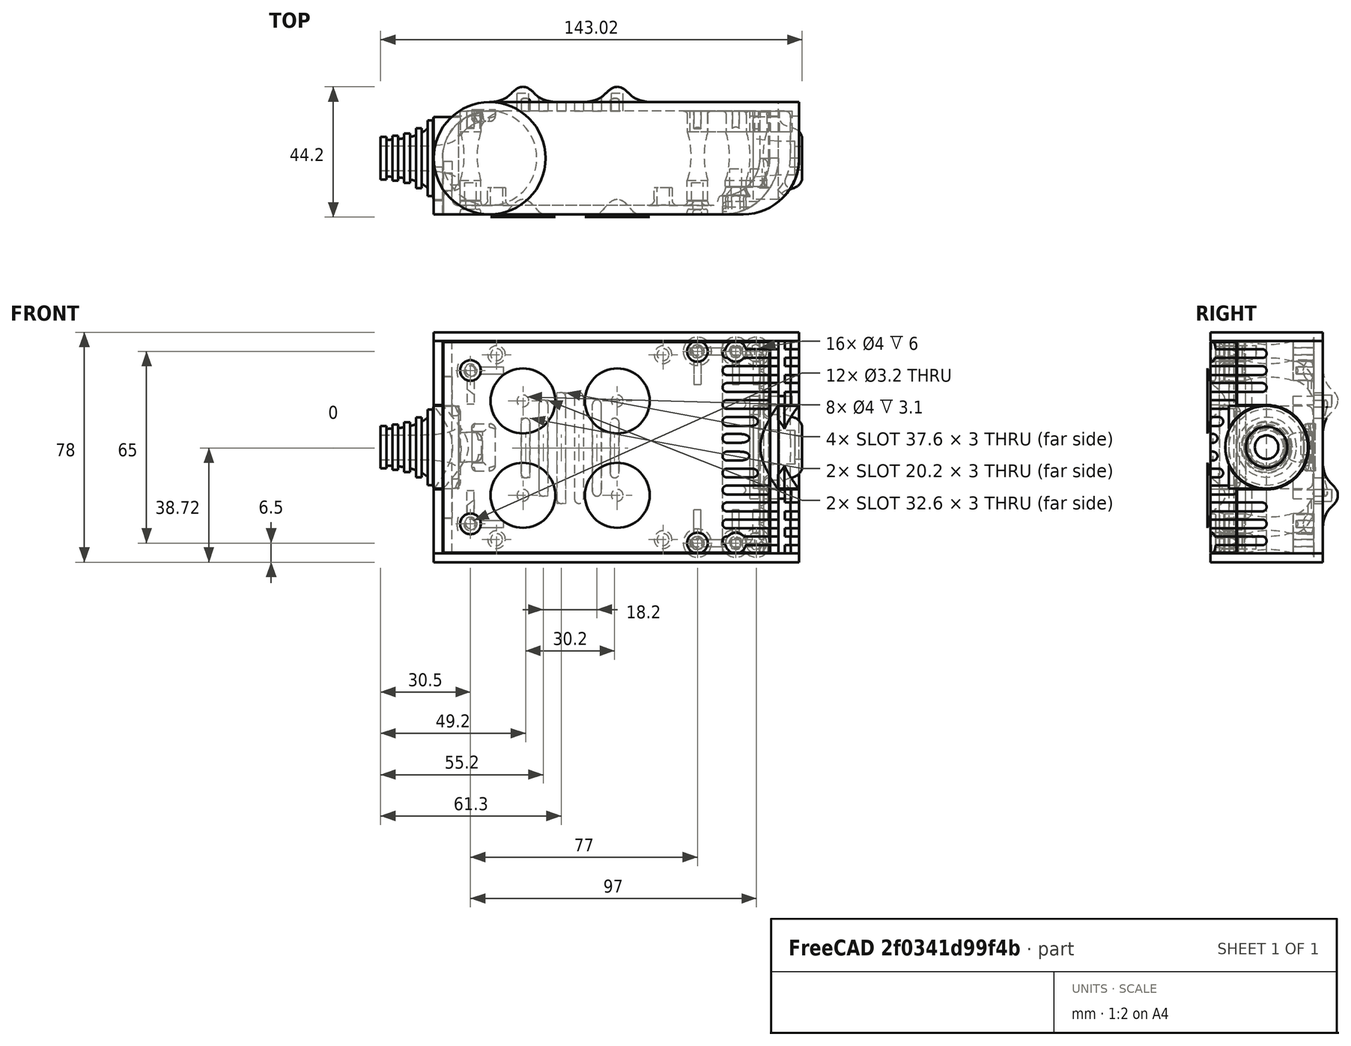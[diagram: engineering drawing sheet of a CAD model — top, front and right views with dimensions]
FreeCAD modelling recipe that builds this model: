
FCSTD DOCUMENT  (FreeCAD 0.19R0.19.2)
Label: enclosure_146
License: All rights reserved
LicenseURL: http://en.wikipedia.org/wiki/All_rights_reserved
objects: Part::Feature×96, Part::Revolution×96, Part::MultiFuse×79, Sketcher::SketchObject×52, Part::Extrusion×40, Part::Cut×39, Part::Fillet×36, Part::Cylinder×36, Part::Box×23, App::MeasureDistance×4
note: 497 computed .brp shape members not serialized (recipe doc carries the construction recipe); baked Part::Feature solids carry a one-line shape summary decoded from their .brp

FEATURE [Sketcher::SketchObject] Sketch  label="topSketch"
  FullyConstrained = true
  sketch-geometry (20):
    g0: LineSegment StartX=5.21097e-06 StartY=3 StartZ=0 EndX=5.21097e-06 EndY=19 EndZ=0
    g1: ArcOfCircle CenterX=19 CenterY=19 CenterZ=0 NormalX=0 NormalY=0 NormalZ=1 AngleXU=0 Radius=19 StartAngle=1.5708 EndAngle=3.14159
    g2: ArcOfCircle CenterX=19 CenterY=19 CenterZ=0 NormalX=0 NormalY=0 NormalZ=1 AngleXU=0 Radius=16 StartAngle=1.5708 EndAngle=3.14159
    g3: LineSegment StartX=114 StartY=35 StartZ=0 EndX=19 EndY=35 EndZ=0
    g4: LineSegment StartX=5.21097e-06 StartY=3 StartZ=0 EndX=5.21097e-06 EndY=0 EndZ=0
    g5: LineSegment StartX=3 StartY=0 StartZ=0 EndX=5.21097e-06 EndY=0 EndZ=0
    g6: LineSegment StartX=3 StartY=19 StartZ=0 EndX=3 EndY=0 EndZ=0
    g7: LineSegment StartX=19 StartY=38 StartZ=0 EndX=124 EndY=38 EndZ=0
    g8: Circle CenterX=119 CenterY=35 CenterZ=0 NormalX=0 NormalY=0 NormalZ=1 AngleXU=0 Radius=1
    g9: Circle CenterX=121 CenterY=35 CenterZ=0 NormalX=0 NormalY=0 NormalZ=1 AngleXU=0 Radius=1
    g10: Circle CenterX=121 CenterY=33 CenterZ=0 NormalX=0 NormalY=0 NormalZ=1 AngleXU=0 Radius=1
    g11: BSplineCurve PolesCount=3 KnotsCount=2 Degree=2 IsPeriodic=0
    g12: GeomPoint X=119 Y=35 Z=0
    g13: GeomPoint X=121 Y=33 Z=0
    g14: LineSegment StartX=119 StartY=35 StartZ=0 EndX=114 EndY=35 EndZ=0
    g15: ArcOfCircle CenterX=105 CenterY=19 CenterZ=0 NormalX=0 NormalY=0 NormalZ=1 AngleXU=0 Radius=19 StartAngle=5.7297 EndAngle=6.28319
    g16: ArcOfCircle CenterX=105 CenterY=19 CenterZ=0 NormalX=0 NormalY=0 NormalZ=1 AngleXU=0 Radius=16 StartAngle=5.60905 EndAngle=6.28319
    g17: LineSegment StartX=121 StartY=33 StartZ=0 EndX=121 EndY=19 EndZ=0
    g18: LineSegment StartX=124 StartY=38 StartZ=0 EndX=124 EndY=19 EndZ=0
    g19: LineSegment StartX=117.5 StartY=9.01251 StartZ=0 EndX=121.163 EndY=9.0125 EndZ=0
  constraints (46):
    c: Vertical(g0)
    c: Block(g0)
    c: Coincident(g1,g0)
    c: Block(g1)
    c: Coincident(g2,g1)
    c: Block(g2)
    c: Coincident(g3,g2)
    c: Horizontal(g3)
    c: Tangent(g3,g2)
    c: Coincident(g4,g0)
    c: Distance(g4) = 3
    c: Vertical(g4)
    c: Coincident(g5,g4)
    c: Horizontal(g5)
    c: Coincident(g6,g2)
    c: Coincident(g6,g5)
    c: Vertical(g6)
    c: Horizontal(g7)
    c: Distance(g7) = 105
    c: Coincident(g7,g1)
    c: Block(g3)
    c: Weight(g8) = 1
    c: Equal(g8,g9)
    c: Equal(g8,g10)
    c: InternalAlignment(g8,g11)
    c: InternalAlignment(g9,g11)
    c: InternalAlignment(g10,g11)
    c: InternalAlignment(g12,g11)
    c: InternalAlignment(g13,g11)
    c: Block(g11)
    c: Coincident(g14,g11)
    c: Coincident(g14,g3)
    c: Horizontal(g14)
    c: Block(g15)
    c: Coincident(g16,g15)
    c: Block(g16)
    c: Coincident(g17,g11)
    c: Coincident(g17,g16)
    c: Vertical(g17)
    c: Distance(g17) = 14
    c: Coincident(g18,g7)
    c: Coincident(g18,g15)
    c: Vertical(g18)
    c: Distance(g18) = 19
    c: Coincident(g19,g16)
    c: Coincident(g19,g15)
FEATURE [Sketcher::SketchObject] Sketch001  label="bottomSketch"
  FullyConstrained = true
  sketch-geometry (32):
    g0: LineSegment StartX=3.3 StartY=-6.03275e-07 StartZ=0 EndX=98 EndY=-6.03275e-07 EndZ=0
    g1: ArcOfCircle CenterX=98 CenterY=19 CenterZ=0 NormalX=0 NormalY=0 NormalZ=1 AngleXU=0 Radius=19 StartAngle=4.71239 EndAngle=5.71103
    g2: LineSegment StartX=6.3 StartY=8 StartZ=0 EndX=3.3 EndY=8 EndZ=0
    g3: LineSegment StartX=3.3 StartY=8 StartZ=0 EndX=3.3 EndY=-6.03275e-07 EndZ=0
    g4: ArcOfCircle CenterX=8.3 CenterY=5 CenterZ=0 NormalX=0 NormalY=0 NormalZ=1 AngleXU=0 Radius=2 StartAngle=3.14159 EndAngle=4.71239
    g5: LineSegment StartX=6.3 StartY=8 StartZ=0 EndX=6.3 EndY=5 EndZ=0
    g6: ArcOfCircle CenterX=98 CenterY=19 CenterZ=0 NormalX=0 NormalY=0 NormalZ=1 AngleXU=0 Radius=12.7 StartAngle=4.71239 EndAngle=6.28319
    g7: LineSegment StartX=94.7 StartY=3 StartZ=0 EndX=8.3 EndY=3 EndZ=0
    g8-g12: Circle x5 (B-spline internal-alignment scaffolding for g13; pole/knot coordinates omitted)
    g13: BSplineCurve PolesCount=5 KnotsCount=3 Degree=3 IsPeriodic=0
    g14: GeomPoint X=98 Y=6.3 Z=0
    g15: GeomPoint X=96.3938 Y=4.71946 Z=0
    g16: GeomPoint X=94.7 Y=3 Z=0
    g17-g23: Circle x7 (B-spline internal-alignment scaffolding for g24; pole/knot coordinates omitted)
    g24: BSplineCurve PolesCount=7 KnotsCount=5 Degree=3 IsPeriodic=0
    g25-g29: GeomPoint x5 (B-spline internal-alignment scaffolding for g24; pole/knot coordinates omitted)
    g30: ArcOfCircle CenterX=98 CenterY=19 CenterZ=0 NormalX=0 NormalY=0 NormalZ=1 AngleXU=0 Radius=15.7 StartAngle=5.81226 EndAngle=6.28319
    g31: LineSegment StartX=110.7 StartY=19 StartZ=0 EndX=113.7 EndY=19 EndZ=0
  constraints (41):
    c: Horizontal(g0)
    c: Coincident(g1,g0)
    c: Block(g1)
    c: Horizontal(g2)
    c: Distance(g2) = 3
    c: Coincident(g3,g2)
    c: Vertical(g3)
    c: Coincident(g3,g0)
    c: Block(g4)
    c: Block(g2)
    c: Coincident(g5,g2)
    c: Coincident(g5,g4)
    c: Vertical(g5)
    c: Coincident(g6,g1)
    c: Block(g6)
    c: Coincident(g7,g4)
    c: Horizontal(g7)
    c: Block(g0)
    c: Block(g7)
    c: Block(g3)
    c: Coincident(g13,g6)
    c: Weight(g8) = 1
    c: Equal(g8, g9-g12) x4
    c: Coincident(g13,g7)
    c: InternalAlignment(g8-g12 -> g13) x5
    c: InternalAlignment(g14,g13)
    c: InternalAlignment(g15,g13)
    c: InternalAlignment(g16,g13)
    c: Block(g13)
    c: Weight(g17) = 1
    c: Equal(g17, g18-g23) x6
    c: Coincident(g24,g1)
    c: InternalAlignment(g17-g23 -> g24) x7
    c: InternalAlignment(g25-g29 -> g24) x5
    c: Block(g24)
    c: Coincident(g30,g24)
    c: Coincident(g31,g6)
    c: Coincident(g31,g30)
    c: Horizontal(g31)
    c: Block(g31)
    c: Block(g30)
FEATURE [Part::Extrusion] Extrude  label="top"
  Base = -> Sketch
  Dir = (0,0,1)
  DirMode = 2
  FaceMakerClass = Part::FaceMakerBullseye
  LengthFwd = 72
  LengthRev = 0
  Solid = true
  Symmetric = false
FEATURE [Part::Extrusion] Extrude001  label="bottom"
  Base = -> Sketch001
  Dir = (0,0,1)
  DirMode = 2
  FaceMakerClass = Part::FaceMakerBullseye
  LengthFwd = 71.4
  LengthRev = 0
  Placement = pos=(0,0,0.3) rot=(0,0,1;0rad)
  Solid = true
  Symmetric = false
FEATURE [Sketcher::SketchObject] Sketch002  label="topSketch001"
  FullyConstrained = true
  sketch-geometry (6):
    g0: ArcOfCircle CenterX=19 CenterY=19 CenterZ=0 NormalX=0 NormalY=0 NormalZ=1 AngleXU=0 Radius=19 StartAngle=1.5708 EndAngle=3.14159
    g1: LineSegment StartX=5.22862e-06 StartY=19 StartZ=0 EndX=5.22862e-06 EndY=1.19904e-11 EndZ=0
    g2: LineSegment StartX=19 StartY=38 StartZ=0 EndX=124 EndY=38 EndZ=0
    g3: LineSegment StartX=5.22862e-06 StartY=1.19904e-11 StartZ=0 EndX=105 EndY=1.19904e-11 EndZ=0
    g4: ArcOfCircle CenterX=105 CenterY=19 CenterZ=0 NormalX=0 NormalY=0 NormalZ=1 AngleXU=0 Radius=19 StartAngle=4.71239 EndAngle=6.28319
    g5: LineSegment StartX=124 StartY=38 StartZ=0 EndX=124 EndY=19 EndZ=0
  constraints (16):
    c: Block(g0)
    c: Coincident(g1,g0)
    c: Vertical(g1)
    c: Horizontal(g2)
    c: Distance(g2) = 105
    c: Coincident(g2,g0)
    c: Distance(g1) = 19
    c: Coincident(g3,g1)
    c: Horizontal(g3)
    c: Distance(g3) = 105
    c: Block(g4)
    c: Coincident(g4,g3)
    c: Coincident(g5,g2)
    c: Coincident(g5,g4)
    c: Vertical(g5)
    c: Distance(g5) = 19
FEATURE [Part::Extrusion] Extrude002  label="sideA"
  Base = -> Sketch002
  Dir = (0,0,1)
  DirMode = 2
  FaceMakerClass = Part::FaceMakerBullseye
  LengthFwd = 3
  LengthRev = 0
  Placement = pos=(0,0,-3) rot=(0,0,1;0rad)
  Solid = true
  Symmetric = false
FEATURE [Sketcher::SketchObject] Sketch003  label="topSketch002"
  FullyConstrained = true
  sketch-geometry (6):
    g0: LineSegment StartX=19 StartY=38 StartZ=0 EndX=117 EndY=38 EndZ=0
    g1: ArcOfCircle CenterX=19 CenterY=19 CenterZ=0 NormalX=0 NormalY=0 NormalZ=1 AngleXU=0 Radius=19 StartAngle=1.5708 EndAngle=3.14159
    g2: LineSegment StartX=117 StartY=38 StartZ=0 EndX=117 EndY=19 EndZ=0
    g3: LineSegment StartX=98 StartY=1.0161e-12 StartZ=0 EndX=5.22862e-06 EndY=1.0161e-12 EndZ=0
    g4: LineSegment StartX=5.22862e-06 StartY=19 StartZ=0 EndX=5.22862e-06 EndY=1.0161e-12 EndZ=0
    g5: ArcOfCircle CenterX=98 CenterY=19 CenterZ=0 NormalX=0 NormalY=0 NormalZ=1 AngleXU=0 Radius=19 StartAngle=4.71239 EndAngle=6.28319
  constraints (16):
    c: Horizontal(g0)
    c: Distance(g0) = 98
    c: Coincident(g1,g0)
    c: Block(g1)
    c: Coincident(g2,g0)
    c: Vertical(g2)
    c: Distance(g2) = 19
    c: Horizontal(g3)
    c: Coincident(g4,g1)
    c: Vertical(g4)
    c: Coincident(g3,g4)
    c: Block(g3)
    c: Coincident(g5,g2)
    c: Coincident(g5,g3)
    c: Block(g0)
    c: Block(g5)
FEATURE [Sketcher::SketchObject] Sketch004
  FullyConstrained = true
  MapMode = 3
  Placement = pos=(0,0,0) rot=(1,0,0;1.5708rad)
  Support = -> [Extrude]
  sketch-geometry (8):
    g0: Circle CenterX=80.351 CenterY=-67.6202 CenterZ=0 NormalX=0 NormalY=0 NormalZ=1 AngleXU=0 Radius=2
    g1: Circle CenterX=80.351 CenterY=-67.6202 CenterZ=0 NormalX=0 NormalY=0 NormalZ=1 AngleXU=0 Radius=3
    g2: Circle CenterX=80.351 CenterY=-4.92017 CenterZ=0 NormalX=0 NormalY=0 NormalZ=1 AngleXU=0 Radius=2
    g3: Circle CenterX=80.351 CenterY=-4.92017 CenterZ=0 NormalX=0 NormalY=0 NormalZ=1 AngleXU=0 Radius=3
    g4: Circle CenterX=23.851 CenterY=-4.92017 CenterZ=0 NormalX=0 NormalY=0 NormalZ=1 AngleXU=0 Radius=2
    g5: Circle CenterX=23.851 CenterY=-4.92017 CenterZ=0 NormalX=0 NormalY=0 NormalZ=1 AngleXU=0 Radius=3
    g6: Circle CenterX=23.851 CenterY=-67.6202 CenterZ=0 NormalX=0 NormalY=0 NormalZ=1 AngleXU=0 Radius=2
    g7: Circle CenterX=23.851 CenterY=-67.6202 CenterZ=0 NormalX=0 NormalY=0 NormalZ=1 AngleXU=0 Radius=3
  constraints (8):
    c: Block(g3)
    c: Block(g2)
    c: Block(g1)
    c: Block(g0)
    c: Block(g6)
    c: Block(g7)
    c: Block(g4)
    c: Block(g5)
FEATURE [Part::Extrusion] Extrude004
  Base = -> Sketch004
  Dir = (0,-1,2e-16)
  DirMode = 2
  FaceMakerClass = Part::FaceMakerBullseye
  LengthFwd = 6
  LengthRev = 0
  Placement = pos=(0,9,0) rot=(0,0,1;0rad)
  Solid = true
  Symmetric = false
FEATURE [Sketcher::SketchObject] Sketch005
  FullyConstrained = true
  MapMode = 3
  Placement = pos=(0,0,0) rot=(1,0,0;1.5708rad)
  Support = -> [Extrude]
  sketch-geometry (8):
    g0: Circle CenterX=80.351 CenterY=-67.6202 CenterZ=0 NormalX=0 NormalY=0 NormalZ=1 AngleXU=0 Radius=3
    g1: Circle CenterX=80.351 CenterY=-4.92017 CenterZ=0 NormalX=0 NormalY=0 NormalZ=1 AngleXU=0 Radius=3
    g2: Circle CenterX=23.851 CenterY=-4.92017 CenterZ=0 NormalX=0 NormalY=0 NormalZ=1 AngleXU=0 Radius=3
    g3: Circle CenterX=23.851 CenterY=-67.6202 CenterZ=0 NormalX=0 NormalY=0 NormalZ=1 AngleXU=0 Radius=3
    g4: Circle CenterX=23.851 CenterY=-67.6202 CenterZ=0 NormalX=0 NormalY=0 NormalZ=1 AngleXU=0 Radius=5
    g5: Circle CenterX=80.351 CenterY=-67.6202 CenterZ=0 NormalX=0 NormalY=0 NormalZ=1 AngleXU=0 Radius=5
    g6: Circle CenterX=23.851 CenterY=-4.92017 CenterZ=0 NormalX=0 NormalY=0 NormalZ=1 AngleXU=0 Radius=5
    g7: Circle CenterX=80.351 CenterY=-4.92017 CenterZ=0 NormalX=0 NormalY=0 NormalZ=1 AngleXU=0 Radius=5
  constraints (8):
    c: Block(g1)
    c: Block(g0)
    c: Block(g3)
    c: Block(g2)
    c: Block(g5)
    c: Block(g4)
    c: Block(g6)
    c: Block(g7)
FEATURE [Part::Extrusion] Extrude005
  Base = -> Sketch005
  Dir = (0,-1,2e-16)
  DirMode = 2
  FaceMakerClass = Part::FaceMakerBullseye
  LengthFwd = 2
  LengthRev = 0
  Solid = true
  Symmetric = false
FEATURE [Sketcher::SketchObject] Sketch006
  FullyConstrained = true
  MapMode = 3
  Placement = pos=(0,0,0) rot=(1,0,0;1.5708rad)
  sketch-geometry (8):
    g0: Circle CenterX=80.351 CenterY=-67.6202 CenterZ=0 NormalX=0 NormalY=0 NormalZ=1 AngleXU=0 Radius=3
    g1: Circle CenterX=80.351 CenterY=-4.92017 CenterZ=0 NormalX=0 NormalY=0 NormalZ=1 AngleXU=0 Radius=3
    g2: Circle CenterX=23.851 CenterY=-4.92017 CenterZ=0 NormalX=0 NormalY=0 NormalZ=1 AngleXU=0 Radius=3
    g3: Circle CenterX=23.851 CenterY=-67.6202 CenterZ=0 NormalX=0 NormalY=0 NormalZ=1 AngleXU=0 Radius=3
    g4: Circle CenterX=23.851 CenterY=-67.6202 CenterZ=0 NormalX=0 NormalY=0 NormalZ=1 AngleXU=0 Radius=5
    g5: Circle CenterX=80.351 CenterY=-67.6202 CenterZ=0 NormalX=0 NormalY=0 NormalZ=1 AngleXU=0 Radius=5
    g6: Circle CenterX=23.851 CenterY=-4.92017 CenterZ=0 NormalX=0 NormalY=0 NormalZ=1 AngleXU=0 Radius=5
    g7: Circle CenterX=80.351 CenterY=-4.92017 CenterZ=0 NormalX=0 NormalY=0 NormalZ=1 AngleXU=0 Radius=5
  constraints (8):
    c: Block(g1)
    c: Block(g0)
    c: Block(g3)
    c: Block(g2)
    c: Block(g5)
    c: Block(g4)
    c: Block(g6)
    c: Block(g7)
FEATURE [Part::Extrusion] Extrude007
  Base = -> Sketch006
  Dir = (0,-1,2e-16)
  DirMode = 2
  FaceMakerClass = Part::FaceMakerBullseye
  LengthFwd = 2
  LengthRev = 0
  Solid = true
  Symmetric = false
FEATURE [Part::Fillet] Fillet
  Base = -> Extrude007
  Edges = 4 edges r=1.99: [Edge6,Edge12,Edge18,Edge24]
FEATURE [Part::Cut] Cut
  Base = -> Extrude005
  Placement = pos=(0,5,0) rot=(0,0,1;0rad)
  Tool = -> Fillet
FEATURE [Part::MultiFuse] Fusion  label="pCBScrews"
  Placement = pos=(-2.5,0,72.3) rot=(0,0,1;0rad)
  Shapes = -> [Extrude004,Cut]
FEATURE [App::MeasureDistance] Distance  label="Distance: 0.69 mm"
  Distance = 0.685967
  P1 = (24.0138,2.9647,0.3)
  P2 = (23.8901,3,-0.373787)
FEATURE [App::MeasureDistance] Distance001  label="Distance: 0.53 mm"
  Distance = 0.533607
  P1 = (80.2939,3,72.2334)
  P2 = (80.281,2.99661,71.7)
FEATURE [Part::Fillet] Fillet001
  Base = -> Extrude001
  Edges = 1 edges r=2.4: [Edge17]
FEATURE [Part::Fillet] Fillet002  label="bottom001"
  Base = -> Fillet001
  Edges = 1 edges r=2.4: [Edge36]
FEATURE [Part::Fillet] Fillet003  label="top001"
  Base = -> Extrude
  Edges = 1 edges r=2: [Edge1]
FEATURE [Sketcher::SketchObject] Sketch007
  FullyConstrained = true
  sketch-geometry (16):
    g0: LineSegment StartX=4 StartY=0 StartZ=0 EndX=4 EndY=2.4 EndZ=0
    g1: LineSegment StartX=4 StartY=2.4 StartZ=0 EndX=7 EndY=2.4 EndZ=0
    g2: LineSegment StartX=4 StartY=0 StartZ=0 EndX=5.7 EndY=0 EndZ=0
    g3: LineSegment StartX=5.7 StartY=0 StartZ=0 EndX=5.7 EndY=-5.6 EndZ=0
    g4-g8: Circle x5 (B-spline internal-alignment scaffolding for g9; pole/knot coordinates omitted)
    g9: BSplineCurve PolesCount=5 KnotsCount=3 Degree=3 IsPeriodic=0
    g10: GeomPoint X=7 Y=2.4 Z=0
    g11: GeomPoint X=10.4582 Y=-1.55472 Z=0
    g12: GeomPoint X=14 Y=-5.6 Z=0
    g13: LineSegment StartX=14 StartY=-5.6 StartZ=0 EndX=14 EndY=-14.1 EndZ=0
    g14: LineSegment StartX=14 StartY=-14.1 StartZ=0 EndX=6.5 EndY=-14.1 EndZ=0
    g15: LineSegment StartX=5.7 StartY=-5.6 StartZ=0 EndX=6.5 EndY=-14.1 EndZ=0
  constraints (28):
    c: Distance(g0) = 2.4
    c: Vertical(g0)
    c: Block(g0)
    c: Coincident(g1,g0)
    c: Horizontal(g1)
    c: Distance(g1) = 3
    c: Coincident(g2,g0)
    c: Horizontal(g2)
    c: Distance(g2) = 1.7
    c: Coincident(g3,g2)
    c: Vertical(g3)
    c: Distance(g3) = 5.6
    c: Coincident(g9,g1)
    c: Weight(g4) = 1
    c: Equal(g4, g5-g8) x4
    c: InternalAlignment(g4-g8 -> g9) x5
    c: InternalAlignment(g10,g9)
    c: InternalAlignment(g11,g9)
    c: InternalAlignment(g12,g9)
    c: Block(g9)
    c: Coincident(g13,g9)
    c: Vertical(g13)
    c: Distance(g13) = 8.5
    c: Coincident(g14,g13)
    c: Horizontal(g14)
    c: Distance(g14) = 7.5
    c: Coincident(g15,g3)
    c: Coincident(g15,g14)
FEATURE [Part::Feature] Face
  shape: bbox 10 x 16.5 x 2e-07 mm, 1 faces, 0 solids (baked)
FEATURE [Part::Revolution] Revolve  label="plugHousing"
  Angle = 360
  Axis = (0,1,0)
  Base = (0,0,0)
  FaceMakerClass = Part::FaceMakerBullseye
  Placement = pos=(0,0,36.15) rot=(0,0,1;0rad)
  Solid = false
  Source = -> Face
  Symmetric = false
FEATURE [Part::Feature] Face001
  shape: bbox 10 x 16.5 x 2e-07 mm, 1 faces, 0 solids (baked)
FEATURE [Part::Revolution] Revolve001  label="plugHousing001"
  Angle = 360
  Axis = (0,1,0)
  Base = (0,0,0)
  FaceMakerClass = Part::FaceMakerBullseye
  Placement = pos=(0,0,36.15) rot=(0,0,1;0rad)
  Solid = false
  Source = -> Face001
  Symmetric = false
FEATURE [Part::MultiFuse] Fusion001  label="plugHousing002"
  Placement = pos=(0,0,0) rot=(0,0,1;1.5708rad)
  Shapes = -> [Revolve001,Revolve]
FEATURE [Part::Feature] Face002
  shape: bbox 10 x 16.5 x 2e-07 mm, 1 faces, 0 solids (baked)
FEATURE [Part::Revolution] Revolve003  label="plugHousing005"
  Angle = 360
  Axis = (0,1,0)
  Base = (0,0,0)
  FaceMakerClass = Part::FaceMakerBullseye
  Placement = pos=(0,0,36.15) rot=(0,0,1;0rad)
  Solid = false
  Source = -> Face002
  Symmetric = false
FEATURE [Part::Feature] Face003
  shape: bbox 10 x 16.5 x 2e-07 mm, 1 faces, 0 solids (baked)
FEATURE [Part::Revolution] Revolve002  label="plugHousing003"
  Angle = 360
  Axis = (0,1,0)
  Base = (0,0,0)
  FaceMakerClass = Part::FaceMakerBullseye
  Placement = pos=(0,0,36.15) rot=(0,0,1;0rad)
  Solid = false
  Source = -> Face003
  Symmetric = false
FEATURE [Part::MultiFuse] Fusion002  label="plugHousing004"
  Placement = pos=(0,0,0) rot=(0,0,1;1.5708rad)
  Shapes = -> [Revolve002,Revolve003]
FEATURE [Part::MultiFuse] Fusion003  label="plugHousing006"
  Placement = pos=(0,19,0) rot=(0,0,1;3.14159rad)
  Shapes = -> [Fusion002,Fusion001]
FEATURE [Part::Feature] Face004
  shape: bbox 10 x 16.5 x 2e-07 mm, 1 faces, 0 solids (baked)
FEATURE [Part::Revolution] Revolve006  label="plugHousing010"
  Angle = 360
  Axis = (0,1,0)
  Base = (0,0,0)
  FaceMakerClass = Part::FaceMakerBullseye
  Placement = pos=(0,0,36.15) rot=(0,0,1;0rad)
  Solid = false
  Source = -> Face004
  Symmetric = false
FEATURE [Part::Feature] Face005
  shape: bbox 10 x 16.5 x 2e-07 mm, 1 faces, 0 solids (baked)
FEATURE [Part::Revolution] Revolve007  label="plugHousing011"
  Angle = 360
  Axis = (0,1,0)
  Base = (0,0,0)
  FaceMakerClass = Part::FaceMakerBullseye
  Placement = pos=(0,0,36.15) rot=(0,0,1;0rad)
  Solid = false
  Source = -> Face005
  Symmetric = false
FEATURE [Part::Feature] Face006
  shape: bbox 10 x 16.5 x 2e-07 mm, 1 faces, 0 solids (baked)
FEATURE [Part::Revolution] Revolve004  label="plugHousing007"
  Angle = 360
  Axis = (0,1,0)
  Base = (0,0,0)
  FaceMakerClass = Part::FaceMakerBullseye
  Placement = pos=(0,0,36.15) rot=(0,0,1;0rad)
  Solid = false
  Source = -> Face006
  Symmetric = false
FEATURE [Part::MultiFuse] Fusion004  label="plugHousing009"
  Placement = pos=(0,0,0) rot=(0,0,1;1.5708rad)
  Shapes = -> [Revolve004,Revolve007]
FEATURE [Part::Feature] Face007
  shape: bbox 10 x 16.5 x 2e-07 mm, 1 faces, 0 solids (baked)
FEATURE [Part::Revolution] Revolve005  label="plugHousing008"
  Angle = 360
  Axis = (0,1,0)
  Base = (0,0,0)
  FaceMakerClass = Part::FaceMakerBullseye
  Placement = pos=(0,0,36.15) rot=(0,0,1;0rad)
  Solid = false
  Source = -> Face007
  Symmetric = false
FEATURE [Part::MultiFuse] Fusion005  label="plugHousing012"
  Placement = pos=(0,0,0) rot=(0,0,1;1.5708rad)
  Shapes = -> [Revolve006,Revolve005]
FEATURE [Part::MultiFuse] Fusion006  label="plugHousing013"
  Placement = pos=(0,19,0) rot=(0,0,1;3.14159rad)
  Shapes = -> [Fusion005,Fusion004]
FEATURE [Part::MultiFuse] Fusion007  label="plugHousing014"
  Placement = pos=(122.621,0,-0.15) rot=(0,0,1;0rad)
  Shapes = -> [Fusion003,Fusion006]
FEATURE [Part::Cylinder] Cylinder002
  Angle = 360
  AttacherType = Attacher::AttachEngine3D
  Height = 20
  Placement = pos=(0,0,36.15) rot=(0,0,1;0rad)
  Radius = 4
FEATURE [Part::Cylinder] Cylinder003
  Angle = 360
  AttacherType = Attacher::AttachEngine3D
  Height = 10
  Placement = pos=(0,0,36.15) rot=(0,0,1;0rad)
  Radius = 4
FEATURE [Part::MultiFuse] Fusion009  label="removeToCreateHoleForPlugHousing"
  Placement = pos=(70,19,36.15) rot=(0,1,0;1.5708rad)
  Shapes = -> [Cylinder002,Cylinder003]
FEATURE [Part::Cylinder] Cylinder004
  Angle = 360
  AttacherType = Attacher::AttachEngine3D
  Height = 20
  Placement = pos=(0,0,36.15) rot=(0,0,1;0rad)
  Radius = 4
FEATURE [Part::Cylinder] Cylinder005
  Angle = 360
  AttacherType = Attacher::AttachEngine3D
  Height = 10
  Placement = pos=(0,0,36.15) rot=(0,0,1;0rad)
  Radius = 4
FEATURE [Part::MultiFuse] Fusion010  label="removeToCreateHoleForPlugHousing001"
  Placement = pos=(70,19,36.15) rot=(0,1,0;1.5708rad)
  Shapes = -> [Cylinder004,Cylinder005]
FEATURE [Part::Cut] Cut001
  Base = -> Fillet003
  Tool = -> Fusion010
FEATURE [Part::Cut] Cut002  label="Bottom"
  Base = -> Fillet002
  Tool = -> Fusion009
FEATURE [Part::Feature] Face008
  shape: bbox 10 x 16.5 x 2e-07 mm, 1 faces, 0 solids (baked)
FEATURE [Part::Revolution] Revolve011  label="plugHousing021"
  Angle = 360
  Axis = (0,1,0)
  Base = (0,0,0)
  FaceMakerClass = Part::FaceMakerBullseye
  Placement = pos=(0,0,36.15) rot=(0,0,1;0rad)
  Solid = false
  Source = -> Face008
  Symmetric = false
FEATURE [Part::Feature] Face009
  shape: bbox 10 x 16.5 x 2e-07 mm, 1 faces, 0 solids (baked)
FEATURE [Part::Revolution] Revolve012  label="plugHousing022"
  Angle = 360
  Axis = (0,1,0)
  Base = (0,0,0)
  FaceMakerClass = Part::FaceMakerBullseye
  Placement = pos=(0,0,36.15) rot=(0,0,1;0rad)
  Solid = false
  Source = -> Face009
  Symmetric = false
FEATURE [Part::Feature] Face010 .. Face013  x4 (patterned run collapsed; names and placements below)
  shape: bbox 10 x 16.5 x 2e-07 mm, 1 faces, 0 solids (baked)
FEATURE [Part::Revolution] Revolve015  label="plugHousing027"
  Angle = 360
  Axis = (0,1,0)
  Base = (0,0,0)
  FaceMakerClass = Part::FaceMakerBullseye
  Placement = pos=(0,0,36.15) rot=(0,0,1;0rad)
  Solid = false
  Source = -> Face013
  Symmetric = false
FEATURE [Part::Feature] Face014
  shape: bbox 10 x 16.5 x 2e-07 mm, 1 faces, 0 solids (baked)
FEATURE [Part::Feature] Face015
  shape: bbox 10 x 16.5 x 2e-07 mm, 1 faces, 0 solids (baked)
FEATURE [Part::Feature] Face016
  shape: bbox 10 x 16.5 x 2e-07 mm, 1 faces, 0 solids (baked)
FEATURE [Part::Revolution] Revolve019  label="plugHousing033"
  Angle = 360
  Axis = (0,1,0)
  Base = (0,0,0)
  FaceMakerClass = Part::FaceMakerBullseye
  Placement = pos=(0,0,36.15) rot=(0,0,1;0rad)
  Solid = false
  Source = -> Face016
  Symmetric = false
FEATURE [Part::Feature] Face017
  shape: bbox 10 x 16.5 x 2e-07 mm, 1 faces, 0 solids (baked)
FEATURE [Part::Revolution] Revolve020  label="plugHousing034"
  Angle = 360
  Axis = (0,1,0)
  Base = (0,0,0)
  FaceMakerClass = Part::FaceMakerBullseye
  Placement = pos=(0,0,36.15) rot=(0,0,1;0rad)
  Solid = false
  Source = -> Face017
  Symmetric = false
FEATURE [Part::Feature] Face018
  shape: bbox 10 x 16.5 x 2e-07 mm, 1 faces, 0 solids (baked)
FEATURE [Part::Revolution] Revolve016  label="plugHousing030"
  Angle = 360
  Axis = (0,1,0)
  Base = (0,0,0)
  FaceMakerClass = Part::FaceMakerBullseye
  Placement = pos=(0,0,36.15) rot=(0,0,1;0rad)
  Solid = false
  Source = -> Face018
  Symmetric = false
FEATURE [Part::MultiFuse] Fusion020  label="plugHousing038"
  Placement = pos=(0,0,0) rot=(0,0,1;1.5708rad)
  Shapes = -> [Revolve016,Revolve020]
FEATURE [Part::Feature] Face019
  shape: bbox 10 x 16.5 x 2e-07 mm, 1 faces, 0 solids (baked)
FEATURE [Part::Feature] Face020
  shape: bbox 10 x 16.5 x 2e-07 mm, 1 faces, 0 solids (baked)
FEATURE [Part::Revolution] Revolve017  label="plugHousing031"
  Angle = 360
  Axis = (0,1,0)
  Base = (0,0,0)
  FaceMakerClass = Part::FaceMakerBullseye
  Placement = pos=(0,0,36.15) rot=(0,0,1;0rad)
  Solid = false
  Source = -> Face020
  Symmetric = false
FEATURE [Part::MultiFuse] Fusion021  label="plugHousing039"
  Placement = pos=(0,0,0) rot=(0,0,1;1.5708rad)
  Shapes = -> [Revolve019,Revolve017]
FEATURE [Part::MultiFuse] Fusion023  label="plugHousing041"
  Placement = pos=(0,19,0) rot=(0,0,1;3.14159rad)
  Shapes = -> [Fusion021,Fusion020]
FEATURE [Part::Revolution] Revolve022  label="plugHousing043"
  Angle = 360
  Axis = (0,1,0)
  Base = (0,0,0)
  FaceMakerClass = Part::FaceMakerBullseye
  Placement = pos=(0,0,36.15) rot=(0,0,1;0rad)
  Solid = false
  Source = -> Face019
  Symmetric = false
FEATURE [Part::Feature] Face021
  shape: bbox 10 x 16.5 x 2e-07 mm, 1 faces, 0 solids (baked)
FEATURE [Part::Revolution] Revolve023  label="plugHousing044"
  Angle = 360
  Axis = (0,1,0)
  Base = (0,0,0)
  FaceMakerClass = Part::FaceMakerBullseye
  Placement = pos=(0,0,36.15) rot=(0,0,1;0rad)
  Solid = false
  Source = -> Face021
  Symmetric = false
FEATURE [Part::Feature] Face022
  shape: bbox 10 x 16.5 x 2e-07 mm, 1 faces, 0 solids (baked)
FEATURE [Part::Revolution] Revolve018  label="plugHousing032"
  Angle = 360
  Axis = (0,1,0)
  Base = (0,0,0)
  FaceMakerClass = Part::FaceMakerBullseye
  Placement = pos=(0,0,36.15) rot=(0,0,1;0rad)
  Solid = false
  Source = -> Face022
  Symmetric = false
FEATURE [Part::MultiFuse] Fusion022  label="plugHousing040"
  Placement = pos=(0,0,0) rot=(0,0,1;1.5708rad)
  Shapes = -> [Revolve018,Revolve023]
FEATURE [Part::Feature] Face023
  shape: bbox 10 x 16.5 x 2e-07 mm, 1 faces, 0 solids (baked)
FEATURE [Part::Revolution] Revolve021  label="plugHousing035"
  Angle = 360
  Axis = (0,1,0)
  Base = (0,0,0)
  FaceMakerClass = Part::FaceMakerBullseye
  Placement = pos=(0,0,36.15) rot=(0,0,1;0rad)
  Solid = false
  Source = -> Face023
  Symmetric = false
FEATURE [Part::MultiFuse] Fusion018  label="plugHousing036"
  Placement = pos=(0,0,0) rot=(0,0,1;1.5708rad)
  Shapes = -> [Revolve022,Revolve021]
FEATURE [Part::MultiFuse] Fusion019  label="plugHousing037"
  Placement = pos=(0,19,0) rot=(0,0,1;3.14159rad)
  Shapes = -> [Fusion018,Fusion022]
FEATURE [Part::MultiFuse] Fusion024  label="plugHousing042"
  Placement = pos=(122.621,0,-0.15) rot=(0,0,1;0rad)
  Shapes = -> [Fusion023,Fusion019]
FEATURE [Part::Cylinder] Cylinder006
  Angle = 360
  AttacherType = Attacher::AttachEngine3D
  Height = 20
  Placement = pos=(0,0,36.15) rot=(0,0,1;0rad)
  Radius = 14.3
FEATURE [Part::Cylinder] Cylinder007
  Angle = 360
  AttacherType = Attacher::AttachEngine3D
  Height = 10
  Placement = pos=(0,0,36.15) rot=(0,0,1;0rad)
  Radius = 4
FEATURE [Part::MultiFuse] Fusion026  label="removeToCreteHoleForPlugHousing"
  Placement = pos=(70,19,36) rot=(0,1,0;1.5708rad)
  Shapes = -> [Cylinder006,Cylinder007]
FEATURE [Part::Box] Box001  label="Cube001"
  AttacherType = Attacher::AttachEngine3D
  Height = 28
  Length = 3
  Placement = pos=(110.7,19,22) rot=(0,0,1;0rad)
  Width = 15.7
FEATURE [Part::Cut] Cut003  label="top002"
  Base = -> Cut001
  Tool = -> Fusion007
FEATURE [Part::Revolution] Revolve008  label="plugHousing015"
  Angle = 360
  Axis = (0,1,0)
  Base = (0,0,0)
  FaceMakerClass = Part::FaceMakerBullseye
  Placement = pos=(0,0,36.15) rot=(0,0,1;0rad)
  Solid = false
  Source = -> Face010
  Symmetric = false
FEATURE [Part::MultiFuse] Fusion013  label="plugHousing020"
  Placement = pos=(0,0,0) rot=(0,0,1;1.5708rad)
  Shapes = -> [Revolve008,Revolve012]
FEATURE [Part::Cut] Cut004  label="top003"
  Base = -> Cut003
  Placement = pos=(1,0,0) rot=(0,0,1;0rad)
  Tool = -> Fusion026
FEATURE [Part::Cylinder] Cylinder008
  Angle = 360
  AttacherType = Attacher::AttachEngine3D
  Height = 20
  Placement = pos=(0,0,36.15) rot=(0,0,1;0rad)
  Radius = 10.3
FEATURE [Part::Cylinder] Cylinder009
  Angle = 360
  AttacherType = Attacher::AttachEngine3D
  Height = 10
  Placement = pos=(0,0,36.15) rot=(0,0,1;0rad)
  Radius = 4
FEATURE [Part::MultiFuse] Fusion027  label="removeToCreteHoleForPlugHousing001"
  Placement = pos=(70,19,36) rot=(0,1,0;1.5708rad)
  Shapes = -> [Cylinder008,Cylinder009]
FEATURE [Part::Cut] Cut005  label="plugHousingTab"
  Base = -> Box001
  Tool = -> Fusion027
FEATURE [Part::MultiFuse] Fusion028  label="plugHousing045"
  Shapes = -> [Fusion024,Cut005]
FEATURE [Part::Box] Box002  label="Cube002"
  AttacherType = Attacher::AttachEngine3D
  Height = 28.8
  Length = 3
  Placement = pos=(107.3,28,21.6) rot=(0,0,1;0rad)
  Width = 7
FEATURE [Part::Box] Box003  label="Cube003"
  AttacherType = Attacher::AttachEngine3D
  Height = 3
  Length = 6.4
  Placement = pos=(107.3,28,18.6) rot=(0,0,1;0rad)
  Width = 7
FEATURE [Part::Box] Box004  label="Cube004"
  AttacherType = Attacher::AttachEngine3D
  Height = 3
  Length = 6.4
  Placement = pos=(107.3,28,50.4) rot=(0,0,1;0rad)
  Width = 7
FEATURE [Part::MultiFuse] Fusion029  label="plugHousingBracketHolder"
  Shapes = -> [Box004,Box002,Box003]
FEATURE [Part::Cylinder] Cylinder010
  Angle = 360
  AttacherType = Attacher::AttachEngine3D
  Height = 20
  Placement = pos=(0,0,36.15) rot=(0,0,1;0rad)
  Radius = 14.3
FEATURE [Part::Cylinder] Cylinder011
  Angle = 360
  AttacherType = Attacher::AttachEngine3D
  Height = 10
  Placement = pos=(0,0,36.15) rot=(0,0,1;0rad)
  Radius = 4
FEATURE [Part::MultiFuse] Fusion030  label="removeToCreteHoleForPlugHousing002"
  Placement = pos=(70,19,36) rot=(0,1,0;1.5708rad)
  Shapes = -> [Cylinder010,Cylinder011]
FEATURE [Part::Cut] Cut006  label="plugHousingBracketHolder001"
  Base = -> Fusion029
  Tool = -> Fusion030
FEATURE [Part::Cylinder] Cylinder012
  Angle = 360
  AttacherType = Attacher::AttachEngine3D
  Height = 20
  Placement = pos=(0,0,36.15) rot=(0,0,1;0rad)
  Radius = 7
FEATURE [Part::Cylinder] Cylinder013
  Angle = 360
  AttacherType = Attacher::AttachEngine3D
  Height = 10
  Placement = pos=(0,0,36.15) rot=(0,0,1;0rad)
  Radius = 4
FEATURE [Part::MultiFuse] Fusion032  label="removeToCreteHoleForPlugHousing003"
  Placement = pos=(70,19,36) rot=(0,1,0;1.5708rad)
  Shapes = -> [Cylinder012,Cylinder013]
FEATURE [Part::Cut] Cut007  label="bottom002"
  Base = -> Cut002
  Tool = -> Fusion032
FEATURE [Sketcher::SketchObject] Sketch008
  FullyConstrained = true
  sketch-geometry (54):
    g0: LineSegment StartX=-4.2 StartY=0 StartZ=0 EndX=-6.2 EndY=0 EndZ=0
    g1: LineSegment StartX=-14 StartY=-18 StartZ=0 EndX=-14 EndY=-26.5 EndZ=0
    g2: LineSegment StartX=-4.2 StartY=0 StartZ=0 EndX=-4.2 EndY=-13.4877 EndZ=0
    g3: Circle CenterX=-4.2 CenterY=-13.4877 CenterZ=0 NormalX=0 NormalY=0 NormalZ=1 AngleXU=0 Radius=1
    g4: Circle CenterX=-4.2 CenterY=-26.5 CenterZ=0 NormalX=0 NormalY=0 NormalZ=1 AngleXU=0 Radius=1
    g5: Circle CenterX=-8.2 CenterY=-26.5 CenterZ=0 NormalX=0 NormalY=0 NormalZ=1 AngleXU=0 Radius=1
    g6: BSplineCurve PolesCount=3 KnotsCount=2 Degree=2 IsPeriodic=0
    g7: GeomPoint X=-4.2 Y=-13.4877 Z=0
    g8: GeomPoint X=-8.2 Y=-26.5 Z=0
    g9: LineSegment StartX=-14 StartY=-26.5 StartZ=0 EndX=-8.2 EndY=-26.5 EndZ=0
    g10: LineSegment StartX=-10.15 StartY=-12 StartZ=0 EndX=-10.15 EndY=-14 EndZ=0
    g11: LineSegment StartX=-12.8401 StartY=-16 StartZ=0 EndX=-10.1571 EndY=-16 EndZ=0
    g12: LineSegment StartX=-10.15 StartY=-14 StartZ=0 EndX=-8.70761 EndY=-14 EndZ=0
    g13: LineSegment StartX=-12.8401 StartY=-16 StartZ=0 EndX=-12.8401 EndY=-17.6958 EndZ=0
    g14: LineSegment StartX=-10.15 StartY=-12 StartZ=0 EndX=-7.79258 EndY=-12 EndZ=0
    g15: Circle CenterX=-6.2215 CenterY=-2 CenterZ=0 NormalX=0 NormalY=0 NormalZ=1 AngleXU=0 Radius=1
    g16: Circle CenterX=-6.22762 CenterY=-2.58724 CenterZ=0 NormalX=0 NormalY=0 NormalZ=1 AngleXU=0 Radius=1
    g17: Circle CenterX=-6.32538 CenterY=-4 CenterZ=0 NormalX=0 NormalY=0 NormalZ=1 AngleXU=0 Radius=1
    g18: BSplineCurve PolesCount=3 KnotsCount=2 Degree=2 IsPeriodic=0
    g19: GeomPoint X=-6.2215 Y=-2 Z=0
    g20: GeomPoint X=-6.32538 Y=-4 Z=0
    g21: Circle CenterX=-6.48644 CenterY=-5.99526 CenterZ=0 NormalX=0 NormalY=0 NormalZ=1 AngleXU=0 Radius=1
    g22: Circle CenterX=-6.58486 CenterY=-6.99526 CenterZ=0 NormalX=0 NormalY=0 NormalZ=1 AngleXU=0 Radius=1
    g23: Circle CenterX=-6.77343 CenterY=-8 CenterZ=0 NormalX=0 NormalY=0 NormalZ=1 AngleXU=0 Radius=1
    g24: BSplineCurve PolesCount=3 KnotsCount=2 Degree=2 IsPeriodic=0
    g25: GeomPoint X=-6.48644 Y=-5.99526 Z=0
    g26: GeomPoint X=-6.77343 Y=-8 Z=0
    g27: Circle CenterX=-7.19003 CenterY=-10 CenterZ=0 NormalX=0 NormalY=0 NormalZ=1 AngleXU=0 Radius=1
    g28: Circle CenterX=-7.44407 CenterY=-11.0915 CenterZ=0 NormalX=0 NormalY=0 NormalZ=1 AngleXU=0 Radius=1
    g29: Circle CenterX=-7.79258 CenterY=-12 CenterZ=0 NormalX=0 NormalY=0 NormalZ=1 AngleXU=0 Radius=1
    g30: BSplineCurve PolesCount=3 KnotsCount=2 Degree=2 IsPeriodic=0
    g31: GeomPoint X=-7.19003 Y=-10 Z=0
    g32: GeomPoint X=-7.79258 Y=-12 Z=0
    g33: Circle CenterX=-8.70761 CenterY=-14 CenterZ=0 NormalX=0 NormalY=0 NormalZ=1 AngleXU=0 Radius=1
    g34: Circle CenterX=-9.33087 CenterY=-15.1837 CenterZ=0 NormalX=0 NormalY=0 NormalZ=1 AngleXU=0 Radius=1
    g35: Circle CenterX=-10.1571 CenterY=-16 CenterZ=0 NormalX=0 NormalY=0 NormalZ=1 AngleXU=0 Radius=1
    g36: BSplineCurve PolesCount=3 KnotsCount=2 Degree=2 IsPeriodic=0
    g37: GeomPoint X=-8.70761 Y=-14 Z=0
    g38: GeomPoint X=-10.1571 Y=-16 Z=0
    g39: Circle CenterX=-12.8401 CenterY=-17.6958 CenterZ=0 NormalX=0 NormalY=0 NormalZ=1 AngleXU=0 Radius=1
    g40: Circle CenterX=-13.3521 CenterY=-17.9027 CenterZ=0 NormalX=0 NormalY=0 NormalZ=1 AngleXU=0 Radius=1
    g41: Circle CenterX=-14 CenterY=-18 CenterZ=0 NormalX=0 NormalY=0 NormalZ=1 AngleXU=0 Radius=1
    g42: BSplineCurve PolesCount=3 KnotsCount=2 Degree=2 IsPeriodic=0
    g43: GeomPoint X=-12.8401 Y=-17.6958 Z=0
    g44: GeomPoint X=-14 Y=-18 Z=0
    g45: LineSegment StartX=-6.2 StartY=0 StartZ=0 EndX=-7.2 EndY=0 EndZ=0
    g46: LineSegment StartX=-7.2 StartY=0 StartZ=0 EndX=-7.2 EndY=-2 EndZ=0
    g47: LineSegment StartX=-7.2 StartY=-2 StartZ=0 EndX=-6.2215 EndY=-2 EndZ=0
    g48: LineSegment StartX=-6.32538 StartY=-4 StartZ=0 EndX=-7.65538 EndY=-4 EndZ=0
    g49: LineSegment StartX=-7.65538 StartY=-4 StartZ=0 EndX=-7.65538 EndY=-5.99526 EndZ=0
    g50: LineSegment StartX=-7.65538 StartY=-5.99526 StartZ=0 EndX=-6.48644 EndY=-5.99526 EndZ=0
    g51: LineSegment StartX=-6.77343 StartY=-8 StartZ=0 EndX=-8.43343 EndY=-8 EndZ=0
    g52: LineSegment StartX=-8.43343 StartY=-8 StartZ=0 EndX=-8.43343 EndY=-10 EndZ=0
    g53: LineSegment StartX=-8.43343 StartY=-10 StartZ=0 EndX=-7.19003 EndY=-10 EndZ=0
  constraints (112):
    c: Horizontal(g0)
    c: Distance(g0) = 2
    c: Block(g0)
    c: Vertical(g1)
    c: Coincident(g2,g0)
    c: Vertical(g2)
    c: Block(g2)
    c: Coincident(g6,g2)
    c: Weight(g3) = 1
    c: Equal(g3,g4)
    c: Equal(g3,g5)
    c: InternalAlignment(g3,g6)
    c: InternalAlignment(g4,g6)
    c: InternalAlignment(g5,g6)
    c: InternalAlignment(g7,g6)
    c: InternalAlignment(g8,g6)
    c: Block(g6)
    c: Coincident(g9,g1)
    c: Coincident(g9,g6)
    c: Horizontal(g9)
    c: Vertical(g10)
    c: Block(g10)
    c: Horizontal(g11)
    c: Block(g11)
    c: Coincident(g12,g10)
    c: Horizontal(g12)
    c: Block(g12)
    c: Coincident(g13,g11)
    c: Vertical(g13)
    c: Block(g13)
    c: Coincident(g14,g10)
    c: Horizontal(g14)
    c: Block(g14)
    c: Block(g9)
    c: Block(g1)
    c: Weight(g15) = 1
    c: Equal(g15,g16)
    c: Equal(g15,g17)
    c: InternalAlignment(g15,g18)
    c: InternalAlignment(g16,g18)
    c: InternalAlignment(g17,g18)
    c: InternalAlignment(g19,g18)
    c: InternalAlignment(g20,g18)
    c: Weight(g21) = 1
    c: Equal(g21,g22)
    c: Equal(g21,g23)
    c: InternalAlignment(g21,g24)
    c: InternalAlignment(g22,g24)
    c: InternalAlignment(g23,g24)
    c: InternalAlignment(g25,g24)
    c: InternalAlignment(g26,g24)
    c: Weight(g27) = 1
    c: Equal(g27,g28)
    c: Equal(g27,g29)
    c: Coincident(g30,g14)
    c: InternalAlignment(g27,g30)
    c: InternalAlignment(g28,g30)
    c: InternalAlignment(g29,g30)
    c: InternalAlignment(g31,g30)
    c: InternalAlignment(g32,g30)
    c: Coincident(g36,g12)
    c: Weight(g33) = 1
    c: Equal(g33,g34)
    c: Equal(g33,g35)
    c: Coincident(g36,g11)
    c: InternalAlignment(g33,g36)
    c: InternalAlignment(g34,g36)
    c: InternalAlignment(g35,g36)
    c: InternalAlignment(g37,g36)
    c: InternalAlignment(g38,g36)
    c: Coincident(g42,g13)
    c: Weight(g39) = 1
    c: Equal(g39,g40)
    c: Equal(g39,g41)
    c: Coincident(g42,g1)
    c: InternalAlignment(g39,g42)
    c: InternalAlignment(g40,g42)
    c: InternalAlignment(g41,g42)
    c: InternalAlignment(g43,g42)
    c: InternalAlignment(g44,g42)
    c: Block(g18)
    c: Block(g24)
    c: Block(g30)
    c: Block(g36)
    c: Block(g42)
    c: Horizontal(g45)
    c: Coincident(g45,g0)
    c: Vertical(g46)
    c: Coincident(g46,g45)
    c: Coincident(g47,g46)
    c: Coincident(g47,g18)
    c: Horizontal(g47)
    c: Block(g46)
    c: Coincident(g48,g18)
    c: Horizontal(g48)
    c: Distance(g48) = 1.33
    c: Vertical(g49)
    c: Coincident(g49,g48)
    c: Coincident(g50,g49)
    c: Coincident(g50,g24)
    c: Horizontal(g50)
    c: Tangent(g50,g22)
    c: Horizontal(g51)
    c: Coincident(g51,g24)
    c: Block(g51)
    c: Vertical(g52)
    c: Block(g52)
    c: Coincident(g52,g51)
    c: Coincident(g53,g52)
    c: Coincident(g53,g30)
    c: Horizontal(g53)
    c: Distance(g1) = 8.5
FEATURE [Part::Feature] Face024
  shape: bbox 9.8 x 26.5 x 2e-07 mm, 1 faces, 0 solids (baked)
FEATURE [Part::Revolution] Revolve024
  Angle = 360
  Axis = (0,1,0)
  Base = (0,0,0)
  FaceMakerClass = Part::FaceMakerBullseye
  Placement = pos=(0,0,0) rot=(0,0,1;1.5708rad)
  Solid = false
  Source = -> Face024
  Symmetric = false
FEATURE [Part::Feature] Face025
  shape: bbox 9.8 x 26.5 x 2e-07 mm, 1 faces, 0 solids (baked)
FEATURE [Part::Revolution] Revolve025
  Angle = 360
  Axis = (0,1,0)
  Base = (0,0,0)
  FaceMakerClass = Part::FaceMakerBullseye
  Placement = pos=(0,0,0) rot=(0,0,1;1.5708rad)
  Solid = false
  Source = -> Face025
  Symmetric = false
FEATURE [Part::MultiFuse] Fusion033
  Placement = pos=(-18,19,36) rot=(0,0,1;0rad)
  Shapes = -> [Revolve025,Revolve024]
FEATURE [Part::Cylinder] Cylinder014
  Angle = 360
  AttacherType = Attacher::AttachEngine3D
  Height = 20
  Placement = pos=(0,0,36.15) rot=(0,0,1;0rad)
  Radius = 14.3
FEATURE [Part::Cylinder] Cylinder015
  Angle = 360
  AttacherType = Attacher::AttachEngine3D
  Height = 10
  Placement = pos=(0,0,36.15) rot=(0,0,1;0rad)
  Radius = 4
FEATURE [Part::MultiFuse] Fusion034  label="removeToCreteHoleForPlugHousing004"
  Placement = pos=(-42,19,36) rot=(0,1,0;1.5708rad)
  Shapes = -> [Cylinder014,Cylinder015]
FEATURE [Part::Cut] Cut008  label="top004"
  Base = -> Cut004
  Placement = pos=(-1,0,0) rot=(0,0,1;0rad)
  Tool = -> Fusion034
FEATURE [Part::Box] Box005  label="Cube005"
  AttacherType = Attacher::AttachEngine3D
  Height = 28
  Length = 3
  Placement = pos=(110.7,19,22) rot=(0,0,1;0rad)
  Width = 15.7
FEATURE [Part::Cylinder] Cylinder016
  Angle = 360
  AttacherType = Attacher::AttachEngine3D
  Height = 10
  Placement = pos=(0,0,36.15) rot=(0,0,1;0rad)
  Radius = 4
FEATURE [Part::Cylinder] Cylinder017
  Angle = 360
  AttacherType = Attacher::AttachEngine3D
  Height = 20
  Placement = pos=(0,0,36.15) rot=(0,0,1;0rad)
  Radius = 10.3
FEATURE [Part::MultiFuse] Fusion035  label="removeToCreteHoleForPlugHousing005"
  Placement = pos=(70,19,36) rot=(0,1,0;1.5708rad)
  Shapes = -> [Cylinder017,Cylinder016]
FEATURE [Part::Cut] Cut009  label="plugHousingTab001"
  Base = -> Box005
  Placement = pos=(-107.4,-14,0) rot=(0,0,1;0rad)
  Tool = -> Fusion035
FEATURE [Part::Box] Box006  label="Cube006"
  AttacherType = Attacher::AttachEngine3D
  Height = 28
  Length = 3
  Placement = pos=(110.7,19,22) rot=(0,0,1;0rad)
  Width = 15.7
FEATURE [Part::Cylinder] Cylinder018
  Angle = 360
  AttacherType = Attacher::AttachEngine3D
  Height = 10
  Placement = pos=(0,0,36.15) rot=(0,0,1;0rad)
  Radius = 4
FEATURE [Part::Cylinder] Cylinder019
  Angle = 360
  AttacherType = Attacher::AttachEngine3D
  Height = 20
  Placement = pos=(0,0,36.15) rot=(0,0,1;0rad)
  Radius = 10.3
FEATURE [Part::MultiFuse] Fusion036  label="removeToCreteHoleForPlugHousing006"
  Placement = pos=(70,19,36) rot=(0,1,0;1.5708rad)
  Shapes = -> [Cylinder019,Cylinder018]
FEATURE [Part::Cut] Cut010  label="plugHousingTab002"
  Base = -> Box006
  Placement = pos=(-107.4,-14,0) rot=(0,0,1;0rad)
  Tool = -> Fusion036
FEATURE [Part::MultiFuse] Fusion037
  Placement = pos=(9.6,23,0) rot=(0,0,1;3.14159rad)
  Shapes = -> [Cut009,Cut010]
FEATURE [Part::Box] Box  label="Cube"
  AttacherType = Attacher::AttachEngine3D
  Height = 10
  Length = 3
  Placement = pos=(3.3,4,12) rot=(0,0,1;0rad)
  Width = 10
FEATURE [Part::Fillet] Fillet004
  Base = -> Fusion028
  Edges = 1 edges r=2: [Edge25]
FEATURE [Part::Fillet] Fillet005  label="plugHousing046"
  Base = -> Fillet004
  Edges = 1 edges r=2: [Edge8]
FEATURE [Part::Fillet] Fillet006
  Base = -> Box
  Edges = 1 edges r=2: [Edge11]
FEATURE [Part::Box] Box007  label="Cube007"
  AttacherType = Attacher::AttachEngine3D
  Height = 10
  Length = 3
  Placement = pos=(3.3,4,50) rot=(0,0,1;0rad)
  Width = 10
FEATURE [Part::Fillet] Fillet007
  Base = -> Box007
  Edges = 1 edges r=2: [Edge12]
FEATURE [Part::Box] Box008  label="Cube008"
  AttacherType = Attacher::AttachEngine3D
  Height = 28
  Length = 4
  Placement = pos=(5,0,22) rot=(0,0,1;0rad)
  Width = 10
FEATURE [Part::Fillet] Fillet008
  Base = -> Box008
  Edges = 1 edges r=1: [Edge7]
FEATURE [Part::Fillet] Fillet009
  Base = -> Fillet008
  Edges = 1 edges r=2: [Edge5]
FEATURE [Part::Fillet] Fillet010
  Base = -> Fillet009
  Edges = 1 edges r=2: [Edge2]
FEATURE [Sketcher::SketchObject] Sketch009  label="topSketch003"
  FullyConstrained = true
  sketch-geometry (4):
    g0: LineSegment StartX=16.8446 StartY=31.512 StartZ=0 EndX=16.3251 EndY=34.4666 EndZ=0
    g1: ArcOfCircle CenterX=19 CenterY=19.2524 CenterZ=0 NormalX=0 NormalY=0 NormalZ=1 AngleXU=0 Radius=15.4476 StartAngle=1.74483 EndAngle=2.72717
    g2: ArcOfCircle CenterX=19 CenterY=19.2524 CenterZ=0 NormalX=0 NormalY=0 NormalZ=1 AngleXU=0 Radius=12.4476 StartAngle=1.74483 EndAngle=2.73189
    g3: LineSegment StartX=4.86004 StartY=25.4725 StartZ=0 EndX=7.58253 EndY=24.2107 EndZ=0
  constraints (7):
    c: Block(g0)
    c: Coincident(g1,g0)
    c: Coincident(g2,g0)
    c: Coincident(g3,g1)
    c: Coincident(g3,g2)
    c: Block(g1)
    c: Block(g2)
FEATURE [Part::Extrusion] Extrude008
  Base = -> Sketch009
  Dir = (0,0,1)
  DirMode = 2
  FaceMakerClass = Part::FaceMakerBullseye
  LengthFwd = 10
  LengthRev = 0
  Placement = pos=(0,0,31) rot=(0,0,1;0rad)
  Solid = true
  Symmetric = false
FEATURE [Part::Cylinder] Cylinder020
  Angle = 360
  AttacherType = Attacher::AttachEngine3D
  Height = 20
  Placement = pos=(0,0,36.15) rot=(0,0,1;0rad)
  Radius = 8.2
FEATURE [Part::Cylinder] Cylinder021
  Angle = 360
  AttacherType = Attacher::AttachEngine3D
  Height = 10
  Placement = pos=(0,0,36.15) rot=(0,0,1;0rad)
  Radius = 4
FEATURE [Part::MultiFuse] Fusion038  label="removeToCreteHoleForPlugHousing007"
  Placement = pos=(-42,19,36) rot=(0,1,0;1.5708rad)
  Shapes = -> [Cylinder020,Cylinder021]
FEATURE [Part::Cut] Cut011
  Base = -> Extrude008
  Tool = -> Fusion038
FEATURE [Part::Fillet] Fillet011
  Base = -> Cut011
  Edges = 1 edges r=2: [Edge1]
FEATURE [Part::Fillet] Fillet012
  Base = -> Fillet011
  Edges = 1 edges r=2.5: [Edge1]
FEATURE [Part::Fillet] Fillet013
  Base = -> Fillet012
  Edges = 1 edges r=2.5: [Edge2]
FEATURE [Part::Box] Box010  label="Cube010"
  AttacherType = Attacher::AttachEngine3D
  Height = 16
  Length = 8
  Placement = pos=(12.7,31.52,28) rot=(0,0,1;0rad)
  Width = 4
FEATURE [Sketcher::SketchObject] Sketch010  label="topSketch004"
  FullyConstrained = true
  sketch-geometry (4):
    g0: LineSegment StartX=16.8446 StartY=31.512 StartZ=0 EndX=16.3251 EndY=34.4666 EndZ=0
    g1: ArcOfCircle CenterX=19 CenterY=19.2524 CenterZ=0 NormalX=0 NormalY=0 NormalZ=1 AngleXU=0 Radius=15.4476 StartAngle=1.74483 EndAngle=2.72717
    g2: ArcOfCircle CenterX=19 CenterY=19.2524 CenterZ=0 NormalX=0 NormalY=0 NormalZ=1 AngleXU=0 Radius=12.4476 StartAngle=1.74483 EndAngle=2.73189
    g3: LineSegment StartX=4.86004 StartY=25.4725 StartZ=0 EndX=7.58253 EndY=24.2107 EndZ=0
  constraints (7):
    c: Block(g0)
    c: Coincident(g1,g0)
    c: Coincident(g2,g0)
    c: Coincident(g3,g1)
    c: Coincident(g3,g2)
    c: Block(g1)
    c: Block(g2)
FEATURE [Part::Cylinder] Cylinder022
  Angle = 360
  AttacherType = Attacher::AttachEngine3D
  Height = 10
  Placement = pos=(0,0,36.15) rot=(0,0,1;0rad)
  Radius = 4
FEATURE [Sketcher::SketchObject] Sketch011  label="topSketch005"
  FullyConstrained = true
  sketch-geometry (4):
    g0: LineSegment StartX=16.8446 StartY=31.512 StartZ=0 EndX=16.3251 EndY=34.4666 EndZ=0
    g1: ArcOfCircle CenterX=19 CenterY=19.2524 CenterZ=0 NormalX=0 NormalY=0 NormalZ=1 AngleXU=0 Radius=15.4476 StartAngle=1.74483 EndAngle=2.72717
    g2: ArcOfCircle CenterX=19 CenterY=19.2524 CenterZ=0 NormalX=0 NormalY=0 NormalZ=1 AngleXU=0 Radius=12.4476 StartAngle=1.74483 EndAngle=2.73189
    g3: LineSegment StartX=4.86004 StartY=25.4725 StartZ=0 EndX=7.58253 EndY=24.2107 EndZ=0
  constraints (7):
    c: Block(g0)
    c: Coincident(g1,g0)
    c: Coincident(g2,g0)
    c: Coincident(g3,g1)
    c: Coincident(g3,g2)
    c: Block(g1)
    c: Block(g2)
FEATURE [Part::Extrusion] Extrude010
  Base = -> Sketch011
  Dir = (0,0,1)
  DirMode = 2
  FaceMakerClass = Part::FaceMakerBullseye
  LengthFwd = 10.6
  LengthRev = 0
  Placement = pos=(0,0,31) rot=(0,0,1;0rad)
  Solid = true
  Symmetric = false
FEATURE [Part::Cylinder] Cylinder023
  Angle = 360
  AttacherType = Attacher::AttachEngine3D
  Height = 20
  Placement = pos=(0,0,36.15) rot=(0,0,1;0rad)
  Radius = 8.2
FEATURE [Part::MultiFuse] Fusion039  label="removeToCreteHoleForPlugHousing008"
  Placement = pos=(-42,19,36) rot=(0,1,0;1.5708rad)
  Shapes = -> [Cylinder023,Cylinder022]
FEATURE [Part::Cut] Cut012
  Base = -> Extrude010
  Placement = pos=(0,0,-0.3) rot=(0,0,1;0rad)
  Tool = -> Fusion039
FEATURE [Part::Cut] Cut013
  Base = -> Box010
  Tool = -> Cut012
FEATURE [Part::Fillet] Fillet014
  Base = -> Cut013
  Edges = 1 edges r=0.7: [Edge13]
FEATURE [Part::Fillet] Fillet015
  Base = -> Fillet014
  Edges = 1 edges r=0.7: [Edge13]
FEATURE [Part::Fillet] Fillet016
  Base = -> Fillet015
  Edges = 1 edges r=0.7: [Edge16]
FEATURE [Part::Fillet] Fillet017
  Base = -> Fillet016
  Edges = 1 edges r=0.7: [Edge11]
FEATURE [Part::Fillet] Fillet018
  Base = -> Fillet017
  Edges = 1 edges r=0.7: [Edge10]
FEATURE [Part::Fillet] Fillet019
  Base = -> Fillet018
  Edges = 1 edges r=1.2: [Edge5]
FEATURE [Part::Fillet] Fillet020
  Base = -> Fillet019
  Edges = 1 edges r=1.2: [Edge12]
FEATURE [Part::Fillet] Fillet021
  Base = -> Fillet020
  Edges = 1 edges r=2: [Edge1]
  Placement = pos=(0.3,0,0) rot=(0,0,1;0rad)
FEATURE [Part::MultiFuse] Fusion040  label="top005"
  Shapes = -> [Cut008,Fillet021]
FEATURE [Part::MultiFuse] Fusion041  label="wireHolder"
  Shapes = -> [Fusion033,Fillet013]
FEATURE [Part::MultiFuse] Fusion042
  Shapes = -> [Fillet007,Fusion041]
FEATURE [Part::MultiFuse] Fusion043  label="wireHolder001"
  Shapes = -> [Fusion042,Fillet010]
FEATURE [Part::MultiFuse] Fusion044  label="wireHolder002"
  Shapes = -> [Fillet006,Fusion037,Fusion043]
FEATURE [Part::Feature] Face026
  shape: bbox 11 x 6 x 2e-07 mm, 1 faces, 0 solids (baked)
FEATURE [Part::Revolution] Revolve026
  Angle = 360
  Axis = (0,1,0)
  Base = (0,0,0)
  FaceMakerClass = Part::FaceMakerBullseye
  Placement = pos=(30.3,-1,19.7) rot=(0,0,1;0rad)
  Solid = false
  Source = -> Face026
  Symmetric = false
FEATURE [Sketcher::SketchObject] Sketch013  label="topSketch006"
  FullyConstrained = true
  sketch-geometry (13):
    g0: LineSegment StartX=117 StartY=19 StartZ=0 EndX=117 EndY=38 EndZ=0
    g1: ArcOfCircle CenterX=98 CenterY=19 CenterZ=0 NormalX=0 NormalY=0 NormalZ=1 AngleXU=0 Radius=19 StartAngle=5.7297 EndAngle=6.28319
    g2: LineSegment StartX=0 StartY=3 StartZ=0 EndX=0 EndY=19 EndZ=0
    g3: LineSegment StartX=19 StartY=38 StartZ=0 EndX=117 EndY=38 EndZ=0
    g4: ArcOfCircle CenterX=19 CenterY=19 CenterZ=0 NormalX=0 NormalY=0 NormalZ=1 AngleXU=0 Radius=19 StartAngle=1.5708 EndAngle=3.14159
    g5: ArcOfCircle CenterX=19 CenterY=19 CenterZ=0 NormalX=0 NormalY=0 NormalZ=1 AngleXU=0 Radius=16 StartAngle=1.5708 EndAngle=3.14159
    g6: ArcOfCircle CenterX=98 CenterY=19 CenterZ=0 NormalX=0 NormalY=0 NormalZ=1 AngleXU=0 Radius=16 StartAngle=5.60905 EndAngle=6.28319
    g7: LineSegment StartX=114 StartY=19 StartZ=0 EndX=114 EndY=35 EndZ=0
    g8: LineSegment StartX=110.5 StartY=9.01251 StartZ=0 EndX=114.163 EndY=9.01251 EndZ=0
    g9: LineSegment StartX=114 StartY=35 StartZ=0 EndX=19 EndY=35 EndZ=0
    g10: LineSegment StartX=0 StartY=3 StartZ=0 EndX=0 EndY=0 EndZ=0
    g11: LineSegment StartX=3 StartY=0 StartZ=0 EndX=0 EndY=0 EndZ=0
    g12: LineSegment StartX=3 StartY=19 StartZ=0 EndX=3 EndY=0 EndZ=0
  constraints (33):
    c: Vertical(g0)
    c: Distance(g0) = 19
    c: Block(g0)
    c: Coincident(g1,g0)
    c: Block(g1)
    c: Vertical(g2)
    c: Block(g2)
    c: Coincident(g3,g0)
    c: Horizontal(g3)
    c: Distance(g3) = 98
    c: Coincident(g4,g3)
    c: Coincident(g4,g2)
    c: Block(g4)
    c: Coincident(g5,g4)
    c: Coincident(g6,g1)
    c: Block(g6)
    c: Block(g5)
    c: Coincident(g7,g6)
    c: Vertical(g7)
    c: Coincident(g8,g6)
    c: Coincident(g8,g1)
    c: Coincident(g9,g7)
    c: Coincident(g9,g5)
    c: Horizontal(g9)
    c: Tangent(g9,g5)
    c: Coincident(g10,g2)
    c: Distance(g10) = 3
    c: Vertical(g10)
    c: Coincident(g11,g10)
    c: Horizontal(g11)
    c: Coincident(g12,g5)
    c: Coincident(g12,g11)
    c: Vertical(g12)
FEATURE [Part::Extrusion] Extrude011  label="top006"
  Base = -> Sketch013
  Dir = (0,0,1)
  DirMode = 2
  FaceMakerClass = Part::FaceMakerBullseye
  LengthFwd = 72
  LengthRev = 0
  Solid = true
  Symmetric = false
FEATURE [Sketcher::SketchObject] Sketch014
  FullyConstrained = true
  MapMode = 3
  Placement = pos=(0,0,0) rot=(1,0,0;1.5708rad)
  Support = -> [Extrude011]
  sketch-geometry (8):
    g0: Circle CenterX=80.351 CenterY=-67.6202 CenterZ=0 NormalX=0 NormalY=0 NormalZ=1 AngleXU=0 Radius=2
    g1: Circle CenterX=80.351 CenterY=-67.6202 CenterZ=0 NormalX=0 NormalY=0 NormalZ=1 AngleXU=0 Radius=3
    g2: Circle CenterX=80.351 CenterY=-4.92017 CenterZ=0 NormalX=0 NormalY=0 NormalZ=1 AngleXU=0 Radius=2
    g3: Circle CenterX=80.351 CenterY=-4.92017 CenterZ=0 NormalX=0 NormalY=0 NormalZ=1 AngleXU=0 Radius=3
    g4: Circle CenterX=23.851 CenterY=-4.92017 CenterZ=0 NormalX=0 NormalY=0 NormalZ=1 AngleXU=0 Radius=2
    g5: Circle CenterX=23.851 CenterY=-4.92017 CenterZ=0 NormalX=0 NormalY=0 NormalZ=1 AngleXU=0 Radius=3
    g6: Circle CenterX=23.851 CenterY=-67.6202 CenterZ=0 NormalX=0 NormalY=0 NormalZ=1 AngleXU=0 Radius=2
    g7: Circle CenterX=23.851 CenterY=-67.6202 CenterZ=0 NormalX=0 NormalY=0 NormalZ=1 AngleXU=0 Radius=3
  constraints (8):
    c: Block(g3)
    c: Block(g2)
    c: Block(g1)
    c: Block(g0)
    c: Block(g6)
    c: Block(g7)
    c: Block(g4)
    c: Block(g5)
FEATURE [Part::Feature] Face027
  shape: bbox 11 x 6 x 2e-07 mm, 1 faces, 0 solids (baked)
FEATURE [Part::Revolution] Revolve027
  Angle = 360
  Axis = (0,1,0)
  Base = (0,0,0)
  FaceMakerClass = Part::FaceMakerBullseye
  Placement = pos=(30.3,-1,51.7) rot=(0,0,1;0rad)
  Solid = false
  Source = -> Face027
  Symmetric = false
FEATURE [Part::Feature] Face028
  shape: bbox 11 x 6 x 2e-07 mm, 1 faces, 0 solids (baked)
FEATURE [Part::Revolution] Revolve028
  Angle = 360
  Axis = (0,1,0)
  Base = (0,0,0)
  FaceMakerClass = Part::FaceMakerBullseye
  Placement = pos=(62.3,-1,19.7) rot=(0,0,1;0rad)
  Solid = false
  Source = -> Face028
  Symmetric = false
FEATURE [Part::Feature] Face029
  shape: bbox 11 x 6 x 2e-07 mm, 1 faces, 0 solids (baked)
FEATURE [Part::Revolution] Revolve029
  Angle = 360
  Axis = (0,1,0)
  Base = (0,0,0)
  FaceMakerClass = Part::FaceMakerBullseye
  Placement = pos=(62.3,-1,51.7) rot=(0,0,1;0rad)
  Solid = false
  Source = -> Face029
  Symmetric = false
FEATURE [Part::Feature] Wire
  shape: bbox 11 x 5.2 x 2e-07 mm, 0 faces, 0 solids (baked)
FEATURE [Part::Revolution] Revolve030
  Angle = 360
  Axis = (0,1,0)
  Base = (0,0,0)
  FaceMakerClass = Part::FaceMakerBullseye
  Placement = pos=(30.3,38,19.7) rot=(0,0,1;0rad)
  Solid = true
  Source = -> Wire
  Symmetric = false
FEATURE [Part::Feature] Wire001
  shape: bbox 11 x 5.2 x 2e-07 mm, 0 faces, 0 solids (baked)
FEATURE [Part::Revolution] Revolve031
  Angle = 360
  Axis = (0,1,0)
  Base = (0,0,0)
  FaceMakerClass = Part::FaceMakerBullseye
  Placement = pos=(30.3,38,51.7) rot=(0,0,1;0rad)
  Solid = true
  Source = -> Wire001
  Symmetric = false
FEATURE [Part::Feature] Wire002
  shape: bbox 11 x 5.2 x 2e-07 mm, 0 faces, 0 solids (baked)
FEATURE [Part::Revolution] Revolve032
  Angle = 360
  Axis = (0,1,0)
  Base = (0,0,0)
  FaceMakerClass = Part::FaceMakerBullseye
  Placement = pos=(62.3,38,51.7) rot=(0,0,1;0rad)
  Solid = true
  Source = -> Wire002
  Symmetric = false
FEATURE [Part::Feature] Wire003
  shape: bbox 11 x 5.2 x 2e-07 mm, 0 faces, 0 solids (baked)
FEATURE [Part::Revolution] Revolve033
  Angle = 360
  Axis = (0,1,0)
  Base = (0,0,0)
  FaceMakerClass = Part::FaceMakerBullseye
  Placement = pos=(62.3,38,19.7) rot=(0,0,1;0rad)
  Solid = true
  Source = -> Wire003
  Symmetric = false
FEATURE [Part::MultiFuse] Fusion045  label="altRandScrewHousing"
  Shapes = -> [Revolve029,Revolve027,Revolve028,Revolve026]
FEATURE [Part::MultiFuse] Fusion046  label="fanScrewHousing"
  Shapes = -> [Revolve033,Revolve032,Revolve031,Revolve030]
FEATURE [Sketcher::SketchObject] Sketch015
  FullyConstrained = true
  sketch-geometry (17):
    g0: Circle CenterX=-3.5 CenterY=23.5 CenterZ=0 NormalX=0 NormalY=0 NormalZ=1 AngleXU=0 Radius=1
    g1: Circle CenterX=-1 CenterY=15.25 CenterZ=0 NormalX=0 NormalY=0 NormalZ=1 AngleXU=0 Radius=1
    g2: Circle CenterX=-3.5 CenterY=7 CenterZ=0 NormalX=0 NormalY=0 NormalZ=1 AngleXU=0 Radius=1
    g3: BSplineCurve PolesCount=3 KnotsCount=2 Degree=2 IsPeriodic=0
    g4: GeomPoint X=-3.5 Y=23.5 Z=0
    g5: GeomPoint X=-3.5 Y=7 Z=0
    g6: Circle CenterX=-4.8 CenterY=30.5 CenterZ=0 NormalX=0 NormalY=0 NormalZ=1 AngleXU=0 Radius=1
    g7: Circle CenterX=-3.5 CenterY=30.5 CenterZ=0 NormalX=0 NormalY=0 NormalZ=1 AngleXU=0 Radius=1
    g8: Circle CenterX=-3.5 CenterY=29.2 CenterZ=0 NormalX=0 NormalY=0 NormalZ=1 AngleXU=0 Radius=1
    g9: BSplineCurve PolesCount=3 KnotsCount=2 Degree=2 IsPeriodic=0
    g10: GeomPoint X=-4.8 Y=30.5 Z=0
    g11: GeomPoint X=-3.5 Y=29.2 Z=0
    g12: LineSegment StartX=-3.5 StartY=29.2 StartZ=0 EndX=-3.5 EndY=23.5 EndZ=0
    g13: LineSegment StartX=-4.8 StartY=30.5 StartZ=0 EndX=0 EndY=30.5 EndZ=0
    g14: LineSegment StartX=-3.5 StartY=0.3 StartZ=0 EndX=0 EndY=0.3 EndZ=0
    g15: LineSegment StartX=-3.5 StartY=0.3 StartZ=0 EndX=-3.5 EndY=7 EndZ=0
    g16: LineSegment StartX=0 StartY=0.3 StartZ=0 EndX=0 EndY=30.5 EndZ=0
  constraints (33):
    c: Weight(g0) = 1
    c: Equal(g0,g1)
    c: Equal(g0,g2)
    c: InternalAlignment(g0,g3)
    c: InternalAlignment(g1,g3)
    c: InternalAlignment(g2,g3)
    c: InternalAlignment(g4,g3)
    c: InternalAlignment(g5,g3)
    c: Block(g3)
    c: Weight(g6) = 1
    c: Equal(g6,g7)
    c: Equal(g6,g8)
    c: InternalAlignment(g6,g9)
    c: InternalAlignment(g7,g9)
    c: InternalAlignment(g8,g9)
    c: InternalAlignment(g10,g9)
    c: InternalAlignment(g11,g9)
    c: Block(g9)
    c: Coincident(g12,g9)
    c: Coincident(g12,g3)
    c: Vertical(g12)
    c: Coincident(g13,g9)
    c: Horizontal(g13)
    c: Distance(g13) = 4.8
    c: Horizontal(g14)
    c: Block(g14)
    c: Coincident(g15,g14)
    c: Coincident(g15,g3)
    c: Vertical(g15)
    c: Coincident(g16,g14)
    c: Coincident(g16,g13)
    c: Vertical(g16)
    c: Tangent(g16,g1)
FEATURE [Sketcher::SketchObject] Sketch016
  FullyConstrained = true
  sketch-geometry (16):
    g0: Circle CenterX=-3.5 CenterY=23.5 CenterZ=0 NormalX=0 NormalY=0 NormalZ=1 AngleXU=0 Radius=1
    g1: Circle CenterX=-1 CenterY=15.25 CenterZ=0 NormalX=0 NormalY=0 NormalZ=1 AngleXU=0 Radius=1
    g2: Circle CenterX=-3.5 CenterY=7 CenterZ=0 NormalX=0 NormalY=0 NormalZ=1 AngleXU=0 Radius=1
    g3: BSplineCurve PolesCount=3 KnotsCount=2 Degree=2 IsPeriodic=0
    g4: GeomPoint X=-3.5 Y=23.5 Z=0
    g5: GeomPoint X=-3.5 Y=7 Z=0
    g6: LineSegment StartX=-3.5 StartY=28.2 StartZ=0 EndX=-3.5 EndY=23.5 EndZ=0
    g7: LineSegment StartX=0 StartY=29.5 StartZ=0 EndX=0 EndY=30 EndZ=0
    g8: LineSegment StartX=-3.5 StartY=28.2 StartZ=0 EndX=-3.5 EndY=30 EndZ=0
    g9: LineSegment StartX=0 StartY=30 StartZ=0 EndX=0 EndY=30.5 EndZ=0
    g10: LineSegment StartX=0 StartY=30.5 StartZ=0 EndX=-3.5 EndY=30.5 EndZ=0
    g11: LineSegment StartX=-3.5 StartY=30.5 StartZ=0 EndX=-3.5 EndY=30 EndZ=0
    g12: LineSegment StartX=0 StartY=29.5 StartZ=0 EndX=0 EndY=5 EndZ=0
    g13: LineSegment StartX=-3.5 StartY=0.3 StartZ=0 EndX=-3.5 EndY=7 EndZ=0
    g14: LineSegment StartX=-3.5 StartY=0.3 StartZ=0 EndX=0 EndY=0.3 EndZ=0
    g15: LineSegment StartX=0 StartY=5 StartZ=0 EndX=0 EndY=0.3 EndZ=0
  constraints (39):
    c: Weight(g0) = 1
    c: Equal(g0,g1)
    c: Equal(g0,g2)
    c: InternalAlignment(g0,g3)
    c: InternalAlignment(g1,g3)
    c: InternalAlignment(g2,g3)
    c: InternalAlignment(g4,g3)
    c: InternalAlignment(g5,g3)
    c: Block(g3)
    c: Coincident(g6,g3)
    c: Vertical(g6)
    c: Vertical(g7)
    c: Distance(g7) = 0.5
    c: Coincident(g8,g6)
    c: Vertical(g8)
    c: Block(g6)
    c: Block(g7)
    c: Vertical(g9)
    c: Equal(g7,g9) = 0.5
    c: Block(g9)
    c: Coincident(g9,g7)
    c: Horizontal(g10)
    c: Coincident(g10,g9)
    c: Coincident(g11,g10)
    c: Coincident(g11,g8)
    c: Vertical(g11)
    c: Block(g11)
    c: Coincident(g12,g7)
    c: Vertical(g12)
    c: Coincident(g13,g3)
    c: Vertical(g13)
    c: Distance(g13) = 6.7
    c: Coincident(g14,g13)
    c: Horizontal(g14)
    c: Block(g14)
    c: Coincident(g15,g12)
    c: Coincident(g15,g14)
    c: Vertical(g15)
    c: Block(g15)
FEATURE [Sketcher::SketchObject] Sketch017
  FullyConstrained = true
  sketch-geometry (11):
    g0: LineSegment StartX=-3.5 StartY=1e-16 StartZ=0 EndX=-1.6 EndY=1e-16 EndZ=0
    g1: LineSegment StartX=-1.6 StartY=1e-16 StartZ=0 EndX=-1.6 EndY=1.5 EndZ=0
    g2: LineSegment StartX=-3.5 StartY=1.5 StartZ=0 EndX=-1.6 EndY=1.5 EndZ=0
    g3: LineSegment StartX=-3.5 StartY=1e-16 StartZ=0 EndX=-4.8 EndY=1e-16 EndZ=0
    g4: Circle CenterX=-3.5 CenterY=1.3 CenterZ=0 NormalX=0 NormalY=0 NormalZ=1 AngleXU=0 Radius=1
    g5: Circle CenterX=-3.5 CenterY=1e-16 CenterZ=0 NormalX=0 NormalY=0 NormalZ=1 AngleXU=0 Radius=1
    g6: Circle CenterX=-4.8 CenterY=1e-16 CenterZ=0 NormalX=0 NormalY=0 NormalZ=1 AngleXU=0 Radius=1
    g7: BSplineCurve PolesCount=3 KnotsCount=2 Degree=2 IsPeriodic=0
    g8: GeomPoint X=-3.5 Y=1.3 Z=0
    g9: GeomPoint X=-4.8 Y=1e-16 Z=0
    g10: LineSegment StartX=-3.5 StartY=1.3 StartZ=0 EndX=-3.5 EndY=1.5 EndZ=0
  constraints (24):
    c: Horizontal(g0)
    c: Distance(g0) = 1.9
    c: Block(g0)
    c: Coincident(g1,g0)
    c: Vertical(g1)
    c: Coincident(g2,g1)
    c: Horizontal(g2)
    c: Coincident(g3,g0)
    c: Horizontal(g3)
    c: Distance(g3) = 1.3
    c: Weight(g4) = 1
    c: Equal(g4,g5)
    c: Coincident(g5,g0)
    c: Equal(g4,g6)
    c: Coincident(g7,g3)
    c: InternalAlignment(g4,g7)
    c: InternalAlignment(g5,g7)
    c: InternalAlignment(g6,g7)
    c: InternalAlignment(g8,g7)
    c: InternalAlignment(g9,g7)
    c: Coincident(g10,g7)
    c: Coincident(g10,g2)
    c: Vertical(g10)
    c: Block(g10)
FEATURE [Part::Feature] Face035
  shape: bbox 3.2 x 1.5 x 2e-07 mm, 1 faces, 0 solids (baked)
FEATURE [Part::Revolution] Revolve039  label="backCaseScrewRetainer"
  Angle = 360
  Axis = (0,1,0)
  Base = (0,0,0)
  FaceMakerClass = Part::FaceMakerBullseye
  Placement = pos=(12.5,3,62) rot=(0,0,1;0rad)
  Solid = false
  Source = -> Face035
  Symmetric = false
FEATURE [Part::Feature] Face036
  shape: bbox 3.2 x 1.5 x 2e-07 mm, 1 faces, 0 solids (baked)
FEATURE [Part::Feature] Face039
  shape: bbox 4.8 x 30.2 x 2e-07 mm, 1 faces, 0 solids (baked)
FEATURE [Part::Revolution] Revolve043  label="frontCaseScrewPost002"
  Angle = 360
  Axis = (0,1,0)
  Base = (0,0,0)
  FaceMakerClass = Part::FaceMakerBullseye
  Placement = pos=(89.5,4.5,3.5) rot=(0,0,1;0rad)
  Solid = false
  Source = -> Face039
  Symmetric = false
FEATURE [Part::Feature] Face042
  shape: bbox 4.8 x 30.2 x 2e-07 mm, 1 faces, 0 solids (baked)
FEATURE [Part::Revolution] Revolve046  label="frontCaseScrewPost003"
  Angle = 360
  Axis = (0,1,0)
  Base = (0,0,0)
  FaceMakerClass = Part::FaceMakerBullseye
  Placement = pos=(89.5,4.5,68.5) rot=(0,0,1;0rad)
  Solid = false
  Source = -> Face042
  Symmetric = false
FEATURE [Part::Feature] Face043
  shape: bbox 3.2 x 1.5 x 2e-07 mm, 1 faces, 0 solids (baked)
FEATURE [Part::Revolution] Revolve047  label="frontCaseScrewRetainer002"
  Angle = 360
  Axis = (0,1,0)
  Base = (0,0,0)
  FaceMakerClass = Part::FaceMakerBullseye
  Placement = pos=(89.5,3,68.5) rot=(0,0,1;0rad)
  Solid = false
  Source = -> Face043
  Symmetric = false
FEATURE [Part::Feature] Face044
  shape: bbox 3.2 x 1.5 x 2e-07 mm, 1 faces, 0 solids (baked)
FEATURE [Part::Revolution] Revolve048  label="frontCaseScrewRetainer003"
  Angle = 360
  Axis = (0,1,0)
  Base = (0,0,0)
  FaceMakerClass = Part::FaceMakerBullseye
  Placement = pos=(89.5,3,3.5) rot=(0,0,1;0rad)
  Solid = false
  Source = -> Face044
  Symmetric = false
FEATURE [App::MeasureDistance] Distance002  label="Distance: 1.67 mm"
  Distance = 1.66921
  P1 = (99.2361,4.7524,71.7)
  P2 = (99.2347,6.42161,71.7)
FEATURE [Sketcher::SketchObject] Sketch018
  FullyConstrained = true
  sketch-geometry (7):
    g0: LineSegment StartX=0 StartY=0 StartZ=0 EndX=0 EndY=6 EndZ=0
    g1: Circle CenterX=0 CenterY=0 CenterZ=0 NormalX=0 NormalY=0 NormalZ=1 AngleXU=0 Radius=1
    g2: Circle CenterX=8 CenterY=6 CenterZ=0 NormalX=0 NormalY=0 NormalZ=1 AngleXU=0 Radius=1
    g3: BSplineCurve PolesCount=3 KnotsCount=2 Degree=2 IsPeriodic=0
    g4: GeomPoint X=0 Y=0 Z=0
    g5: GeomPoint X=8 Y=6 Z=0
    g6: LineSegment StartX=0 StartY=6 StartZ=0 EndX=8 EndY=6 EndZ=0
  constraints (14):
    c: Coincident(g0,g-1)
    c: Distance(g0) = 6
    c: Vertical(g0)
    c: Coincident(g3,g0)
    c: Weight(g1) = 1
    c: Equal(g1,g2)
    c: InternalAlignment(g1,g3)
    c: InternalAlignment(g2,g3)
    c: InternalAlignment(g4,g3)
    c: InternalAlignment(g5,g3)
    c: Block(g3)
    c: Coincident(g6,g0)
    c: Coincident(g6,g3)
    c: Horizontal(g6)
FEATURE [Part::Extrusion] Extrude012  label="caseScrewPillarBracket"
  Base = -> Sketch018
  Dir = (0,0,1)
  DirMode = 2
  FaceMakerClass = Part::FaceMakerBullseye
  LengthFwd = 2.4
  LengthRev = 0
  Placement = pos=(15.76,29,8.8) rot=(0,1,0;0rad)
  Solid = true
  Symmetric = false
FEATURE [Sketcher::SketchObject] Sketch019
  FullyConstrained = true
  sketch-geometry (7):
    g0: LineSegment StartX=0 StartY=0 StartZ=0 EndX=0 EndY=6 EndZ=0
    g1: Circle CenterX=0 CenterY=0 CenterZ=0 NormalX=0 NormalY=0 NormalZ=1 AngleXU=0 Radius=1
    g2: Circle CenterX=8 CenterY=6 CenterZ=0 NormalX=0 NormalY=0 NormalZ=1 AngleXU=0 Radius=1
    g3: BSplineCurve PolesCount=3 KnotsCount=2 Degree=2 IsPeriodic=0
    g4: GeomPoint X=0 Y=0 Z=0
    g5: GeomPoint X=8 Y=6 Z=0
    g6: LineSegment StartX=0 StartY=6 StartZ=0 EndX=8 EndY=6 EndZ=0
  constraints (14):
    c: Coincident(g0,g-1)
    c: Distance(g0) = 6
    c: Vertical(g0)
    c: Coincident(g3,g0)
    c: Weight(g1) = 1
    c: Equal(g1,g2)
    c: InternalAlignment(g1,g3)
    c: InternalAlignment(g2,g3)
    c: InternalAlignment(g4,g3)
    c: InternalAlignment(g5,g3)
    c: Block(g3)
    c: Coincident(g6,g0)
    c: Coincident(g6,g3)
    c: Horizontal(g6)
FEATURE [Part::Extrusion] Extrude013  label="caseScrewPillarBracket001"
  Base = -> Sketch019
  Dir = (0,0,1)
  DirMode = 2
  FaceMakerClass = Part::FaceMakerBullseye
  LengthFwd = 2.4
  LengthRev = 0
  Placement = pos=(15.76,29,60.8) rot=(0,0,1;0rad)
  Solid = true
  Symmetric = false
FEATURE [Sketcher::SketchObject] Sketch020
  FullyConstrained = true
  sketch-geometry (7):
    g0: LineSegment StartX=0 StartY=0 StartZ=0 EndX=0 EndY=6 EndZ=0
    g1: Circle CenterX=0 CenterY=0 CenterZ=0 NormalX=0 NormalY=0 NormalZ=1 AngleXU=0 Radius=1
    g2: Circle CenterX=8 CenterY=6 CenterZ=0 NormalX=0 NormalY=0 NormalZ=1 AngleXU=0 Radius=1
    g3: BSplineCurve PolesCount=3 KnotsCount=2 Degree=2 IsPeriodic=0
    g4: GeomPoint X=0 Y=0 Z=0
    g5: GeomPoint X=8 Y=6 Z=0
    g6: LineSegment StartX=0 StartY=6 StartZ=0 EndX=8 EndY=6 EndZ=0
  constraints (14):
    c: Coincident(g0,g-1)
    c: Distance(g0) = 6
    c: Vertical(g0)
    c: Coincident(g3,g0)
    c: Weight(g1) = 1
    c: Equal(g1,g2)
    c: InternalAlignment(g1,g3)
    c: InternalAlignment(g2,g3)
    c: InternalAlignment(g4,g3)
    c: InternalAlignment(g5,g3)
    c: Block(g3)
    c: Coincident(g6,g0)
    c: Coincident(g6,g3)
    c: Horizontal(g6)
FEATURE [Part::Extrusion] Extrude014  label="caseScrewPillarBracket002"
  Base = -> Sketch020
  Dir = (0,0,1)
  DirMode = 2
  FaceMakerClass = Part::FaceMakerBullseye
  LengthFwd = 2.4
  LengthRev = 0
  Placement = pos=(13.7,29,13.26) rot=(0,-1,0;1.5708rad)
  Solid = true
  Symmetric = false
FEATURE [Sketcher::SketchObject] Sketch021
  FullyConstrained = true
  sketch-geometry (7):
    g0: LineSegment StartX=0 StartY=0 StartZ=0 EndX=0 EndY=6 EndZ=0
    g1: Circle CenterX=0 CenterY=0 CenterZ=0 NormalX=0 NormalY=0 NormalZ=1 AngleXU=0 Radius=1
    g2: Circle CenterX=8 CenterY=6 CenterZ=0 NormalX=0 NormalY=0 NormalZ=1 AngleXU=0 Radius=1
    g3: BSplineCurve PolesCount=3 KnotsCount=2 Degree=2 IsPeriodic=0
    g4: GeomPoint X=0 Y=0 Z=0
    g5: GeomPoint X=8 Y=6 Z=0
    g6: LineSegment StartX=0 StartY=6 StartZ=0 EndX=8 EndY=6 EndZ=0
  constraints (14):
    c: Coincident(g0,g-1)
    c: Distance(g0) = 6
    c: Vertical(g0)
    c: Coincident(g3,g0)
    c: Weight(g1) = 1
    c: Equal(g1,g2)
    c: InternalAlignment(g1,g3)
    c: InternalAlignment(g2,g3)
    c: InternalAlignment(g4,g3)
    c: InternalAlignment(g5,g3)
    c: Block(g3)
    c: Coincident(g6,g0)
    c: Coincident(g6,g3)
    c: Horizontal(g6)
FEATURE [Part::Extrusion] Extrude015  label="caseScrewPillarBracket003"
  Base = -> Sketch021
  Dir = (0,0,1)
  DirMode = 2
  FaceMakerClass = Part::FaceMakerBullseye
  LengthFwd = 2.4
  LengthRev = 0
  Placement = pos=(11.3,29,58.74) rot=(0,1,0;1.5708rad)
  Solid = true
  Symmetric = false
FEATURE [Sketcher::SketchObject] Sketch022
  FullyConstrained = true
  sketch-geometry (7):
    g0: LineSegment StartX=0 StartY=0 StartZ=0 EndX=0 EndY=6 EndZ=0
    g1: Circle CenterX=0 CenterY=0 CenterZ=0 NormalX=0 NormalY=0 NormalZ=1 AngleXU=0 Radius=1
    g2: Circle CenterX=8 CenterY=6 CenterZ=0 NormalX=0 NormalY=0 NormalZ=1 AngleXU=0 Radius=1
    g3: BSplineCurve PolesCount=3 KnotsCount=2 Degree=2 IsPeriodic=0
    g4: GeomPoint X=0 Y=0 Z=0
    g5: GeomPoint X=8 Y=6 Z=0
    g6: LineSegment StartX=0 StartY=6 StartZ=0 EndX=8 EndY=6 EndZ=0
  constraints (14):
    c: Coincident(g0,g-1)
    c: Distance(g0) = 6
    c: Vertical(g0)
    c: Coincident(g3,g0)
    c: Weight(g1) = 1
    c: Equal(g1,g2)
    c: InternalAlignment(g1,g3)
    c: InternalAlignment(g2,g3)
    c: InternalAlignment(g4,g3)
    c: InternalAlignment(g5,g3)
    c: Block(g3)
    c: Coincident(g6,g0)
    c: Coincident(g6,g3)
    c: Horizontal(g6)
FEATURE [Part::Extrusion] Extrude016  label="caseScrewPillarBracket004"
  Base = -> Sketch022
  Dir = (0,0,1)
  DirMode = 2
  FaceMakerClass = Part::FaceMakerBullseye
  LengthFwd = 2.4
  LengthRev = 0
  Placement = pos=(88.3,29,65.23) rot=(0,1,0;1.5708rad)
  Solid = true
  Symmetric = false
FEATURE [Sketcher::SketchObject] Sketch023
  FullyConstrained = true
  sketch-geometry (7):
    g0: LineSegment StartX=0 StartY=0 StartZ=0 EndX=0 EndY=6 EndZ=0
    g1: Circle CenterX=0 CenterY=0 CenterZ=0 NormalX=0 NormalY=0 NormalZ=1 AngleXU=0 Radius=1
    g2: Circle CenterX=8 CenterY=6 CenterZ=0 NormalX=0 NormalY=0 NormalZ=1 AngleXU=0 Radius=1
    g3: BSplineCurve PolesCount=3 KnotsCount=2 Degree=2 IsPeriodic=0
    g4: GeomPoint X=0 Y=0 Z=0
    g5: GeomPoint X=8 Y=6 Z=0
    g6: LineSegment StartX=0 StartY=6 StartZ=0 EndX=8 EndY=6 EndZ=0
  constraints (14):
    c: Coincident(g0,g-1)
    c: Distance(g0) = 6
    c: Vertical(g0)
    c: Coincident(g3,g0)
    c: Weight(g1) = 1
    c: Equal(g1,g2)
    c: InternalAlignment(g1,g3)
    c: InternalAlignment(g2,g3)
    c: InternalAlignment(g4,g3)
    c: InternalAlignment(g5,g3)
    c: Block(g3)
    c: Coincident(g6,g0)
    c: Coincident(g6,g3)
    c: Horizontal(g6)
FEATURE [Part::Extrusion] Extrude017  label="caseScrewPillarBracket005"
  Base = -> Sketch023
  Dir = (0,0,1)
  DirMode = 2
  FaceMakerClass = Part::FaceMakerBullseye
  LengthFwd = 2.4
  LengthRev = 0
  Placement = pos=(90.7,29,6.77) rot=(0,-1,0;1.5708rad)
  Solid = true
  Symmetric = false
FEATURE [Sketcher::SketchObject] Sketch024
  FullyConstrained = true
  sketch-geometry (7):
    g0: LineSegment StartX=0 StartY=0 StartZ=0 EndX=0 EndY=6 EndZ=0
    g1: Circle CenterX=0 CenterY=0 CenterZ=0 NormalX=0 NormalY=0 NormalZ=1 AngleXU=0 Radius=1
    g2: Circle CenterX=8 CenterY=6 CenterZ=0 NormalX=0 NormalY=0 NormalZ=1 AngleXU=0 Radius=1
    g3: BSplineCurve PolesCount=3 KnotsCount=2 Degree=2 IsPeriodic=0
    g4: GeomPoint X=0 Y=0 Z=0
    g5: GeomPoint X=8 Y=6 Z=0
    g6: LineSegment StartX=0 StartY=6 StartZ=0 EndX=8 EndY=6 EndZ=0
  constraints (14):
    c: Coincident(g0,g-1)
    c: Distance(g0) = 6
    c: Vertical(g0)
    c: Coincident(g3,g0)
    c: Weight(g1) = 1
    c: Equal(g1,g2)
    c: InternalAlignment(g1,g3)
    c: InternalAlignment(g2,g3)
    c: InternalAlignment(g4,g3)
    c: InternalAlignment(g5,g3)
    c: Block(g3)
    c: Coincident(g6,g0)
    c: Coincident(g6,g3)
    c: Horizontal(g6)
FEATURE [Part::Extrusion] Extrude018  label="caseScrewPillarBracket006"
  Base = -> Sketch024
  Dir = (0,0,1)
  DirMode = 2
  FaceMakerClass = Part::FaceMakerBullseye
  LengthFwd = 2.4
  LengthRev = 0
  Placement = pos=(103.7,29,6.77) rot=(0,-1,0;1.5708rad)
  Solid = true
  Symmetric = false
FEATURE [Sketcher::SketchObject] Sketch025
  FullyConstrained = true
  sketch-geometry (7):
    g0: LineSegment StartX=0 StartY=0 StartZ=0 EndX=0 EndY=6 EndZ=0
    g1: Circle CenterX=0 CenterY=0 CenterZ=0 NormalX=0 NormalY=0 NormalZ=1 AngleXU=0 Radius=1
    g2: Circle CenterX=8 CenterY=6 CenterZ=0 NormalX=0 NormalY=0 NormalZ=1 AngleXU=0 Radius=1
    g3: BSplineCurve PolesCount=3 KnotsCount=2 Degree=2 IsPeriodic=0
    g4: GeomPoint X=0 Y=0 Z=0
    g5: GeomPoint X=8 Y=6 Z=0
    g6: LineSegment StartX=0 StartY=6 StartZ=0 EndX=8 EndY=6 EndZ=0
  constraints (14):
    c: Coincident(g0,g-1)
    c: Distance(g0) = 6
    c: Vertical(g0)
    c: Coincident(g3,g0)
    c: Weight(g1) = 1
    c: Equal(g1,g2)
    c: InternalAlignment(g1,g3)
    c: InternalAlignment(g2,g3)
    c: InternalAlignment(g4,g3)
    c: InternalAlignment(g5,g3)
    c: Block(g3)
    c: Coincident(g6,g0)
    c: Coincident(g6,g3)
    c: Horizontal(g6)
FEATURE [Part::Extrusion] Extrude019  label="caseScrewPillarBracket007"
  Base = -> Sketch025
  Dir = (0,0,1)
  DirMode = 2
  FaceMakerClass = Part::FaceMakerBullseye
  LengthFwd = 2.4
  LengthRev = 0
  Placement = pos=(101.3,29,65.23) rot=(0,1,0;1.5708rad)
  Solid = true
  Symmetric = false
FEATURE [Part::Box] Box011  label="frontCaseScrewPillarBracket"
  AttacherType = Attacher::AttachEngine3D
  Height = 2.4
  Length = 16
  Placement = pos=(87,28,2.3) rot=(0,0,1;0rad)
  Width = 7
FEATURE [Part::Box] Box012  label="frontCaseScrewPillarBracket001"
  AttacherType = Attacher::AttachEngine3D
  Height = 2.4
  Length = 16
  Placement = pos=(87,28,67.3) rot=(0,0,1;0rad)
  Width = 7
FEATURE [Sketcher::SketchObject] Sketch026
  FullyConstrained = true
  sketch-geometry (17):
    g0: Circle CenterX=-3.5 CenterY=23.5 CenterZ=0 NormalX=0 NormalY=0 NormalZ=1 AngleXU=0 Radius=1
    g1: Circle CenterX=-1 CenterY=15.25 CenterZ=0 NormalX=0 NormalY=0 NormalZ=1 AngleXU=0 Radius=1
    g2: Circle CenterX=-3.5 CenterY=7 CenterZ=0 NormalX=0 NormalY=0 NormalZ=1 AngleXU=0 Radius=1
    g3: BSplineCurve PolesCount=3 KnotsCount=2 Degree=2 IsPeriodic=0
    g4: GeomPoint X=-3.5 Y=23.5 Z=0
    g5: GeomPoint X=-3.5 Y=7 Z=0
    g6: Circle CenterX=-4.8 CenterY=30.5 CenterZ=0 NormalX=0 NormalY=0 NormalZ=1 AngleXU=0 Radius=1
    g7: Circle CenterX=-3.5 CenterY=30.5 CenterZ=0 NormalX=0 NormalY=0 NormalZ=1 AngleXU=0 Radius=1
    g8: Circle CenterX=-3.5 CenterY=29.2 CenterZ=0 NormalX=0 NormalY=0 NormalZ=1 AngleXU=0 Radius=1
    g9: BSplineCurve PolesCount=3 KnotsCount=2 Degree=2 IsPeriodic=0
    g10: GeomPoint X=-4.8 Y=30.5 Z=0
    g11: GeomPoint X=-3.5 Y=29.2 Z=0
    g12: LineSegment StartX=-3.5 StartY=29.2 StartZ=0 EndX=-3.5 EndY=23.5 EndZ=0
    g13: LineSegment StartX=-4.8 StartY=30.5 StartZ=0 EndX=0 EndY=30.5 EndZ=0
    g14: LineSegment StartX=-3.5 StartY=5 StartZ=0 EndX=-3.5 EndY=7 EndZ=0
    g15: LineSegment StartX=0 StartY=5 StartZ=0 EndX=0 EndY=30.5 EndZ=0
    g16: LineSegment StartX=-3.5 StartY=5 StartZ=0 EndX=0 EndY=5 EndZ=0
  constraints (33):
    c: Weight(g0) = 1
    c: Equal(g0,g1)
    c: Equal(g0,g2)
    c: InternalAlignment(g0,g3)
    c: InternalAlignment(g1,g3)
    c: InternalAlignment(g2,g3)
    c: InternalAlignment(g4,g3)
    c: InternalAlignment(g5,g3)
    c: Block(g3)
    c: Weight(g6) = 1
    c: Equal(g6,g7)
    c: Equal(g6,g8)
    c: InternalAlignment(g6,g9)
    c: InternalAlignment(g7,g9)
    c: InternalAlignment(g8,g9)
    c: InternalAlignment(g10,g9)
    c: InternalAlignment(g11,g9)
    c: Block(g9)
    c: Coincident(g12,g9)
    c: Coincident(g12,g3)
    c: Vertical(g12)
    c: Coincident(g13,g9)
    c: Horizontal(g13)
    c: Distance(g13) = 4.8
    c: Coincident(g14,g3)
    c: Vertical(g14)
    c: Coincident(g15,g13)
    c: Vertical(g15)
    c: Tangent(g15,g1)
    c: Distance(g14) = 2
    c: Coincident(g16,g14)
    c: Horizontal(g16)
    c: Coincident(g15,g16)
FEATURE [Part::Feature] Face050
  shape: bbox 4.8 x 25.5 x 2e-07 mm, 1 faces, 0 solids (baked)
FEATURE [Part::Revolution] Revolve054  label="moreFrontCaseScrewPost001"
  Angle = 360
  Axis = (0,1,0)
  Base = (0,0,0)
  FaceMakerClass = Part::FaceMakerBullseye
  Placement = pos=(102.5,4.5,3.5) rot=(0,0,1;0rad)
  Solid = false
  Source = -> Face050
  Symmetric = false
FEATURE [Part::Feature] Face051
  shape: bbox 4.8 x 25.5 x 2e-07 mm, 1 faces, 0 solids (baked)
FEATURE [Part::Revolution] Revolve055  label="moreFrontCaseScrewPost002"
  Angle = 360
  Axis = (0,1,0)
  Base = (0,0,0)
  FaceMakerClass = Part::FaceMakerBullseye
  Placement = pos=(102.5,4.5,68.5) rot=(0,0,1;0rad)
  Solid = false
  Source = -> Face051
  Symmetric = false
FEATURE [Sketcher::SketchObject] Sketch027
  FullyConstrained = true
  sketch-geometry (10):
    g0: LineSegment StartX=-1.6 StartY=4.7 StartZ=0 EndX=-1.6 EndY=1.7 EndZ=0
    g1: LineSegment StartX=-3.5 StartY=4.7 StartZ=0 EndX=-1.6 EndY=4.7 EndZ=0
    g2: LineSegment StartX=-1.6 StartY=1.7 StartZ=0 EndX=-1.6 EndY=1.5 EndZ=0
    g3: LineSegment StartX=-1.6 StartY=1.5 StartZ=0 EndX=-5.2 EndY=1.5 EndZ=0
    g4: Circle CenterX=-3.5 CenterY=4.7 CenterZ=0 NormalX=0 NormalY=0 NormalZ=1 AngleXU=0 Radius=1
    g5: Circle CenterX=-3.59627 CenterY=2.99743 CenterZ=0 NormalX=0 NormalY=0 NormalZ=1 AngleXU=0 Radius=1
    g6: Circle CenterX=-5.2 CenterY=1.5 CenterZ=0 NormalX=0 NormalY=0 NormalZ=1 AngleXU=0 Radius=1
    g7: BSplineCurve PolesCount=3 KnotsCount=2 Degree=2 IsPeriodic=0
    g8: GeomPoint X=-3.5 Y=4.7 Z=0
    g9: GeomPoint X=-5.2 Y=1.5 Z=0
  constraints (23):
    c: Vertical(g0)
    c: Distance(g0) = 3
    c: Coincident(g1,g0)
    c: Horizontal(g1)
    c: Block(g0)
    c: Block(g1)
    c: Coincident(g2,g0)
    c: Vertical(g2)
    c: Distance(g2) = 0.2
    c: Coincident(g3,g2)
    c: Horizontal(g3)
    c: Block(g3)
    c: Coincident(g7,g1)
    c: Weight(g4) = 1
    c: Equal(g4,g5)
    c: Equal(g4,g6)
    c: Coincident(g7,g3)
    c: InternalAlignment(g4,g7)
    c: InternalAlignment(g5,g7)
    c: InternalAlignment(g6,g7)
    c: InternalAlignment(g8,g7)
    c: InternalAlignment(g9,g7)
    c: Block(g7)
FEATURE [Sketcher::SketchObject] Sketch028
  FullyConstrained = true
  sketch-geometry (18):
    g0: LineSegment StartX=0 StartY=3e-16 StartZ=0 EndX=0 EndY=1.7 EndZ=0
    g1: LineSegment StartX=-3.5 StartY=0 StartZ=0 EndX=-3.5 EndY=0.9 EndZ=0
    g2: Circle CenterX=-2.7 CenterY=1.7 CenterZ=0 NormalX=0 NormalY=0 NormalZ=1 AngleXU=0 Radius=1
    g3: Circle CenterX=-3.5 CenterY=1.7 CenterZ=0 NormalX=0 NormalY=0 NormalZ=1 AngleXU=0 Radius=1
    g4: Circle CenterX=-3.5 CenterY=0.9 CenterZ=0 NormalX=0 NormalY=0 NormalZ=1 AngleXU=0 Radius=1
    g5: BSplineCurve PolesCount=3 KnotsCount=2 Degree=2 IsPeriodic=0
    g6: GeomPoint X=-2.7 Y=1.7 Z=0
    g7: GeomPoint X=-3.5 Y=0.9 Z=0
    g8: LineSegment StartX=-3.5 StartY=0 StartZ=0 EndX=-3.5 EndY=-7 EndZ=0
    g9: LineSegment StartX=0 StartY=3e-16 StartZ=0 EndX=0 EndY=-7 EndZ=0
    g10: LineSegment StartX=-3.5 StartY=-7 StartZ=0 EndX=0 EndY=-7 EndZ=0
    g11: LineSegment StartX=-2.7 StartY=1.7 StartZ=0 EndX=-1.6 EndY=1.7 EndZ=0
    g12: LineSegment StartX=0 StartY=1.7 StartZ=0 EndX=0 EndY=4.5 EndZ=0
    g13: LineSegment StartX=0 StartY=4.5 StartZ=0 EndX=0 EndY=10.8 EndZ=0
    g14: LineSegment StartX=0 StartY=10.8 StartZ=0 EndX=-2 EndY=10.8 EndZ=0
    g15: LineSegment StartX=-1.6 StartY=4.7 StartZ=0 EndX=-1.6 EndY=1.7 EndZ=0
    g16: LineSegment StartX=-1.6 StartY=4.7 StartZ=0 EndX=-2 EndY=4.7 EndZ=0
    g17: LineSegment StartX=-2 StartY=4.7 StartZ=0 EndX=-2 EndY=10.8 EndZ=0
  constraints (44):
    c: Vertical(g0)
    c: Vertical(g1)
    c: Distance(g1) = 0.9
    c: Block(g0)
    c: Distance(g0) = 1.7
    c: Weight(g2) = 1
    c: Equal(g2,g3)
    c: Equal(g2,g4)
    c: Coincident(g5,g1)
    c: InternalAlignment(g2,g5)
    c: InternalAlignment(g3,g5)
    c: InternalAlignment(g4,g5)
    c: InternalAlignment(g6,g5)
    c: InternalAlignment(g7,g5)
    c: Block(g5)
    c: Coincident(g8,g1)
    c: Vertical(g8)
    c: Distance(g8) = 7
    c: Vertical(g9)
    c: Equal(g8,g9) = 7
    c: Coincident(g9,g0)
    c: Coincident(g10,g8)
    c: Coincident(g10,g9)
    c: Horizontal(g10)
    c: Coincident(g11,g5)
    c: Horizontal(g11)
    c: Coincident(g12,g0)
    c: Vertical(g12)
    c: Distance(g12) = 2.8
    c: Coincident(g13,g12)
    c: Vertical(g13)
    c: Distance(g13) = 6.3
    c: Coincident(g14,g13)
    c: Horizontal(g14)
    c: Distance(g14) = 2
    c: Vertical(g15)
    c: Distance(g15) = 3
    c: Block(g11)
    c: Coincident(g15,g11)
    c: Coincident(g16,g15)
    c: Horizontal(g16)
    c: Coincident(g17,g16)
    c: Coincident(g17,g14)
    c: Vertical(g17)
FEATURE [Part::Revolution] Revolve040  label="backCaseScrewRetainer001"
  Angle = 360
  Axis = (0,1,0)
  Base = (0,0,0)
  FaceMakerClass = Part::FaceMakerBullseye
  Placement = pos=(12.5,3,10) rot=(0,0,1;0rad)
  Solid = false
  Source = -> Face036
  Symmetric = false
FEATURE [Part::Feature] Face055
  shape: bbox 3.5 x 30.2 x 2e-07 mm, 1 faces, 0 solids (baked)
FEATURE [Part::Revolution] Revolve059  label="backCaseScrewPost"
  Angle = 360
  Axis = (0,1,0)
  Base = (0,0,0)
  FaceMakerClass = Part::FaceMakerBullseye
  Placement = pos=(12.5,4.5,10) rot=(0,0,1;0rad)
  Solid = false
  Source = -> Face055
  Symmetric = false
FEATURE [Part::Feature] Face056
  shape: bbox 3.5 x 30.2 x 2e-07 mm, 1 faces, 0 solids (baked)
FEATURE [Part::Revolution] Revolve060  label="backCaseScrewPost001"
  Angle = 360
  Axis = (0,1,0)
  Base = (0,0,0)
  FaceMakerClass = Part::FaceMakerBullseye
  Placement = pos=(12.5,4.5,62) rot=(0,0,1;0rad)
  Solid = false
  Source = -> Face056
  Symmetric = false
FEATURE [Part::Feature] Face057
  shape: bbox 3.5 x 17.8 x 2e-07 mm, 1 faces, 0 solids (baked)
FEATURE [Part::Revolution] Revolve061  label="removeToCreateScrewAndThreadedInsertHole"
  Angle = 360
  Axis = (0,1,0)
  Base = (0,0,0)
  FaceMakerClass = Part::FaceMakerBullseye
  Placement = pos=(12.5,0,10) rot=(0,0,1;0rad)
  Solid = false
  Source = -> Face057
  Symmetric = false
FEATURE [Part::Feature] Face058
  shape: bbox 3.5 x 17.8 x 2e-07 mm, 1 faces, 0 solids (baked)
FEATURE [Part::Revolution] Revolve062  label="removeToCreateScrewAndThreadedInsertHole001"
  Angle = 360
  Axis = (0,1,0)
  Base = (0,0,0)
  FaceMakerClass = Part::FaceMakerBullseye
  Placement = pos=(12.5,0,62) rot=(0,0,1;0rad)
  Solid = false
  Source = -> Face058
  Symmetric = false
FEATURE [Part::Feature] Face059
  shape: bbox 3.5 x 17.8 x 2e-07 mm, 1 faces, 0 solids (baked)
FEATURE [Part::Revolution] Revolve063  label="removeToCreateScrewAndThreadedInsertHole002"
  Angle = 360
  Axis = (0,1,0)
  Base = (0,0,0)
  FaceMakerClass = Part::FaceMakerBullseye
  Placement = pos=(89.5,0,68.5) rot=(0,0,1;0rad)
  Solid = false
  Source = -> Face059
  Symmetric = false
FEATURE [Part::Feature] Face060
  shape: bbox 3.5 x 17.8 x 2e-07 mm, 1 faces, 0 solids (baked)
FEATURE [Part::Revolution] Revolve064  label="removeToCreateScrewAndThreadedInsertHole003"
  Angle = 360
  Axis = (0,1,0)
  Base = (0,0,0)
  FaceMakerClass = Part::FaceMakerBullseye
  Placement = pos=(89.5,0,3.5) rot=(0,0,1;0rad)
  Solid = false
  Source = -> Face060
  Symmetric = false
FEATURE [Part::Feature] Face061
  shape: bbox 3.5 x 17.8 x 2e-07 mm, 1 faces, 0 solids (baked)
FEATURE [Part::Revolution] Revolve065  label="removeToCreateScrewAndThreadedInsertHole004"
  Angle = 360
  Axis = (0,1,0)
  Base = (0,0,0)
  FaceMakerClass = Part::FaceMakerBullseye
  Placement = pos=(102.5,4.7,3.5) rot=(0,0,1;0rad)
  Solid = false
  Source = -> Face061
  Symmetric = false
FEATURE [Part::Feature] Face062
  shape: bbox 3.5 x 17.8 x 2e-07 mm, 1 faces, 0 solids (baked)
FEATURE [Part::Revolution] Revolve066  label="removeToCreateScrewAndThreadedInsertHole005"
  Angle = 360
  Axis = (0,1,0)
  Base = (0,0,0)
  FaceMakerClass = Part::FaceMakerBullseye
  Placement = pos=(102.5,4.7,68.5) rot=(0,0,1;0rad)
  Solid = false
  Source = -> Face062
  Symmetric = false
FEATURE [Part::MultiFuse] Fusion047  label="makeHoles"
  Shapes = -> [Revolve066,Revolve065,Revolve064,Revolve063,Revolve062,Revolve061]
FEATURE [Part::Feature] Face063
  shape: bbox 3.6 x 3.2 x 2e-07 mm, 1 faces, 0 solids (baked)
FEATURE [Part::Revolution] Revolve067  label="moreFrontCaseScrewRetainer002"
  Angle = 360
  Axis = (0,1,0)
  Base = (0,0,0)
  FaceMakerClass = Part::FaceMakerBullseye
  Placement = pos=(102.5,4.5,68.5) rot=(0,0,1;0rad)
  Solid = false
  Source = -> Face063
  Symmetric = false
FEATURE [Part::Feature] Face064
  shape: bbox 3.6 x 3.2 x 2e-07 mm, 1 faces, 0 solids (baked)
FEATURE [Part::Revolution] Revolve068  label="moreFrontCaseScrewRetainer003"
  Angle = 360
  Axis = (0,1,0)
  Base = (0,0,0)
  FaceMakerClass = Part::FaceMakerBullseye
  Placement = pos=(102.5,4.5,3.5) rot=(0,0,1;0rad)
  Solid = false
  Source = -> Face064
  Symmetric = false
FEATURE [Part::Feature] Face065
  shape: bbox 3.5 x 17.8 x 2e-07 mm, 1 faces, 0 solids (baked)
FEATURE [Part::Revolution] Revolve069  label="removeToCreateScrewAndThreadedInsertHole006"
  Angle = 360
  Axis = (0,1,0)
  Base = (0,0,0)
  FaceMakerClass = Part::FaceMakerBullseye
  Placement = pos=(12.5,0,10) rot=(0,0,1;0rad)
  Solid = false
  Source = -> Face065
  Symmetric = false
FEATURE [Part::Feature] Face066
  shape: bbox 3.5 x 17.8 x 2e-07 mm, 1 faces, 0 solids (baked)
FEATURE [Part::Revolution] Revolve070  label="removeToCreateScrewAndThreadedInsertHole007"
  Angle = 360
  Axis = (0,1,0)
  Base = (0,0,0)
  FaceMakerClass = Part::FaceMakerBullseye
  Placement = pos=(12.5,0,62) rot=(0,0,1;0rad)
  Solid = false
  Source = -> Face066
  Symmetric = false
FEATURE [Part::Feature] Face067
  shape: bbox 3.5 x 17.8 x 2e-07 mm, 1 faces, 0 solids (baked)
FEATURE [Part::Revolution] Revolve071  label="removeToCreateScrewAndThreadedInsertHole008"
  Angle = 360
  Axis = (0,1,0)
  Base = (0,0,0)
  FaceMakerClass = Part::FaceMakerBullseye
  Placement = pos=(89.5,0,68.5) rot=(0,0,1;0rad)
  Solid = false
  Source = -> Face067
  Symmetric = false
FEATURE [Part::Feature] Face068
  shape: bbox 3.5 x 17.8 x 2e-07 mm, 1 faces, 0 solids (baked)
FEATURE [Part::Revolution] Revolve072  label="removeToCreateScrewAndThreadedInsertHole009"
  Angle = 360
  Axis = (0,1,0)
  Base = (0,0,0)
  FaceMakerClass = Part::FaceMakerBullseye
  Placement = pos=(89.5,0,3.5) rot=(0,0,1;0rad)
  Solid = false
  Source = -> Face068
  Symmetric = false
FEATURE [Part::Feature] Face069
  shape: bbox 3.5 x 17.8 x 2e-07 mm, 1 faces, 0 solids (baked)
FEATURE [Part::Feature] Face070
  shape: bbox 3.5 x 17.8 x 2e-07 mm, 1 faces, 0 solids (baked)
FEATURE [Part::Revolution] Revolve073  label="removeToCreateScrewAndThreadedInsertHole010"
  Angle = 360
  Axis = (0,1,0)
  Base = (0,0,0)
  FaceMakerClass = Part::FaceMakerBullseye
  Placement = pos=(102.5,4.7,3.5) rot=(0,0,1;0rad)
  Solid = false
  Source = -> Face069
  Symmetric = false
FEATURE [Part::Revolution] Revolve074  label="removeToCreateScrewAndThreadedInsertHole011"
  Angle = 360
  Axis = (0,1,0)
  Base = (0,0,0)
  FaceMakerClass = Part::FaceMakerBullseye
  Placement = pos=(102.5,4.7,68.5) rot=(0,0,1;0rad)
  Solid = false
  Source = -> Face070
  Symmetric = false
FEATURE [Part::MultiFuse] Fusion048  label="makeHoles001"
  Shapes = -> [Revolve074,Revolve073,Revolve072,Revolve071,Revolve070,Revolve069]
FEATURE [Part::MultiFuse] Fusion049  label="caseScrewRetainers"
  Shapes = -> [Revolve067,Revolve068,Revolve048,Revolve047,Revolve039,Revolve040]
FEATURE [Part::Cut] Cut015  label="caseScrewRetainers001"
  Base = -> Fusion049
  Tool = -> Fusion048
FEATURE [Part::MultiFuse] Fusion050  label="casePillars"
  Shapes = -> [Revolve055,Revolve054,Revolve043,Revolve046,Revolve059,Revolve060]
FEATURE [Part::Feature] Face071 .. Face076  x6 (patterned run collapsed; names and placements below)
  shape: bbox 3.5 x 17.8 x 2e-07 mm, 1 faces, 0 solids (baked)
FEATURE [Part::Revolution] Revolve075  label="removeToCreateScrewAndThreadedInsertHole012"
  Angle = 360
  Axis = (0,1,0)
  Base = (0,0,0)
  FaceMakerClass = Part::FaceMakerBullseye
  Placement = pos=(12.5,0,10) rot=(0,0,1;0rad)
  Solid = false
  Source = -> Face071
  Symmetric = false
FEATURE [Part::Revolution] Revolve076  label="removeToCreateScrewAndThreadedInsertHole013"
  Angle = 360
  Axis = (0,1,0)
  Base = (0,0,0)
  FaceMakerClass = Part::FaceMakerBullseye
  Placement = pos=(12.5,0,62) rot=(0,0,1;0rad)
  Solid = false
  Source = -> Face072
  Symmetric = false
FEATURE [Part::Revolution] Revolve077  label="removeToCreateScrewAndThreadedInsertHole014"
  Angle = 360
  Axis = (0,1,0)
  Base = (0,0,0)
  FaceMakerClass = Part::FaceMakerBullseye
  Placement = pos=(89.5,0,68.5) rot=(0,0,1;0rad)
  Solid = false
  Source = -> Face073
  Symmetric = false
FEATURE [Part::Revolution] Revolve078  label="removeToCreateScrewAndThreadedInsertHole015"
  Angle = 360
  Axis = (0,1,0)
  Base = (0,0,0)
  FaceMakerClass = Part::FaceMakerBullseye
  Placement = pos=(89.5,0,3.5) rot=(0,0,1;0rad)
  Solid = false
  Source = -> Face074
  Symmetric = false
FEATURE [Part::Revolution] Revolve079  label="removeToCreateScrewAndThreadedInsertHole016"
  Angle = 360
  Axis = (0,1,0)
  Base = (0,0,0)
  FaceMakerClass = Part::FaceMakerBullseye
  Placement = pos=(102.5,4.7,3.5) rot=(0,0,1;0rad)
  Solid = false
  Source = -> Face075
  Symmetric = false
FEATURE [Part::Revolution] Revolve080  label="removeToCreateScrewAndThreadedInsertHole017"
  Angle = 360
  Axis = (0,1,0)
  Base = (0,0,0)
  FaceMakerClass = Part::FaceMakerBullseye
  Placement = pos=(102.5,4.7,68.5) rot=(0,0,1;0rad)
  Solid = false
  Source = -> Face076
  Symmetric = false
FEATURE [Part::MultiFuse] Fusion051  label="makeHoles002"
  Shapes = -> [Revolve080,Revolve079,Revolve078,Revolve077,Revolve076,Revolve075]
FEATURE [Part::Cut] Cut016  label="caesPillars"
  Base = -> Fusion050
  Tool = -> Fusion051
FEATURE [Part::Revolution] Revolve009  label="plugHousing016"
  Angle = 360
  Axis = (0,1,0)
  Base = (0,0,0)
  FaceMakerClass = Part::FaceMakerBullseye
  Placement = pos=(0,0,36.15) rot=(0,0,1;0rad)
  Solid = false
  Source = -> Face012
  Symmetric = false
FEATURE [Part::MultiFuse] Fusion014  label="plugHousing023"
  Placement = pos=(0,0,0) rot=(0,0,1;1.5708rad)
  Shapes = -> [Revolve011,Revolve009]
FEATURE [Part::Revolution] Revolve010  label="plugHousing017"
  Angle = 360
  Axis = (0,1,0)
  Base = (0,0,0)
  FaceMakerClass = Part::FaceMakerBullseye
  Placement = pos=(0,0,36.15) rot=(0,0,1;0rad)
  Solid = false
  Source = -> Face014
  Symmetric = false
FEATURE [Part::MultiFuse] Fusion015  label="plugHousing024"
  Placement = pos=(0,0,0) rot=(0,0,1;1.5708rad)
  Shapes = -> [Revolve010,Revolve015]
FEATURE [Part::Revolution] Revolve014  label="plugHousing026"
  Angle = 360
  Axis = (0,1,0)
  Base = (0,0,0)
  FaceMakerClass = Part::FaceMakerBullseye
  Placement = pos=(0,0,36.15) rot=(0,0,1;0rad)
  Solid = false
  Source = -> Face011
  Symmetric = false
FEATURE [Part::Revolution] Revolve013  label="plugHousing025"
  Angle = 360
  Axis = (0,1,0)
  Base = (0,0,0)
  FaceMakerClass = Part::FaceMakerBullseye
  Placement = pos=(0,0,36.15) rot=(0,0,1;0rad)
  Solid = false
  Source = -> Face015
  Symmetric = false
FEATURE [Part::MultiFuse] Fusion016  label="plugHousing028"
  Placement = pos=(0,19,0) rot=(0,0,1;3.14159rad)
  Shapes = -> [Fusion014,Fusion013]
FEATURE [Part::MultiFuse] Fusion011  label="plugHousing018"
  Placement = pos=(0,0,0) rot=(0,0,1;1.5708rad)
  Shapes = -> [Revolve014,Revolve013]
FEATURE [Part::MultiFuse] Fusion012  label="plugHousing019"
  Placement = pos=(0,19,0) rot=(0,0,1;3.14159rad)
  Shapes = -> [Fusion011,Fusion015]
FEATURE [Part::MultiFuse] Fusion017  label="plugHousing029"
  Placement = pos=(122.621,0,-0.15) rot=(0,0,1;0rad)
  Shapes = -> [Fusion016,Fusion012]
FEATURE [Part::MultiFuse] Fusion052  label="casePillarRetainers"
  Shapes = -> [Extrude012,Extrude013,Extrude014,Extrude015,Extrude016,Extrude017,Extrude018,Extrude019,Box011,Box012]
FEATURE [Part::Feature] Face077
  shape: bbox 3.5 x 17.8 x 2e-07 mm, 1 faces, 0 solids (baked)
FEATURE [Part::Revolution] Revolve081  label="removeToCreateScrewAndThreadedInsertHole018"
  Angle = 360
  Axis = (0,1,0)
  Base = (0,0,0)
  FaceMakerClass = Part::FaceMakerBullseye
  Placement = pos=(62.3,30.3,19.7) rot=(0,0,1;0rad)
  Solid = false
  Source = -> Face077
  Symmetric = false
FEATURE [Part::Feature] Face078
  shape: bbox 3.5 x 17.8 x 2e-07 mm, 1 faces, 0 solids (baked)
FEATURE [Part::Revolution] Revolve082  label="removeToCreateScrewAndThreadedInsertHole019"
  Angle = 360
  Axis = (0,1,0)
  Base = (0,0,0)
  FaceMakerClass = Part::FaceMakerBullseye
  Placement = pos=(62.3,30.3,51.7) rot=(0,0,1;0rad)
  Solid = false
  Source = -> Face078
  Symmetric = false
FEATURE [Part::Feature] Face079
  shape: bbox 3.5 x 17.8 x 2e-07 mm, 1 faces, 0 solids (baked)
FEATURE [Part::Revolution] Revolve083  label="removeToCreateScrewAndThreadedInsertHole020"
  Angle = 360
  Axis = (0,1,0)
  Base = (0,0,0)
  FaceMakerClass = Part::FaceMakerBullseye
  Placement = pos=(30.3,30.3,19.7) rot=(0,0,1;0rad)
  Solid = false
  Source = -> Face079
  Symmetric = false
FEATURE [Part::Feature] Face080
  shape: bbox 3.5 x 17.8 x 2e-07 mm, 1 faces, 0 solids (baked)
FEATURE [Part::Revolution] Revolve084  label="removeToCreateScrewAndThreadedInsertHole021"
  Angle = 360
  Axis = (0,1,0)
  Base = (0,0,0)
  FaceMakerClass = Part::FaceMakerBullseye
  Placement = pos=(30.3,30.3,51.7) rot=(0,0,1;0rad)
  Solid = false
  Source = -> Face080
  Symmetric = false
FEATURE [Part::MultiFuse] Fusion053  label="createThreadedInsertHolesForFan"
  Shapes = -> [Revolve081,Revolve082,Revolve083,Revolve084]
FEATURE [Part::Cut] Cut017  label="fanScrewHousing001"
  Base = -> Fusion046
  Tool = -> Fusion053
FEATURE [Part::Feature] Face081
  shape: bbox 3.5 x 17.8 x 2e-07 mm, 1 faces, 0 solids (baked)
FEATURE [Part::Revolution] Revolve085  label="removeToCreateScrewAndThreadedInsertHole022"
  Angle = 360
  Axis = (0,1,0)
  Base = (0,0,0)
  FaceMakerClass = Part::FaceMakerBullseye
  Placement = pos=(62.3,30.3,19.7) rot=(0,0,1;0rad)
  Solid = false
  Source = -> Face081
  Symmetric = false
FEATURE [Part::Feature] Face082
  shape: bbox 3.5 x 17.8 x 2e-07 mm, 1 faces, 0 solids (baked)
FEATURE [Part::Revolution] Revolve086  label="removeToCreateScrewAndThreadedInsertHole023"
  Angle = 360
  Axis = (0,1,0)
  Base = (0,0,0)
  FaceMakerClass = Part::FaceMakerBullseye
  Placement = pos=(62.3,30.3,51.7) rot=(0,0,1;0rad)
  Solid = false
  Source = -> Face082
  Symmetric = false
FEATURE [Part::Feature] Face083
  shape: bbox 3.5 x 17.8 x 2e-07 mm, 1 faces, 0 solids (baked)
FEATURE [Part::Revolution] Revolve087  label="removeToCreateScrewAndThreadedInsertHole024"
  Angle = 360
  Axis = (0,1,0)
  Base = (0,0,0)
  FaceMakerClass = Part::FaceMakerBullseye
  Placement = pos=(30.3,30.3,19.7) rot=(0,0,1;0rad)
  Solid = false
  Source = -> Face083
  Symmetric = false
FEATURE [Part::Feature] Face084
  shape: bbox 3.5 x 17.8 x 2e-07 mm, 1 faces, 0 solids (baked)
FEATURE [Part::Revolution] Revolve088  label="removeToCreateScrewAndThreadedInsertHole025"
  Angle = 360
  Axis = (0,1,0)
  Base = (0,0,0)
  FaceMakerClass = Part::FaceMakerBullseye
  Placement = pos=(30.3,30.3,51.7) rot=(0,0,1;0rad)
  Solid = false
  Source = -> Face084
  Symmetric = false
FEATURE [Part::MultiFuse] Fusion054  label="createThreadedInsertHolesForFan001"
  Shapes = -> [Revolve085,Revolve086,Revolve087,Revolve088]
FEATURE [Part::Cut] Cut018  label="top007"
  Base = -> Fusion040
  Tool = -> Fusion054
FEATURE [Sketcher::SketchObject] Sketch029
  FullyConstrained = false
  Placement = pos=(0,0,0) rot=(1,0,0;1.5708rad)
  sketch-geometry (24):
    g0: ArcOfCircle CenterX=-4 CenterY=-10.5 CenterZ=0 NormalX=0 NormalY=0 NormalZ=1 AngleXU=0 Radius=1.5 StartAngle=6e-16 EndAngle=3.14159
    g1: ArcOfCircle CenterX=-34.2 CenterY=-10.5 CenterZ=0 NormalX=0 NormalY=0 NormalZ=1 AngleXU=0 Radius=1.5 StartAngle=0 EndAngle=3.14159
    g2: ArcOfCircle CenterX=-34.2 CenterY=-27.7 CenterZ=0 NormalX=0 NormalY=0 NormalZ=1 AngleXU=0 Radius=1.5 StartAngle=3.14159 EndAngle=6.28319
    g3: ArcOfCircle CenterX=-4 CenterY=-27.7 CenterZ=0 NormalX=0 NormalY=0 NormalZ=1 AngleXU=0 Radius=1.5 StartAngle=3.1416 EndAngle=6.28319
    g4: ArcOfCircle CenterX=-10 CenterY=-4.3 CenterZ=0 NormalX=0 NormalY=0 NormalZ=1 AngleXU=0 Radius=1.5 StartAngle=2e-16 EndAngle=3.14159
    g5: ArcOfCircle CenterX=-16.1 CenterY=-1.8 CenterZ=0 NormalX=0 NormalY=0 NormalZ=1 AngleXU=0 Radius=1.5 StartAngle=5e-16 EndAngle=3.14159
    g6: ArcOfCircle CenterX=-22.1 CenterY=-1.8 CenterZ=0 NormalX=0 NormalY=0 NormalZ=1 AngleXU=0 Radius=1.5 StartAngle=5e-16 EndAngle=3.14159
    g7: ArcOfCircle CenterX=-28.2 CenterY=-4.3 CenterZ=0 NormalX=0 NormalY=0 NormalZ=1 AngleXU=0 Radius=1.5 StartAngle=2e-16 EndAngle=3.14159
    g8: ArcOfCircle CenterX=-10 CenterY=-33.9 CenterZ=0 NormalX=0 NormalY=0 NormalZ=1 AngleXU=0 Radius=1.5 StartAngle=3.14159 EndAngle=6.28319
    g9: ArcOfCircle CenterX=-16.1 CenterY=-36.4 CenterZ=0 NormalX=0 NormalY=0 NormalZ=1 AngleXU=0 Radius=1.5 StartAngle=3.14159 EndAngle=6.28319
    g10: ArcOfCircle CenterX=-22.1 CenterY=-36.4 CenterZ=0 NormalX=0 NormalY=0 NormalZ=1 AngleXU=0 Radius=1.5 StartAngle=3.14159 EndAngle=6.28319
    g11: ArcOfCircle CenterX=-28.2 CenterY=-33.9 CenterZ=0 NormalX=0 NormalY=0 NormalZ=1 AngleXU=0 Radius=1.5 StartAngle=3.14159 EndAngle=6.28319
    g12: LineSegment StartX=-35.7 StartY=-10.5 StartZ=0 EndX=-35.7 EndY=-27.7 EndZ=0
    g13: LineSegment StartX=-32.7 StartY=-10.5 StartZ=0 EndX=-32.7 EndY=-27.7 EndZ=0
    g14: LineSegment StartX=-29.7 StartY=-33.9 StartZ=0 EndX=-29.7 EndY=-4.3 EndZ=0
    g15: LineSegment StartX=-26.7 StartY=-33.9 StartZ=0 EndX=-26.7 EndY=-4.3 EndZ=0
    g16: LineSegment StartX=-2.5 StartY=-10.5 StartZ=0 EndX=-2.5 EndY=-27.7 EndZ=0
    g17: LineSegment StartX=-8.5 StartY=-4.3 StartZ=0 EndX=-8.5 EndY=-33.9 EndZ=0
    g18: LineSegment StartX=-5.5 StartY=-10.5 StartZ=0 EndX=-5.5 EndY=-27.7 EndZ=0
    g19: LineSegment StartX=-11.5 StartY=-4.3 StartZ=0 EndX=-11.5 EndY=-33.9 EndZ=0
    g20: LineSegment StartX=-14.6 StartY=-1.8 StartZ=0 EndX=-14.6 EndY=-36.4 EndZ=0
    g21: LineSegment StartX=-17.6 StartY=-1.8 StartZ=0 EndX=-17.6 EndY=-36.4 EndZ=0
    g22: LineSegment StartX=-20.6 StartY=-36.4 StartZ=0 EndX=-20.6 EndY=-1.8 EndZ=0
    g23: LineSegment StartX=-23.6 StartY=-1.8 StartZ=0 EndX=-23.6 EndY=-36.4 EndZ=0
  constraints (48):
    c: Block(g0)
    c: Block(g1)
    c: Block(g2)
    c: Block(g3)
    c: Block(g4)
    c: Block(g5)
    c: Block(g6)
    c: Block(g7)
    c: Block(g8)
    c: Block(g9)
    c: Block(g10)
    c: Block(g11)
    c: Coincident(g12,g1)
    c: Coincident(g12,g2)
    c: Vertical(g12)
    c: Coincident(g13,g1)
    c: Coincident(g13,g2)
    c: Vertical(g13)
    c: Coincident(g14,g11)
    c: Coincident(g14,g7)
    c: Vertical(g14)
    c: Coincident(g15,g11)
    c: Coincident(g15,g7)
    c: Vertical(g15)
    c: Coincident(g16,g0)
    c: Coincident(g16,g3)
    c: Vertical(g16)
    c: Coincident(g17,g4)
    c: Coincident(g17,g8)
    c: Vertical(g17)
    c: Coincident(g18,g0)
    c: Coincident(g18,g3)
    c: Vertical(g18)
    c: Coincident(g19,g4)
    c: Coincident(g19,g8)
    c: Vertical(g19)
    c: Coincident(g20,g5)
    c: Coincident(g20,g9)
    c: Vertical(g20)
    c: Coincident(g21,g5)
    c: Coincident(g21,g9)
    c: Vertical(g21)
    c: Coincident(g22,g10)
    c: Coincident(g22,g6)
    c: Vertical(g22)
    c: Coincident(g23,g6)
    c: Coincident(g23,g10)
    c: Vertical(g23)
FEATURE [Part::Extrusion] Extrude020  label="removeToCreateFanGrillHoles"
  Base = -> Sketch029
  Dir = (0,-1,6e-16)
  DirMode = 2
  FaceMakerClass = Part::FaceMakerBullseye
  LengthFwd = 10
  LengthRev = 0
  Placement = pos=(65.4,44,54.82) rot=(0,0,1;0rad)
  Solid = true
  Symmetric = false
FEATURE [Part::MultiFuse] Fusion055  label="top008"
  Shapes = -> [Cut017,Cut018]
FEATURE [Part::Cut] Cut019  label="top009"
  Base = -> Fusion055
  Tool = -> Extrude020
FEATURE [App::MeasureDistance] Distance003  label="Distance: 71.95 mm"
  Distance = 71.9513
  P1 = (117,38,72)
  P2 = (117,38,0.0487319)
FEATURE [Sketcher::SketchObject] Sketch030
  FullyConstrained = true
  Placement = pos=(117,19,0) rot=(0.57735,0.57735,0.57735;2.0944rad)
  sketch-geometry (48):
    g0: LineSegment StartX=-49.19 StartY=69.25 StartZ=0 EndX=-49.19 EndY=66.25 EndZ=0
    g1: LineSegment StartX=-49.19 StartY=63.5 StartZ=0 EndX=-49.19 EndY=60.5 EndZ=0
    g2: LineSegment StartX=-49.19 StartY=57.75 StartZ=0 EndX=-49.19 EndY=54.75 EndZ=0
    g3: LineSegment StartX=-49.19 StartY=52 StartZ=0 EndX=-49.19 EndY=49 EndZ=0
    g4: LineSegment StartX=-49.19 StartY=46.25 StartZ=0 EndX=-49.19 EndY=43.25 EndZ=0
    g5: LineSegment StartX=-49.19 StartY=40.5 StartZ=0 EndX=-49.19 EndY=37.5 EndZ=0
    g6: LineSegment StartX=-49.19 StartY=34.5 StartZ=0 EndX=-49.19 EndY=31.5 EndZ=0
    g7: LineSegment StartX=-49.19 StartY=28.75 StartZ=0 EndX=-49.19 EndY=25.75 EndZ=0
    g8: LineSegment StartX=-49.19 StartY=23 StartZ=0 EndX=-49.19 EndY=20 EndZ=0
    g9: LineSegment StartX=-49.19 StartY=17.25 StartZ=0 EndX=-49.19 EndY=14.25 EndZ=0
    g10: LineSegment StartX=-49.19 StartY=11.5 StartZ=0 EndX=-49.19 EndY=8.5 EndZ=0
    g11: LineSegment StartX=-49.19 StartY=5.75 StartZ=0 EndX=-49.19 EndY=2.75 EndZ=0
    g12: ArcOfCircle CenterX=-1.5 CenterY=67.75 CenterZ=0 NormalX=0 NormalY=0 NormalZ=1 AngleXU=0 Radius=1.5 StartAngle=4.71239 EndAngle=7.85398
    g13: ArcOfCircle CenterX=-1.5 CenterY=62 CenterZ=0 NormalX=0 NormalY=0 NormalZ=1 AngleXU=0 Radius=1.5 StartAngle=4.71239 EndAngle=7.85398
    g14: ArcOfCircle CenterX=-1.5 CenterY=56.25 CenterZ=0 NormalX=0 NormalY=0 NormalZ=1 AngleXU=0 Radius=1.5 StartAngle=4.71239 EndAngle=7.85398
    g15: ArcOfCircle CenterX=-11.49 CenterY=50.5 CenterZ=0 NormalX=0 NormalY=0 NormalZ=1 AngleXU=0 Radius=1.5 StartAngle=4.71239 EndAngle=7.85398
    g16: ArcOfCircle CenterX=-16.28 CenterY=44.75 CenterZ=0 NormalX=0 NormalY=0 NormalZ=1 AngleXU=0 Radius=1.5 StartAngle=4.71239 EndAngle=7.85398
    g17: ArcOfCircle CenterX=-18.2337 CenterY=39 CenterZ=0 NormalX=0 NormalY=0 NormalZ=1 AngleXU=0 Radius=1.5 StartAngle=4.71485 EndAngle=7.85398
    g18: ArcOfCircle CenterX=-16.2837 CenterY=27.25 CenterZ=0 NormalX=0 NormalY=0 NormalZ=1 AngleXU=0 Radius=1.5 StartAngle=4.71485 EndAngle=7.85398
    g19: ArcOfCircle CenterX=-18.2337 CenterY=33 CenterZ=0 NormalX=0 NormalY=0 NormalZ=1 AngleXU=0 Radius=1.5 StartAngle=4.71485 EndAngle=7.85398
    g20: ArcOfCircle CenterX=-11.49 CenterY=21.5 CenterZ=0 NormalX=0 NormalY=0 NormalZ=1 AngleXU=0 Radius=1.5 StartAngle=4.71239 EndAngle=7.85398
    g21: ArcOfCircle CenterX=-1.5 CenterY=4.25 CenterZ=0 NormalX=0 NormalY=0 NormalZ=1 AngleXU=0 Radius=1.5 StartAngle=4.71239 EndAngle=7.85398
    g22: ArcOfCircle CenterX=-1.5 CenterY=10 CenterZ=0 NormalX=0 NormalY=0 NormalZ=1 AngleXU=0 Radius=1.5 StartAngle=4.71239 EndAngle=7.85398
    g23: ArcOfCircle CenterX=-1.5 CenterY=15.75 CenterZ=0 NormalX=0 NormalY=0 NormalZ=1 AngleXU=0 Radius=1.5 StartAngle=4.71239 EndAngle=7.85398
    g24: LineSegment StartX=-49.19 StartY=69.25 StartZ=0 EndX=-1.5 EndY=69.25 EndZ=0
    g25: LineSegment StartX=-49.19 StartY=66.25 StartZ=0 EndX=-1.5 EndY=66.25 EndZ=0
    g26: LineSegment StartX=-49.19 StartY=63.5 StartZ=0 EndX=-1.5 EndY=63.5 EndZ=0
    g27: LineSegment StartX=-49.19 StartY=60.5 StartZ=0 EndX=-1.5 EndY=60.5 EndZ=0
    g28: LineSegment StartX=-49.19 StartY=57.75 StartZ=0 EndX=-1.5 EndY=57.75 EndZ=0
    g29: LineSegment StartX=-49.19 StartY=54.75 StartZ=0 EndX=-1.5 EndY=54.75 EndZ=0
    g30: LineSegment StartX=-49.19 StartY=52 StartZ=0 EndX=-11.49 EndY=52 EndZ=0
    g31: LineSegment StartX=-49.19 StartY=49 StartZ=0 EndX=-11.49 EndY=49 EndZ=0
    g32: LineSegment StartX=-49.19 StartY=46.25 StartZ=0 EndX=-16.28 EndY=46.25 EndZ=0
    g33: LineSegment StartX=-49.19 StartY=43.25 StartZ=0 EndX=-16.28 EndY=43.25 EndZ=0
    g34: LineSegment StartX=-49.19 StartY=40.5 StartZ=0 EndX=-18.2337 EndY=40.5 EndZ=0
    g35: LineSegment StartX=-49.19 StartY=37.5 StartZ=0 EndX=-18.23 EndY=37.5 EndZ=0
    g36: LineSegment StartX=-49.19 StartY=34.5 StartZ=0 EndX=-18.2337 EndY=34.5 EndZ=0
    g37: LineSegment StartX=-49.19 StartY=31.5 StartZ=0 EndX=-18.23 EndY=31.5 EndZ=0
    g38: LineSegment StartX=-49.19 StartY=28.75 StartZ=0 EndX=-16.2837 EndY=28.75 EndZ=0
    g39: LineSegment StartX=-49.19 StartY=25.75 StartZ=0 EndX=-16.28 EndY=25.75 EndZ=0
    g40: LineSegment StartX=-49.19 StartY=23 StartZ=0 EndX=-11.49 EndY=23 EndZ=0
    g41: LineSegment StartX=-49.19 StartY=20 StartZ=0 EndX=-11.49 EndY=20 EndZ=0
    g42: LineSegment StartX=-49.19 StartY=17.25 StartZ=0 EndX=-1.5 EndY=17.25 EndZ=0
    g43: LineSegment StartX=-49.19 StartY=14.25 StartZ=0 EndX=-1.5 EndY=14.25 EndZ=0
    g44: LineSegment StartX=-49.19 StartY=11.5 StartZ=0 EndX=-1.5 EndY=11.5 EndZ=0
    g45: LineSegment StartX=-49.19 StartY=8.5 StartZ=0 EndX=-1.5 EndY=8.5 EndZ=0
    g46: LineSegment StartX=-49.19 StartY=5.75 StartZ=0 EndX=-1.5 EndY=5.75 EndZ=0
    g47: LineSegment StartX=-49.19 StartY=2.75 StartZ=0 EndX=-1.5 EndY=2.75 EndZ=0
  constraints (120):
    c: Vertical(g0)
    c: Distance(g0) = 3
    c: Block(g0)
    c: Vertical(g1)
    c: Distance(g1) = 3
    c: Vertical(g2)
    c: Equal(g0,g2) = 3
    c: Block(g2)
    c: Vertical(g3)
    c: Equal(g1,g3) = 3
    c: Vertical(g4)
    c: Equal(g0,g4) = 3
    c: Block(g4)
    c: Vertical(g5)
    c: Equal(g1,g5) = 3
    c: Vertical(g6)
    c: Equal(g0,g6) = 3
    c: Block(g6)
    c: Vertical(g7)
    c: Equal(g1,g7) = 3
    c: Vertical(g8)
    c: Equal(g0,g8) = 3
    c: Block(g8)
    c: Vertical(g9)
    c: Equal(g1,g9) = 3
    c: Vertical(g10)
    c: Equal(g0,g10) = 3
    c: Block(g10)
    c: Vertical(g11)
    c: Equal(g1,g11) = 3
    c: Block(g12)
    c: Block(g13)
    c: Block(g14)
    c: Block(g15)
    c: Block(g16)
    c: Block(g17)
    c: Block(g18)
    c: Block(g19)
    c: Block(g20)
    c: Block(g21)
    c: Block(g22)
    c: Block(g23)
    c: Block(g11)
    c: Block(g9)
    c: Block(g7)
    c: Block(g5)
    c: Block(g3)
    c: Block(g1)
    c: Coincident(g24,g0)
    c: Coincident(g24,g12)
    c: Horizontal(g24)
    c: Coincident(g25,g0)
    c: Coincident(g25,g12)
    c: Horizontal(g25)
    c: Coincident(g26,g1)
    c: Coincident(g26,g13)
    c: Horizontal(g26)
    c: Coincident(g27,g1)
    c: Coincident(g27,g13)
    c: Horizontal(g27)
    c: Coincident(g28,g2)
    c: Coincident(g28,g14)
    c: Horizontal(g28)
    c: Coincident(g29,g2)
    c: Coincident(g29,g14)
    c: Horizontal(g29)
    c: Coincident(g30,g3)
    c: Coincident(g30,g15)
    c: Horizontal(g30)
    c: Coincident(g31,g3)
    c: Coincident(g31,g15)
    c: Horizontal(g31)
    c: Coincident(g32,g4)
    c: Coincident(g32,g16)
    c: Horizontal(g32)
    c: Coincident(g33,g4)
    c: Coincident(g33,g16)
    c: Horizontal(g33)
    c: Coincident(g34,g5)
    c: Coincident(g34,g17)
    c: Horizontal(g34)
    c: Coincident(g35,g5)
    c: Coincident(g35,g17)
    c: Horizontal(g35)
    c: Coincident(g36,g6)
    c: Coincident(g36,g19)
    c: Horizontal(g36)
    c: Coincident(g37,g6)
    c: Coincident(g37,g19)
    c: Horizontal(g37)
    c: Coincident(g38,g7)
    c: Coincident(g38,g18)
    c: Horizontal(g38)
    c: Coincident(g39,g7)
    c: Coincident(g39,g18)
    c: Horizontal(g39)
    c: Coincident(g40,g8)
    c: Coincident(g40,g20)
    c: Horizontal(g40)
    c: Coincident(g41,g8)
    c: Coincident(g41,g20)
    c: Horizontal(g41)
    c: Coincident(g42,g9)
    c: Coincident(g42,g23)
    c: Horizontal(g42)
    c: Coincident(g43,g9)
    c: Coincident(g43,g23)
    c: Horizontal(g43)
    c: Coincident(g44,g10)
    c: Coincident(g44,g22)
    c: Horizontal(g44)
    c: Coincident(g45,g10)
    c: Coincident(g45,g22)
    c: Horizontal(g45)
    c: Coincident(g46,g11)
    c: Coincident(g46,g21)
    c: Horizontal(g46)
    c: Coincident(g47,g11)
    c: Coincident(g47,g21)
    c: Horizontal(g47)
FEATURE [Sketcher::SketchObject] Sketch031
  FullyConstrained = true
  Placement = pos=(117,19,0) rot=(0.57735,0.57735,0.57735;2.0944rad)
  sketch-geometry (24):
    g0: ArcOfCircle CenterX=-49.19 CenterY=67.75 CenterZ=0 NormalX=0 NormalY=0 NormalZ=1 AngleXU=0 Radius=1.5 StartAngle=1.5708 EndAngle=4.71239
    g1: ArcOfCircle CenterX=-49.19 CenterY=62 CenterZ=0 NormalX=0 NormalY=0 NormalZ=1 AngleXU=0 Radius=1.5 StartAngle=1.5708 EndAngle=4.71239
    g2: ArcOfCircle CenterX=-49.19 CenterY=56.25 CenterZ=0 NormalX=0 NormalY=0 NormalZ=1 AngleXU=0 Radius=1.5 StartAngle=1.5708 EndAngle=4.71239
    g3: ArcOfCircle CenterX=-49.19 CenterY=50.5 CenterZ=0 NormalX=0 NormalY=0 NormalZ=1 AngleXU=0 Radius=1.5 StartAngle=1.5708 EndAngle=4.71239
    g4: ArcOfCircle CenterX=-49.19 CenterY=44.75 CenterZ=0 NormalX=0 NormalY=0 NormalZ=1 AngleXU=0 Radius=1.5 StartAngle=1.5708 EndAngle=4.71239
    g5: ArcOfCircle CenterX=-49.19 CenterY=39 CenterZ=0 NormalX=0 NormalY=0 NormalZ=1 AngleXU=0 Radius=1.5 StartAngle=1.5708 EndAngle=4.71239
    g6: ArcOfCircle CenterX=-49.19 CenterY=33 CenterZ=0 NormalX=0 NormalY=0 NormalZ=1 AngleXU=0 Radius=1.5 StartAngle=1.5708 EndAngle=4.71239
    g7: ArcOfCircle CenterX=-49.19 CenterY=27.25 CenterZ=0 NormalX=0 NormalY=0 NormalZ=1 AngleXU=0 Radius=1.5 StartAngle=1.5708 EndAngle=4.71239
    g8: ArcOfCircle CenterX=-49.19 CenterY=21.5 CenterZ=0 NormalX=0 NormalY=0 NormalZ=1 AngleXU=0 Radius=1.5 StartAngle=1.5708 EndAngle=4.71239
    g9: ArcOfCircle CenterX=-49.19 CenterY=15.75 CenterZ=0 NormalX=0 NormalY=0 NormalZ=1 AngleXU=0 Radius=1.5 StartAngle=1.5708 EndAngle=4.71239
    g10: ArcOfCircle CenterX=-49.19 CenterY=10 CenterZ=0 NormalX=0 NormalY=0 NormalZ=1 AngleXU=0 Radius=1.5 StartAngle=1.5708 EndAngle=4.71239
    g11: ArcOfCircle CenterX=-49.19 CenterY=4.25 CenterZ=0 NormalX=0 NormalY=0 NormalZ=1 AngleXU=0 Radius=1.5 StartAngle=1.5708 EndAngle=4.71239
    g12: LineSegment StartX=-49.19 StartY=69.25 StartZ=0 EndX=-49.19 EndY=66.25 EndZ=0
    g13: LineSegment StartX=-49.19 StartY=63.5 StartZ=0 EndX=-49.19 EndY=60.5 EndZ=0
    g14: LineSegment StartX=-49.19 StartY=57.75 StartZ=0 EndX=-49.19 EndY=54.75 EndZ=0
    g15: LineSegment StartX=-49.19 StartY=52 StartZ=0 EndX=-49.19 EndY=49 EndZ=0
    g16: LineSegment StartX=-49.19 StartY=46.25 StartZ=0 EndX=-49.19 EndY=43.25 EndZ=0
    g17: LineSegment StartX=-49.19 StartY=40.5 StartZ=0 EndX=-49.19 EndY=37.5 EndZ=0
    g18: LineSegment StartX=-49.19 StartY=34.5 StartZ=0 EndX=-49.19 EndY=31.5 EndZ=0
    g19: LineSegment StartX=-49.19 StartY=28.75 StartZ=0 EndX=-49.19 EndY=25.75 EndZ=0
    g20: LineSegment StartX=-49.19 StartY=23 StartZ=0 EndX=-49.19 EndY=20 EndZ=0
    g21: LineSegment StartX=-49.19 StartY=17.25 StartZ=0 EndX=-49.19 EndY=14.25 EndZ=0
    g22: LineSegment StartX=-49.19 StartY=11.5 StartZ=0 EndX=-49.19 EndY=8.5 EndZ=0
    g23: LineSegment StartX=-49.19 StartY=5.75 StartZ=0 EndX=-49.19 EndY=2.75 EndZ=0
  constraints (48):
    c: Block(g0)
    c: Block(g1)
    c: Block(g2)
    c: Block(g3)
    c: Block(g4)
    c: Block(g5)
    c: Block(g6)
    c: Block(g7)
    c: Block(g8)
    c: Block(g9)
    c: Block(g10)
    c: Block(g11)
    c: Coincident(g12,g0)
    c: Coincident(g12,g0)
    c: Vertical(g12)
    c: Vertical(g13)
    c: Coincident(g13,g1)
    c: Vertical(g14)
    c: Coincident(g14,g2)
    c: Vertical(g15)
    c: Coincident(g15,g3)
    c: Vertical(g16)
    c: Coincident(g16,g4)
    c: Vertical(g17)
    c: Coincident(g17,g5)
    c: Vertical(g18)
    c: Coincident(g18,g6)
    c: Vertical(g19)
    c: Coincident(g19,g7)
    c: Vertical(g20)
    c: Coincident(g20,g8)
    c: Vertical(g21)
    c: Coincident(g21,g9)
    c: Vertical(g22)
    c: Coincident(g22,g10)
    c: Vertical(g23)
    c: Coincident(g23,g11)
    c: Block(g23)
    c: Block(g22)
    c: Block(g21)
    c: Block(g20)
    c: Block(g13)
    c: Block(g14)
    c: Block(g15)
    c: Block(g16)
    c: Block(g17)
    c: Block(g18)
    c: Block(g19)
FEATURE [Part::Extrusion] Extrude022
  Base = -> Sketch030
  Dir = (1,-2e-16,2e-16)
  DirMode = 2
  FaceMakerClass = Part::FaceMakerBullseye
  LengthFwd = 19
  LengthRev = 0
  Placement = pos=(-19,0,0) rot=(0,0,1;0rad)
  Solid = true
  Symmetric = false
FEATURE [Part::Fillet] Fillet022
  Base = -> Extrude022
  Edges = 24 edges r=1.49: [Edge6,Edge11,Edge18,Edge23,Edge30,Edge35,Edge42,Edge47,Edge54,Edge59,Edge66,Edge71,Edge78,Edge83,Edge90,Edge95,Edge102,Edge107,Edge114,Edge119,Edge126,Edge131,Edge138,Edge143]
FEATURE [Part::Cut] Cut020  label="top010"
  Base = -> Cut019
  Tool = -> Fillet022
FEATURE [Sketcher::SketchObject] Sketch032
  FullyConstrained = true
  Placement = pos=(117,19,0) rot=(0.57735,0.57735,0.57735;2.0944rad)
  sketch-geometry (48):
    g0: LineSegment StartX=-49.19 StartY=69.25 StartZ=0 EndX=-49.19 EndY=66.25 EndZ=0
    g1: LineSegment StartX=-49.19 StartY=63.5 StartZ=0 EndX=-49.19 EndY=60.5 EndZ=0
    g2: LineSegment StartX=-49.19 StartY=57.75 StartZ=0 EndX=-49.19 EndY=54.75 EndZ=0
    g3: LineSegment StartX=-49.19 StartY=52 StartZ=0 EndX=-49.19 EndY=49 EndZ=0
    g4: LineSegment StartX=-49.19 StartY=46.25 StartZ=0 EndX=-49.19 EndY=43.25 EndZ=0
    g5: LineSegment StartX=-49.19 StartY=40.5 StartZ=0 EndX=-49.19 EndY=37.5 EndZ=0
    g6: LineSegment StartX=-49.19 StartY=34.5 StartZ=0 EndX=-49.19 EndY=31.5 EndZ=0
    g7: LineSegment StartX=-49.19 StartY=28.75 StartZ=0 EndX=-49.19 EndY=25.75 EndZ=0
    g8: LineSegment StartX=-49.19 StartY=23 StartZ=0 EndX=-49.19 EndY=20 EndZ=0
    g9: LineSegment StartX=-49.19 StartY=17.25 StartZ=0 EndX=-49.19 EndY=14.25 EndZ=0
    g10: LineSegment StartX=-49.19 StartY=11.5 StartZ=0 EndX=-49.19 EndY=8.5 EndZ=0
    g11: LineSegment StartX=-49.19 StartY=5.75 StartZ=0 EndX=-49.19 EndY=2.75 EndZ=0
    g12: ArcOfCircle CenterX=-1.5 CenterY=67.75 CenterZ=0 NormalX=0 NormalY=0 NormalZ=1 AngleXU=0 Radius=1.5 StartAngle=4.71239 EndAngle=7.85398
    g13: ArcOfCircle CenterX=-1.5 CenterY=62 CenterZ=0 NormalX=0 NormalY=0 NormalZ=1 AngleXU=0 Radius=1.5 StartAngle=4.71239 EndAngle=7.85398
    g14: ArcOfCircle CenterX=-1.5 CenterY=56.25 CenterZ=0 NormalX=0 NormalY=0 NormalZ=1 AngleXU=0 Radius=1.5 StartAngle=4.71239 EndAngle=7.85398
    g15: ArcOfCircle CenterX=-11.49 CenterY=50.5 CenterZ=0 NormalX=0 NormalY=0 NormalZ=1 AngleXU=0 Radius=1.5 StartAngle=4.71239 EndAngle=7.85398
    g16: ArcOfCircle CenterX=-16.28 CenterY=44.75 CenterZ=0 NormalX=0 NormalY=0 NormalZ=1 AngleXU=0 Radius=1.5 StartAngle=4.71239 EndAngle=7.85398
    g17: ArcOfCircle CenterX=-18.2337 CenterY=39 CenterZ=0 NormalX=0 NormalY=0 NormalZ=1 AngleXU=0 Radius=1.5 StartAngle=4.71485 EndAngle=7.85398
    g18: ArcOfCircle CenterX=-16.2837 CenterY=27.25 CenterZ=0 NormalX=0 NormalY=0 NormalZ=1 AngleXU=0 Radius=1.5 StartAngle=4.71485 EndAngle=7.85398
    g19: ArcOfCircle CenterX=-18.2337 CenterY=33 CenterZ=0 NormalX=0 NormalY=0 NormalZ=1 AngleXU=0 Radius=1.5 StartAngle=4.71485 EndAngle=7.85398
    g20: ArcOfCircle CenterX=-11.49 CenterY=21.5 CenterZ=0 NormalX=0 NormalY=0 NormalZ=1 AngleXU=0 Radius=1.5 StartAngle=4.71239 EndAngle=7.85398
    g21: ArcOfCircle CenterX=-1.5 CenterY=4.25 CenterZ=0 NormalX=0 NormalY=0 NormalZ=1 AngleXU=0 Radius=1.5 StartAngle=4.71239 EndAngle=7.85398
    g22: ArcOfCircle CenterX=-1.5 CenterY=10 CenterZ=0 NormalX=0 NormalY=0 NormalZ=1 AngleXU=0 Radius=1.5 StartAngle=4.71239 EndAngle=7.85398
    g23: ArcOfCircle CenterX=-1.5 CenterY=15.75 CenterZ=0 NormalX=0 NormalY=0 NormalZ=1 AngleXU=0 Radius=1.5 StartAngle=4.71239 EndAngle=7.85398
    g24: LineSegment StartX=-49.19 StartY=69.25 StartZ=0 EndX=-1.5 EndY=69.25 EndZ=0
    g25: LineSegment StartX=-49.19 StartY=66.25 StartZ=0 EndX=-1.5 EndY=66.25 EndZ=0
    g26: LineSegment StartX=-49.19 StartY=63.5 StartZ=0 EndX=-1.5 EndY=63.5 EndZ=0
    g27: LineSegment StartX=-49.19 StartY=60.5 StartZ=0 EndX=-1.5 EndY=60.5 EndZ=0
    g28: LineSegment StartX=-49.19 StartY=57.75 StartZ=0 EndX=-1.5 EndY=57.75 EndZ=0
    g29: LineSegment StartX=-49.19 StartY=54.75 StartZ=0 EndX=-1.5 EndY=54.75 EndZ=0
    g30: LineSegment StartX=-49.19 StartY=52 StartZ=0 EndX=-11.49 EndY=52 EndZ=0
    g31: LineSegment StartX=-49.19 StartY=49 StartZ=0 EndX=-11.49 EndY=49 EndZ=0
    g32: LineSegment StartX=-49.19 StartY=46.25 StartZ=0 EndX=-16.28 EndY=46.25 EndZ=0
    g33: LineSegment StartX=-49.19 StartY=43.25 StartZ=0 EndX=-16.28 EndY=43.25 EndZ=0
    g34: LineSegment StartX=-49.19 StartY=40.5 StartZ=0 EndX=-18.2337 EndY=40.5 EndZ=0
    g35: LineSegment StartX=-49.19 StartY=37.5 StartZ=0 EndX=-18.23 EndY=37.5 EndZ=0
    g36: LineSegment StartX=-49.19 StartY=34.5 StartZ=0 EndX=-18.2337 EndY=34.5 EndZ=0
    g37: LineSegment StartX=-49.19 StartY=31.5 StartZ=0 EndX=-18.23 EndY=31.5 EndZ=0
    g38: LineSegment StartX=-49.19 StartY=28.75 StartZ=0 EndX=-16.2837 EndY=28.75 EndZ=0
    g39: LineSegment StartX=-49.19 StartY=25.75 StartZ=0 EndX=-16.28 EndY=25.75 EndZ=0
    g40: LineSegment StartX=-49.19 StartY=23 StartZ=0 EndX=-11.49 EndY=23 EndZ=0
    g41: LineSegment StartX=-49.19 StartY=20 StartZ=0 EndX=-11.49 EndY=20 EndZ=0
    g42: LineSegment StartX=-49.19 StartY=17.25 StartZ=0 EndX=-1.5 EndY=17.25 EndZ=0
    g43: LineSegment StartX=-49.19 StartY=14.25 StartZ=0 EndX=-1.5 EndY=14.25 EndZ=0
    g44: LineSegment StartX=-49.19 StartY=11.5 StartZ=0 EndX=-1.5 EndY=11.5 EndZ=0
    g45: LineSegment StartX=-49.19 StartY=8.5 StartZ=0 EndX=-1.5 EndY=8.5 EndZ=0
    g46: LineSegment StartX=-49.19 StartY=5.75 StartZ=0 EndX=-1.5 EndY=5.75 EndZ=0
    g47: LineSegment StartX=-49.19 StartY=2.75 StartZ=0 EndX=-1.5 EndY=2.75 EndZ=0
  constraints (120):
    c: Vertical(g0)
    c: Distance(g0) = 3
    c: Block(g0)
    c: Vertical(g1)
    c: Distance(g1) = 3
    c: Vertical(g2)
    c: Equal(g0,g2) = 3
    c: Block(g2)
    c: Vertical(g3)
    c: Equal(g1,g3) = 3
    c: Vertical(g4)
    c: Equal(g0,g4) = 3
    c: Block(g4)
    c: Vertical(g5)
    c: Equal(g1,g5) = 3
    c: Vertical(g6)
    c: Equal(g0,g6) = 3
    c: Block(g6)
    c: Vertical(g7)
    c: Equal(g1,g7) = 3
    c: Vertical(g8)
    c: Equal(g0,g8) = 3
    c: Block(g8)
    c: Vertical(g9)
    c: Equal(g1,g9) = 3
    c: Vertical(g10)
    c: Equal(g0,g10) = 3
    c: Block(g10)
    c: Vertical(g11)
    c: Equal(g1,g11) = 3
    c: Block(g12)
    c: Block(g13)
    c: Block(g14)
    c: Block(g15)
    c: Block(g16)
    c: Block(g17)
    c: Block(g18)
    c: Block(g19)
    c: Block(g20)
    c: Block(g21)
    c: Block(g22)
    c: Block(g23)
    c: Block(g11)
    c: Block(g9)
    c: Block(g7)
    c: Block(g5)
    c: Block(g3)
    c: Block(g1)
    c: Coincident(g24,g0)
    c: Coincident(g24,g12)
    c: Horizontal(g24)
    c: Coincident(g25,g0)
    c: Coincident(g25,g12)
    c: Horizontal(g25)
    c: Coincident(g26,g1)
    c: Coincident(g26,g13)
    c: Horizontal(g26)
    c: Coincident(g27,g1)
    c: Coincident(g27,g13)
    c: Horizontal(g27)
    c: Coincident(g28,g2)
    c: Coincident(g28,g14)
    c: Horizontal(g28)
    c: Coincident(g29,g2)
    c: Coincident(g29,g14)
    c: Horizontal(g29)
    c: Coincident(g30,g3)
    c: Coincident(g30,g15)
    c: Horizontal(g30)
    c: Coincident(g31,g3)
    c: Coincident(g31,g15)
    c: Horizontal(g31)
    c: Coincident(g32,g4)
    c: Coincident(g32,g16)
    c: Horizontal(g32)
    c: Coincident(g33,g4)
    c: Coincident(g33,g16)
    c: Horizontal(g33)
    c: Coincident(g34,g5)
    c: Coincident(g34,g17)
    c: Horizontal(g34)
    c: Coincident(g35,g5)
    c: Coincident(g35,g17)
    c: Horizontal(g35)
    c: Coincident(g36,g6)
    c: Coincident(g36,g19)
    c: Horizontal(g36)
    c: Coincident(g37,g6)
    c: Coincident(g37,g19)
    c: Horizontal(g37)
    c: Coincident(g38,g7)
    c: Coincident(g38,g18)
    c: Horizontal(g38)
    c: Coincident(g39,g7)
    c: Coincident(g39,g18)
    c: Horizontal(g39)
    c: Coincident(g40,g8)
    c: Coincident(g40,g20)
    c: Horizontal(g40)
    c: Coincident(g41,g8)
    c: Coincident(g41,g20)
    c: Horizontal(g41)
    c: Coincident(g42,g9)
    c: Coincident(g42,g23)
    c: Horizontal(g42)
    c: Coincident(g43,g9)
    c: Coincident(g43,g23)
    c: Horizontal(g43)
    c: Coincident(g44,g10)
    c: Coincident(g44,g22)
    c: Horizontal(g44)
    c: Coincident(g45,g10)
    c: Coincident(g45,g22)
    c: Horizontal(g45)
    c: Coincident(g46,g11)
    c: Coincident(g46,g21)
    c: Horizontal(g46)
    c: Coincident(g47,g11)
    c: Coincident(g47,g21)
    c: Horizontal(g47)
FEATURE [Part::Extrusion] Extrude023
  Base = -> Sketch032
  Dir = (1,-2e-16,2e-16)
  DirMode = 2
  FaceMakerClass = Part::FaceMakerBullseye
  LengthFwd = 19
  LengthRev = 0
  Placement = pos=(-19,0,0) rot=(0,0,1;0rad)
  Solid = true
  Symmetric = false
FEATURE [Part::Fillet] Fillet023
  Base = -> Extrude023
  Edges = <same value as first occurrence — deduplicated (x3 in doc)>
  Placement = pos=(0,0.05,0) rot=(0,0,1;0rad)
FEATURE [Part::Cut] Cut014  label="bottom003"
  Base = -> Cut007
  Tool = -> Fusion047
FEATURE [Part::Cut] Cut021  label="bottom004"
  Base = -> Cut014
  Tool = -> Fillet023
FEATURE [Sketcher::SketchObject] Sketch033
  FullyConstrained = true
  Placement = pos=(117,19,0) rot=(0.57735,0.57735,0.57735;2.0944rad)
  sketch-geometry (8):
    g0: LineSegment StartX=-49.19 StartY=69.25 StartZ=0 EndX=-49.19 EndY=66.25 EndZ=0
    g1: LineSegment StartX=-49.19 StartY=5.75 StartZ=0 EndX=-49.19 EndY=2.75 EndZ=0
    g2: ArcOfCircle CenterX=-1.5 CenterY=67.75 CenterZ=0 NormalX=0 NormalY=0 NormalZ=1 AngleXU=0 Radius=1.5 StartAngle=4.71239 EndAngle=7.85398
    g3: ArcOfCircle CenterX=-1.5 CenterY=4.25 CenterZ=0 NormalX=0 NormalY=0 NormalZ=1 AngleXU=0 Radius=1.5 StartAngle=4.71239 EndAngle=7.85398
    g4: LineSegment StartX=-49.19 StartY=69.25 StartZ=0 EndX=-1.5 EndY=69.25 EndZ=0
    g5: LineSegment StartX=-49.19 StartY=66.25 StartZ=0 EndX=-1.5 EndY=66.25 EndZ=0
    g6: LineSegment StartX=-49.19 StartY=5.75 StartZ=0 EndX=-1.5 EndY=5.75 EndZ=0
    g7: LineSegment StartX=-49.19 StartY=2.75 StartZ=0 EndX=-1.5 EndY=2.75 EndZ=0
  constraints (19):
    c: Vertical(g0)
    c: Distance(g0) = 3
    c: Block(g0)
    c: Vertical(g1)
    c: Block(g2)
    c: Block(g3)
    c: Block(g1)
    c: Coincident(g4,g0)
    c: Coincident(g4,g2)
    c: Horizontal(g4)
    c: Coincident(g5,g0)
    c: Coincident(g5,g2)
    c: Horizontal(g5)
    c: Coincident(g6,g1)
    c: Coincident(g6,g3)
    c: Horizontal(g6)
    c: Coincident(g7,g1)
    c: Coincident(g7,g3)
    c: Horizontal(g7)
FEATURE [Sketcher::SketchObject] Sketch034
  FullyConstrained = true
  Placement = pos=(117,19,0) rot=(0.57735,0.57735,0.57735;2.0944rad)
  sketch-geometry (8):
    g0: LineSegment StartX=-49.19 StartY=63.5 StartZ=0 EndX=-49.19 EndY=60.5 EndZ=0
    g1: LineSegment StartX=-49.19 StartY=11.5 StartZ=0 EndX=-49.19 EndY=8.5 EndZ=0
    g2: ArcOfCircle CenterX=-1.5 CenterY=62 CenterZ=0 NormalX=0 NormalY=0 NormalZ=1 AngleXU=0 Radius=1.5 StartAngle=4.71239 EndAngle=7.85398
    g3: ArcOfCircle CenterX=-1.5 CenterY=10 CenterZ=0 NormalX=0 NormalY=0 NormalZ=1 AngleXU=0 Radius=1.5 StartAngle=4.71239 EndAngle=7.85398
    g4: LineSegment StartX=-49.19 StartY=63.5 StartZ=0 EndX=-1.5 EndY=63.5 EndZ=0
    g5: LineSegment StartX=-49.19 StartY=60.5 StartZ=0 EndX=-1.5 EndY=60.5 EndZ=0
    g6: LineSegment StartX=-49.19 StartY=11.5 StartZ=0 EndX=-1.5 EndY=11.5 EndZ=0
    g7: LineSegment StartX=-49.19 StartY=8.5 StartZ=0 EndX=-1.5 EndY=8.5 EndZ=0
  constraints (19):
    c: Vertical(g0)
    c: Distance(g0) = 3
    c: Vertical(g1)
    c: Block(g1)
    c: Block(g2)
    c: Block(g3)
    c: Block(g0)
    c: Coincident(g4,g0)
    c: Coincident(g4,g2)
    c: Horizontal(g4)
    c: Coincident(g5,g0)
    c: Coincident(g5,g2)
    c: Horizontal(g5)
    c: Coincident(g6,g1)
    c: Coincident(g6,g3)
    c: Horizontal(g6)
    c: Coincident(g7,g1)
    c: Coincident(g7,g3)
    c: Horizontal(g7)
FEATURE [Part::Extrusion] Extrude024
  Base = -> Sketch033
  Dir = (1,0,0)
  DirMode = 2
  FaceMakerClass = Part::FaceMakerBullseye
  LengthFwd = 10
  LengthRev = 0
  Solid = true
  Symmetric = false
FEATURE [Part::Extrusion] Extrude025
  Base = -> Sketch034
  Dir = (1,0,0)
  DirMode = 2
  FaceMakerClass = Part::FaceMakerBullseye
  LengthFwd = 10
  LengthRev = 0
  Solid = true
  Symmetric = false
FEATURE [Part::Fillet] Fillet024  label="removeFromtMoreFrontCaseScrewRetainers"
  Base = -> Extrude024
  Edges = 4 edges r=1.49: [Edge6,Edge11,Edge18,Edge23]
  Placement = pos=(-11,0,0) rot=(0,0,1;0rad)
FEATURE [Part::Fillet] Fillet025  label="removeFromtMoreFrontCaseScrewRetainers001"
  Base = -> Extrude025
  Edges = 4 edges r=1.49: [Edge6,Edge11,Edge18,Edge23]
  Placement = pos=(-19,0,0) rot=(0,0,1;0rad)
FEATURE [Part::Cut] Cut022
  Base = -> Cut015
  Tool = -> Fillet025
FEATURE [Part::Cut] Cut023  label="screwRetainers"
  Base = -> Cut022
  Tool = -> Fillet024
FEATURE [Part::MultiFuse] Fusion056  label="bottom005"
  Shapes = -> [Fusion044,Cut021]
FEATURE [Part::MultiFuse] Fusion057  label="casePillars001"
  Shapes = -> [Cut016,Fusion052]
FEATURE [Part::MultiFuse] Fusion058  label="bottom006"
  Shapes = -> [Fusion056,Cut023]
FEATURE [Part::MultiFuse] Fusion059  label="bottom007"
  Shapes = -> [Fusion058,Fillet005]
FEATURE [Part::MultiFuse] Fusion060  label="bottom008"
  Shapes = -> [Fusion059,Fusion]
FEATURE [Part::MultiFuse] Fusion061  label="top011"
  Shapes = -> [Cut006,Cut020]
FEATURE [Part::MultiFuse] Fusion062  label="top012"
  Shapes = -> [Fusion057,Fusion061]
FEATURE [Sketcher::SketchObject] Sketch035  label="topSketch007"
  FullyConstrained = true
  sketch-geometry (6):
    g0: LineSegment StartX=19 StartY=38 StartZ=0 EndX=117 EndY=38 EndZ=0
    g1: ArcOfCircle CenterX=19 CenterY=19 CenterZ=0 NormalX=0 NormalY=0 NormalZ=1 AngleXU=0 Radius=19 StartAngle=1.5708 EndAngle=3.14159
    g2: LineSegment StartX=117 StartY=38 StartZ=0 EndX=117 EndY=19 EndZ=0
    g3: LineSegment StartX=98 StartY=1.0161e-12 StartZ=0 EndX=5.22862e-06 EndY=1.0161e-12 EndZ=0
    g4: LineSegment StartX=5.22862e-06 StartY=19 StartZ=0 EndX=5.22862e-06 EndY=1.0161e-12 EndZ=0
    g5: ArcOfCircle CenterX=98 CenterY=19 CenterZ=0 NormalX=0 NormalY=0 NormalZ=1 AngleXU=0 Radius=19 StartAngle=4.71239 EndAngle=6.28319
  constraints (16):
    c: Horizontal(g0)
    c: Distance(g0) = 98
    c: Coincident(g1,g0)
    c: Block(g1)
    c: Coincident(g2,g0)
    c: Vertical(g2)
    c: Distance(g2) = 19
    c: Horizontal(g3)
    c: Coincident(g4,g1)
    c: Vertical(g4)
    c: Coincident(g3,g4)
    c: Block(g3)
    c: Coincident(g5,g2)
    c: Coincident(g5,g3)
    c: Block(g0)
    c: Block(g5)
FEATURE [Part::Extrusion] Extrude026  label="sideA001"
  Base = -> Sketch035
  Dir = (0,0,1)
  DirMode = 2
  FaceMakerClass = Part::FaceMakerBullseye
  LengthFwd = 3
  LengthRev = 0
  Placement = pos=(0,0,-2.7) rot=(0,0,1;0rad)
  Solid = true
  Symmetric = false
FEATURE [Sketcher::SketchObject] Sketch036  label="topSketch008"
  FullyConstrained = true
  sketch-geometry (6):
    g0: LineSegment StartX=19 StartY=38 StartZ=0 EndX=117 EndY=38 EndZ=0
    g1: ArcOfCircle CenterX=19 CenterY=19 CenterZ=0 NormalX=0 NormalY=0 NormalZ=1 AngleXU=0 Radius=19 StartAngle=1.5708 EndAngle=3.14159
    g2: LineSegment StartX=117 StartY=38 StartZ=0 EndX=117 EndY=19 EndZ=0
    g3: LineSegment StartX=98 StartY=1.0161e-12 StartZ=0 EndX=5.22862e-06 EndY=1.0161e-12 EndZ=0
    g4: LineSegment StartX=5.22862e-06 StartY=19 StartZ=0 EndX=5.22862e-06 EndY=1.0161e-12 EndZ=0
    g5: ArcOfCircle CenterX=98 CenterY=19 CenterZ=0 NormalX=0 NormalY=0 NormalZ=1 AngleXU=0 Radius=19 StartAngle=4.71239 EndAngle=6.28319
  constraints (16):
    c: Horizontal(g0)
    c: Distance(g0) = 98
    c: Coincident(g1,g0)
    c: Block(g1)
    c: Coincident(g2,g0)
    c: Vertical(g2)
    c: Distance(g2) = 19
    c: Horizontal(g3)
    c: Coincident(g4,g1)
    c: Vertical(g4)
    c: Coincident(g3,g4)
    c: Block(g3)
    c: Coincident(g5,g2)
    c: Coincident(g5,g3)
    c: Block(g0)
    c: Block(g5)
FEATURE [Part::Extrusion] Extrude027  label="sideB001"
  Base = -> Sketch036
  Dir = (0,0,1)
  DirMode = 2
  FaceMakerClass = Part::FaceMakerBullseye
  LengthFwd = 3
  LengthRev = 0
  Placement = pos=(0,0,71.7) rot=(0,0,1;0rad)
  Solid = true
  Symmetric = false
FEATURE [Part::MultiFuse] Fusion064  label="removeFromBottom"
  Shapes = -> [Extrude026,Extrude027]
FEATURE [Part::Cut] Cut024  label="bottom009"
  Base = -> Fusion060
  Tool = -> Fusion064
FEATURE [Sketcher::SketchObject] Sketch037  label="topSketch009"
  FullyConstrained = true
  sketch-geometry (6):
    g0: ArcOfCircle CenterX=19 CenterY=19 CenterZ=0 NormalX=0 NormalY=0 NormalZ=1 AngleXU=0 Radius=19 StartAngle=1.5708 EndAngle=3.14159
    g1: LineSegment StartX=5.22862e-06 StartY=19 StartZ=0 EndX=5.22862e-06 EndY=1.19904e-11 EndZ=0
    g2: LineSegment StartX=19 StartY=38 StartZ=0 EndX=124 EndY=38 EndZ=0
    g3: LineSegment StartX=5.22862e-06 StartY=1.19904e-11 StartZ=0 EndX=105 EndY=1.19904e-11 EndZ=0
    g4: ArcOfCircle CenterX=105 CenterY=19 CenterZ=0 NormalX=0 NormalY=0 NormalZ=1 AngleXU=0 Radius=19 StartAngle=4.71239 EndAngle=6.28319
    g5: LineSegment StartX=124 StartY=38 StartZ=0 EndX=124 EndY=19 EndZ=0
  constraints (16):
    c: Block(g0)
    c: Coincident(g1,g0)
    c: Vertical(g1)
    c: Horizontal(g2)
    c: Distance(g2) = 105
    c: Coincident(g2,g0)
    c: Distance(g1) = 19
    c: Coincident(g3,g1)
    c: Horizontal(g3)
    c: Distance(g3) = 105
    c: Block(g4)
    c: Coincident(g4,g3)
    c: Coincident(g5,g2)
    c: Coincident(g5,g4)
    c: Vertical(g5)
    c: Distance(g5) = 19
FEATURE [Part::Extrusion] Extrude028  label="sideB"
  Base = -> Sketch037
  Dir = (0,0,1)
  DirMode = 2
  FaceMakerClass = Part::FaceMakerBullseye
  LengthFwd = 3
  LengthRev = 0
  Placement = pos=(0,0,72) rot=(0,0,1;0rad)
  Solid = true
  Symmetric = false
FEATURE [Sketcher::SketchObject] Sketch038  label="topSketch010"
  FullyConstrained = true
  sketch-geometry (20):
    g0: LineSegment StartX=5.21097e-06 StartY=3 StartZ=0 EndX=5.21097e-06 EndY=19 EndZ=0
    g1: ArcOfCircle CenterX=19 CenterY=19 CenterZ=0 NormalX=0 NormalY=0 NormalZ=1 AngleXU=0 Radius=19 StartAngle=1.5708 EndAngle=3.14159
    g2: ArcOfCircle CenterX=19 CenterY=19 CenterZ=0 NormalX=0 NormalY=0 NormalZ=1 AngleXU=0 Radius=16 StartAngle=1.5708 EndAngle=3.14159
    g3: LineSegment StartX=114 StartY=35 StartZ=0 EndX=19 EndY=35 EndZ=0
    g4: LineSegment StartX=5.21097e-06 StartY=3 StartZ=0 EndX=5.21097e-06 EndY=0 EndZ=0
    g5: LineSegment StartX=3 StartY=0 StartZ=0 EndX=5.21097e-06 EndY=0 EndZ=0
    g6: LineSegment StartX=3 StartY=19 StartZ=0 EndX=3 EndY=0 EndZ=0
    g7: LineSegment StartX=19 StartY=38 StartZ=0 EndX=124 EndY=38 EndZ=0
    g8: Circle CenterX=119 CenterY=35 CenterZ=0 NormalX=0 NormalY=0 NormalZ=1 AngleXU=0 Radius=1
    g9: Circle CenterX=121 CenterY=35 CenterZ=0 NormalX=0 NormalY=0 NormalZ=1 AngleXU=0 Radius=1
    g10: Circle CenterX=121 CenterY=33 CenterZ=0 NormalX=0 NormalY=0 NormalZ=1 AngleXU=0 Radius=1
    g11: BSplineCurve PolesCount=3 KnotsCount=2 Degree=2 IsPeriodic=0
    g12: GeomPoint X=119 Y=35 Z=0
    g13: GeomPoint X=121 Y=33 Z=0
    g14: LineSegment StartX=119 StartY=35 StartZ=0 EndX=114 EndY=35 EndZ=0
    g15: ArcOfCircle CenterX=105 CenterY=19 CenterZ=0 NormalX=0 NormalY=0 NormalZ=1 AngleXU=0 Radius=19 StartAngle=5.7297 EndAngle=6.28319
    g16: ArcOfCircle CenterX=105 CenterY=19 CenterZ=0 NormalX=0 NormalY=0 NormalZ=1 AngleXU=0 Radius=16 StartAngle=5.60905 EndAngle=6.28319
    g17: LineSegment StartX=121 StartY=33 StartZ=0 EndX=121 EndY=19 EndZ=0
    g18: LineSegment StartX=124 StartY=38 StartZ=0 EndX=124 EndY=19 EndZ=0
    g19: LineSegment StartX=117.5 StartY=9.01251 StartZ=0 EndX=121.163 EndY=9.0125 EndZ=0
  constraints (46):
    c: Vertical(g0)
    c: Block(g0)
    c: Coincident(g1,g0)
    c: Block(g1)
    c: Coincident(g2,g1)
    c: Block(g2)
    c: Coincident(g3,g2)
    c: Horizontal(g3)
    c: Tangent(g3,g2)
    c: Coincident(g4,g0)
    c: Distance(g4) = 3
    c: Vertical(g4)
    c: Coincident(g5,g4)
    c: Horizontal(g5)
    c: Coincident(g6,g2)
    c: Coincident(g6,g5)
    c: Vertical(g6)
    c: Horizontal(g7)
    c: Distance(g7) = 105
    c: Coincident(g7,g1)
    c: Block(g3)
    c: Weight(g8) = 1
    c: Equal(g8,g9)
    c: Equal(g8,g10)
    c: InternalAlignment(g8,g11)
    c: InternalAlignment(g9,g11)
    c: InternalAlignment(g10,g11)
    c: InternalAlignment(g12,g11)
    c: InternalAlignment(g13,g11)
    c: Block(g11)
    c: Coincident(g14,g11)
    c: Coincident(g14,g3)
    c: Horizontal(g14)
    c: Block(g15)
    c: Coincident(g16,g15)
    c: Block(g16)
    c: Coincident(g17,g11)
    c: Coincident(g17,g16)
    c: Vertical(g17)
    c: Distance(g17) = 14
    c: Coincident(g18,g7)
    c: Coincident(g18,g15)
    c: Vertical(g18)
    c: Distance(g18) = 19
    c: Coincident(g19,g16)
    c: Coincident(g19,g15)
FEATURE [Part::Extrusion] Extrude029
  Base = -> Sketch038
  Dir = (0,0,1)
  DirMode = 2
  FaceMakerClass = Part::FaceMakerBullseye
  LengthFwd = 72
  LengthRev = 0
  Solid = true
  Symmetric = false
FEATURE [Part::Feature] Face085
  shape: bbox 4.8 x 25.5 x 2e-07 mm, 1 faces, 0 solids (baked)
FEATURE [Part::Revolution] Revolve089  label="moreFrontCaseScrewPost003"
  Angle = 360
  Axis = (0,1,0)
  Base = (0,0,0)
  FaceMakerClass = Part::FaceMakerBullseye
  Placement = pos=(109.5,4.5,3.5) rot=(0,0,1;0rad)
  Solid = false
  Source = -> Face085
  Symmetric = false
FEATURE [Part::Feature] Face086
  shape: bbox 4.8 x 25.5 x 2e-07 mm, 1 faces, 0 solids (baked)
FEATURE [Part::Revolution] Revolve090  label="moreFrontCaseScrewPost004"
  Angle = 360
  Axis = (0,1,0)
  Base = (0,0,0)
  FaceMakerClass = Part::FaceMakerBullseye
  Placement = pos=(109.5,4.5,68.5) rot=(0,0,1;0rad)
  Solid = false
  Source = -> Face086
  Symmetric = false
FEATURE [Part::Fillet] Fillet026  label="top013"
  Base = -> Extrude029
  Edges = 1 edges r=2: [Edge35]
FEATURE [Sketcher::SketchObject] Sketch039
  FullyConstrained = true
  sketch-geometry (7):
    g0: LineSegment StartX=0 StartY=0 StartZ=0 EndX=0 EndY=6 EndZ=0
    g1: Circle CenterX=0 CenterY=0 CenterZ=0 NormalX=0 NormalY=0 NormalZ=1 AngleXU=0 Radius=1
    g2: Circle CenterX=8 CenterY=6 CenterZ=0 NormalX=0 NormalY=0 NormalZ=1 AngleXU=0 Radius=1
    g3: BSplineCurve PolesCount=3 KnotsCount=2 Degree=2 IsPeriodic=0
    g4: GeomPoint X=0 Y=0 Z=0
    g5: GeomPoint X=8 Y=6 Z=0
    g6: LineSegment StartX=0 StartY=6 StartZ=0 EndX=8 EndY=6 EndZ=0
  constraints (14):
    c: Coincident(g0,g-1)
    c: Distance(g0) = 6
    c: Vertical(g0)
    c: Coincident(g3,g0)
    c: Weight(g1) = 1
    c: Equal(g1,g2)
    c: InternalAlignment(g1,g3)
    c: InternalAlignment(g2,g3)
    c: InternalAlignment(g4,g3)
    c: InternalAlignment(g5,g3)
    c: Block(g3)
    c: Coincident(g6,g0)
    c: Coincident(g6,g3)
    c: Horizontal(g6)
FEATURE [Sketcher::SketchObject] Sketch040
  FullyConstrained = true
  sketch-geometry (7):
    g0: LineSegment StartX=0 StartY=0 StartZ=0 EndX=0 EndY=6 EndZ=0
    g1: Circle CenterX=0 CenterY=0 CenterZ=0 NormalX=0 NormalY=0 NormalZ=1 AngleXU=0 Radius=1
    g2: Circle CenterX=8 CenterY=6 CenterZ=0 NormalX=0 NormalY=0 NormalZ=1 AngleXU=0 Radius=1
    g3: BSplineCurve PolesCount=3 KnotsCount=2 Degree=2 IsPeriodic=0
    g4: GeomPoint X=0 Y=0 Z=0
    g5: GeomPoint X=8 Y=6 Z=0
    g6: LineSegment StartX=0 StartY=6 StartZ=0 EndX=8 EndY=6 EndZ=0
  constraints (14):
    c: Coincident(g0,g-1)
    c: Distance(g0) = 6
    c: Vertical(g0)
    c: Coincident(g3,g0)
    c: Weight(g1) = 1
    c: Equal(g1,g2)
    c: InternalAlignment(g1,g3)
    c: InternalAlignment(g2,g3)
    c: InternalAlignment(g4,g3)
    c: InternalAlignment(g5,g3)
    c: Block(g3)
    c: Coincident(g6,g0)
    c: Coincident(g6,g3)
    c: Horizontal(g6)
FEATURE [Sketcher::SketchObject] Sketch041
  FullyConstrained = true
  sketch-geometry (7):
    g0: LineSegment StartX=0 StartY=0 StartZ=0 EndX=0 EndY=6 EndZ=0
    g1: Circle CenterX=0 CenterY=0 CenterZ=0 NormalX=0 NormalY=0 NormalZ=1 AngleXU=0 Radius=1
    g2: Circle CenterX=8 CenterY=6 CenterZ=0 NormalX=0 NormalY=0 NormalZ=1 AngleXU=0 Radius=1
    g3: BSplineCurve PolesCount=3 KnotsCount=2 Degree=2 IsPeriodic=0
    g4: GeomPoint X=0 Y=0 Z=0
    g5: GeomPoint X=8 Y=6 Z=0
    g6: LineSegment StartX=0 StartY=6 StartZ=0 EndX=8 EndY=6 EndZ=0
  constraints (14):
    c: Coincident(g0,g-1)
    c: Distance(g0) = 6
    c: Vertical(g0)
    c: Coincident(g3,g0)
    c: Weight(g1) = 1
    c: Equal(g1,g2)
    c: InternalAlignment(g1,g3)
    c: InternalAlignment(g2,g3)
    c: InternalAlignment(g4,g3)
    c: InternalAlignment(g5,g3)
    c: Block(g3)
    c: Coincident(g6,g0)
    c: Coincident(g6,g3)
    c: Horizontal(g6)
FEATURE [Sketcher::SketchObject] Sketch042
  FullyConstrained = true
  sketch-geometry (7):
    g0: LineSegment StartX=0 StartY=0 StartZ=0 EndX=0 EndY=6 EndZ=0
    g1: Circle CenterX=0 CenterY=0 CenterZ=0 NormalX=0 NormalY=0 NormalZ=1 AngleXU=0 Radius=1
    g2: Circle CenterX=8 CenterY=6 CenterZ=0 NormalX=0 NormalY=0 NormalZ=1 AngleXU=0 Radius=1
    g3: BSplineCurve PolesCount=3 KnotsCount=2 Degree=2 IsPeriodic=0
    g4: GeomPoint X=0 Y=0 Z=0
    g5: GeomPoint X=8 Y=6 Z=0
    g6: LineSegment StartX=0 StartY=6 StartZ=0 EndX=8 EndY=6 EndZ=0
  constraints (14):
    c: Coincident(g0,g-1)
    c: Distance(g0) = 6
    c: Vertical(g0)
    c: Coincident(g3,g0)
    c: Weight(g1) = 1
    c: Equal(g1,g2)
    c: InternalAlignment(g1,g3)
    c: InternalAlignment(g2,g3)
    c: InternalAlignment(g4,g3)
    c: InternalAlignment(g5,g3)
    c: Block(g3)
    c: Coincident(g6,g0)
    c: Coincident(g6,g3)
    c: Horizontal(g6)
FEATURE [Part::Extrusion] Extrude030  label="caseScrewPillarBracket008"
  Base = -> Sketch039
  Dir = (0,0,1)
  DirMode = 2
  FaceMakerClass = Part::FaceMakerBullseye
  LengthFwd = 2.4
  LengthRev = 0
  Placement = pos=(15.76,29,8.8) rot=(0,1,0;0rad)
  Solid = true
  Symmetric = false
FEATURE [Part::Extrusion] Extrude031  label="caseScrewPillarBracket009"
  Base = -> Sketch040
  Dir = (0,0,1)
  DirMode = 2
  FaceMakerClass = Part::FaceMakerBullseye
  LengthFwd = 2.4
  LengthRev = 0
  Placement = pos=(15.76,29,60.8) rot=(0,0,1;0rad)
  Solid = true
  Symmetric = false
FEATURE [Part::Extrusion] Extrude032  label="caseScrewPillarBracket010"
  Base = -> Sketch041
  Dir = (0,0,1)
  DirMode = 2
  FaceMakerClass = Part::FaceMakerBullseye
  LengthFwd = 2.4
  LengthRev = 0
  Placement = pos=(13.7,29,13.26) rot=(0,-1,0;1.5708rad)
  Solid = true
  Symmetric = false
FEATURE [Part::Extrusion] Extrude033  label="caseScrewPillarBracket011"
  Base = -> Sketch042
  Dir = (0,0,1)
  DirMode = 2
  FaceMakerClass = Part::FaceMakerBullseye
  LengthFwd = 2.4
  LengthRev = 0
  Placement = pos=(11.3,29,58.74) rot=(0,1,0;1.5708rad)
  Solid = true
  Symmetric = false
FEATURE [Sketcher::SketchObject] Sketch043
  FullyConstrained = true
  sketch-geometry (7):
    g0: LineSegment StartX=0 StartY=0 StartZ=0 EndX=0 EndY=6 EndZ=0
    g1: Circle CenterX=0 CenterY=0 CenterZ=0 NormalX=0 NormalY=0 NormalZ=1 AngleXU=0 Radius=1
    g2: Circle CenterX=8 CenterY=6 CenterZ=0 NormalX=0 NormalY=0 NormalZ=1 AngleXU=0 Radius=1
    g3: BSplineCurve PolesCount=3 KnotsCount=2 Degree=2 IsPeriodic=0
    g4: GeomPoint X=0 Y=0 Z=0
    g5: GeomPoint X=8 Y=6 Z=0
    g6: LineSegment StartX=0 StartY=6 StartZ=0 EndX=8 EndY=6 EndZ=0
  constraints (14):
    c: Coincident(g0,g-1)
    c: Distance(g0) = 6
    c: Vertical(g0)
    c: Coincident(g3,g0)
    c: Weight(g1) = 1
    c: Equal(g1,g2)
    c: InternalAlignment(g1,g3)
    c: InternalAlignment(g2,g3)
    c: InternalAlignment(g4,g3)
    c: InternalAlignment(g5,g3)
    c: Block(g3)
    c: Coincident(g6,g0)
    c: Coincident(g6,g3)
    c: Horizontal(g6)
FEATURE [Part::Extrusion] Extrude034  label="caseScrewPillarBracket012"
  Base = -> Sketch043
  Dir = (0,0,1)
  DirMode = 2
  FaceMakerClass = Part::FaceMakerBullseye
  LengthFwd = 2.4
  LengthRev = 0
  Placement = pos=(88.3,29,65.23) rot=(0,1,0;1.5708rad)
  Solid = true
  Symmetric = false
FEATURE [Sketcher::SketchObject] Sketch044
  FullyConstrained = true
  sketch-geometry (7):
    g0: LineSegment StartX=0 StartY=0 StartZ=0 EndX=0 EndY=6 EndZ=0
    g1: Circle CenterX=0 CenterY=0 CenterZ=0 NormalX=0 NormalY=0 NormalZ=1 AngleXU=0 Radius=1
    g2: Circle CenterX=8 CenterY=6 CenterZ=0 NormalX=0 NormalY=0 NormalZ=1 AngleXU=0 Radius=1
    g3: BSplineCurve PolesCount=3 KnotsCount=2 Degree=2 IsPeriodic=0
    g4: GeomPoint X=0 Y=0 Z=0
    g5: GeomPoint X=8 Y=6 Z=0
    g6: LineSegment StartX=0 StartY=6 StartZ=0 EndX=8 EndY=6 EndZ=0
  constraints (14):
    c: Coincident(g0,g-1)
    c: Distance(g0) = 6
    c: Vertical(g0)
    c: Coincident(g3,g0)
    c: Weight(g1) = 1
    c: Equal(g1,g2)
    c: InternalAlignment(g1,g3)
    c: InternalAlignment(g2,g3)
    c: InternalAlignment(g4,g3)
    c: InternalAlignment(g5,g3)
    c: Block(g3)
    c: Coincident(g6,g0)
    c: Coincident(g6,g3)
    c: Horizontal(g6)
FEATURE [Part::Extrusion] Extrude035  label="caseScrewPillarBracket013"
  Base = -> Sketch044
  Dir = (0,0,1)
  DirMode = 2
  FaceMakerClass = Part::FaceMakerBullseye
  LengthFwd = 2.4
  LengthRev = 0
  Placement = pos=(90.7,29,6.77) rot=(0,-1,0;1.5708rad)
  Solid = true
  Symmetric = false
FEATURE [Sketcher::SketchObject] Sketch045
  FullyConstrained = true
  sketch-geometry (7):
    g0: LineSegment StartX=0 StartY=0 StartZ=0 EndX=0 EndY=6 EndZ=0
    g1: Circle CenterX=0 CenterY=0 CenterZ=0 NormalX=0 NormalY=0 NormalZ=1 AngleXU=0 Radius=1
    g2: Circle CenterX=8 CenterY=6 CenterZ=0 NormalX=0 NormalY=0 NormalZ=1 AngleXU=0 Radius=1
    g3: BSplineCurve PolesCount=3 KnotsCount=2 Degree=2 IsPeriodic=0
    g4: GeomPoint X=0 Y=0 Z=0
    g5: GeomPoint X=8 Y=6 Z=0
    g6: LineSegment StartX=0 StartY=6 StartZ=0 EndX=8 EndY=6 EndZ=0
  constraints (14):
    c: Coincident(g0,g-1)
    c: Distance(g0) = 6
    c: Vertical(g0)
    c: Coincident(g3,g0)
    c: Weight(g1) = 1
    c: Equal(g1,g2)
    c: InternalAlignment(g1,g3)
    c: InternalAlignment(g2,g3)
    c: InternalAlignment(g4,g3)
    c: InternalAlignment(g5,g3)
    c: Block(g3)
    c: Coincident(g6,g0)
    c: Coincident(g6,g3)
    c: Horizontal(g6)
FEATURE [Sketcher::SketchObject] Sketch046
  FullyConstrained = true
  sketch-geometry (7):
    g0: LineSegment StartX=0 StartY=0 StartZ=0 EndX=0 EndY=6 EndZ=0
    g1: Circle CenterX=0 CenterY=0 CenterZ=0 NormalX=0 NormalY=0 NormalZ=1 AngleXU=0 Radius=1
    g2: Circle CenterX=8 CenterY=6 CenterZ=0 NormalX=0 NormalY=0 NormalZ=1 AngleXU=0 Radius=1
    g3: BSplineCurve PolesCount=3 KnotsCount=2 Degree=2 IsPeriodic=0
    g4: GeomPoint X=0 Y=0 Z=0
    g5: GeomPoint X=8 Y=6 Z=0
    g6: LineSegment StartX=0 StartY=6 StartZ=0 EndX=8 EndY=6 EndZ=0
  constraints (14):
    c: Coincident(g0,g-1)
    c: Distance(g0) = 6
    c: Vertical(g0)
    c: Coincident(g3,g0)
    c: Weight(g1) = 1
    c: Equal(g1,g2)
    c: InternalAlignment(g1,g3)
    c: InternalAlignment(g2,g3)
    c: InternalAlignment(g4,g3)
    c: InternalAlignment(g5,g3)
    c: Block(g3)
    c: Coincident(g6,g0)
    c: Coincident(g6,g3)
    c: Horizontal(g6)
FEATURE [Part::Extrusion] Extrude036  label="caseScrewPillarBracket014"
  Base = -> Sketch045
  Dir = (0,0,1)
  DirMode = 2
  FaceMakerClass = Part::FaceMakerBullseye
  LengthFwd = 2.4
  LengthRev = 0
  Placement = pos=(110.7,29,6.77) rot=(0,-1,0;1.5708rad)
  Solid = true
  Symmetric = false
FEATURE [Part::Extrusion] Extrude037  label="caseScrewPillarBracket015"
  Base = -> Sketch046
  Dir = (0,0,1)
  DirMode = 2
  FaceMakerClass = Part::FaceMakerBullseye
  LengthFwd = 2.4
  LengthRev = 0
  Placement = pos=(108.3,29,65.23) rot=(0,1,0;1.5708rad)
  Solid = true
  Symmetric = false
FEATURE [Part::Box] Box013  label="frontCaseScrewPillarBracket002"
  AttacherType = Attacher::AttachEngine3D
  Height = 2.4
  Length = 22
  Placement = pos=(87,28,2.3) rot=(0,0,1;0rad)
  Width = 7
FEATURE [Part::Box] Box014  label="frontCaseScrewPillarBracket003"
  AttacherType = Attacher::AttachEngine3D
  Height = 2.4
  Length = 22
  Placement = pos=(87,28,67.3) rot=(0,0,1;0rad)
  Width = 7
FEATURE [Part::Feature] Face087
  shape: bbox 4.8 x 30.2 x 2e-07 mm, 1 faces, 0 solids (baked)
FEATURE [Part::Revolution] Revolve091  label="frontCaseScrewPost004"
  Angle = 360
  Axis = (0,1,0)
  Base = (0,0,0)
  FaceMakerClass = Part::FaceMakerBullseye
  Placement = pos=(89.5,4.5,3.5) rot=(0,0,1;0rad)
  Solid = false
  Source = -> Face087
  Symmetric = false
FEATURE [Part::Feature] Face088
  shape: bbox 4.8 x 30.2 x 2e-07 mm, 1 faces, 0 solids (baked)
FEATURE [Part::Revolution] Revolve092  label="frontCaseScrewPost005"
  Angle = 360
  Axis = (0,1,0)
  Base = (0,0,0)
  FaceMakerClass = Part::FaceMakerBullseye
  Placement = pos=(89.5,4.5,68.5) rot=(0,0,1;0rad)
  Solid = false
  Source = -> Face088
  Symmetric = false
FEATURE [Part::Feature] Face089
  shape: bbox 3.5 x 30.2 x 2e-07 mm, 1 faces, 0 solids (baked)
FEATURE [Part::Revolution] Revolve093  label="backCaseScrewPost002"
  Angle = 360
  Axis = (0,1,0)
  Base = (0,0,0)
  FaceMakerClass = Part::FaceMakerBullseye
  Placement = pos=(12.5,4.5,10) rot=(0,0,1;0rad)
  Solid = false
  Source = -> Face089
  Symmetric = false
FEATURE [Part::Feature] Face090
  shape: bbox 3.5 x 30.2 x 2e-07 mm, 1 faces, 0 solids (baked)
FEATURE [Part::Revolution] Revolve094  label="backCaseScrewPost003"
  Angle = 360
  Axis = (0,1,0)
  Base = (0,0,0)
  FaceMakerClass = Part::FaceMakerBullseye
  Placement = pos=(12.5,4.5,62) rot=(0,0,1;0rad)
  Solid = false
  Source = -> Face090
  Symmetric = false
FEATURE [Part::Box] Box015  label="Cube011"
  AttacherType = Attacher::AttachEngine3D
  Height = 28.8
  Length = 3
  Placement = pos=(107.3,28,21.6) rot=(0,0,1;0rad)
  Width = 7
FEATURE [Part::Box] Box016  label="Cube012"
  AttacherType = Attacher::AttachEngine3D
  Height = 3
  Length = 7.4
  Placement = pos=(107.3,28,18.6) rot=(0,0,1;0rad)
  Width = 7
FEATURE [Part::Box] Box017  label="Cube013"
  AttacherType = Attacher::AttachEngine3D
  Height = 3
  Length = 7.4
  Placement = pos=(107.3,28,50.4) rot=(0,0,1;0rad)
  Width = 7
FEATURE [Part::Cylinder] Cylinder024
  Angle = 360
  AttacherType = Attacher::AttachEngine3D
  Height = 20
  Placement = pos=(0,0,36.15) rot=(0,0,1;0rad)
  Radius = 14.3
FEATURE [Part::Cylinder] Cylinder025
  Angle = 360
  AttacherType = Attacher::AttachEngine3D
  Height = 10
  Placement = pos=(0,0,36.15) rot=(0,0,1;0rad)
  Radius = 4
FEATURE [Part::MultiFuse] Fusion066  label="removeToCreteHoleForPlugHousing009"
  Placement = pos=(70,19,36) rot=(0,1,0;1.5708rad)
  Shapes = -> [Cylinder024,Cylinder025]
FEATURE [Part::MultiFuse] Fusion065  label="plugHousingBracketHolder002"
  Shapes = -> [Box017,Box015,Box016]
FEATURE [Part::Cut] Cut025  label="plugHousingBracketHolder003"
  Base = -> Fusion065
  Placement = pos=(7,0,0) rot=(0,0,1;0rad)
  Tool = -> Fusion066
FEATURE [Sketcher::SketchObject] Sketch047
  FullyConstrained = false
  Placement = pos=(0,0,0) rot=(1,0,0;1.5708rad)
  sketch-geometry (24):
    g0: ArcOfCircle CenterX=-4 CenterY=-10.5 CenterZ=0 NormalX=0 NormalY=0 NormalZ=1 AngleXU=0 Radius=1.5 StartAngle=6e-16 EndAngle=3.14159
    g1: ArcOfCircle CenterX=-34.2 CenterY=-10.5 CenterZ=0 NormalX=0 NormalY=0 NormalZ=1 AngleXU=0 Radius=1.5 StartAngle=0 EndAngle=3.14159
    g2: ArcOfCircle CenterX=-34.2 CenterY=-27.7 CenterZ=0 NormalX=0 NormalY=0 NormalZ=1 AngleXU=0 Radius=1.5 StartAngle=3.14159 EndAngle=6.28319
    g3: ArcOfCircle CenterX=-4 CenterY=-27.7 CenterZ=0 NormalX=0 NormalY=0 NormalZ=1 AngleXU=0 Radius=1.5 StartAngle=3.1416 EndAngle=6.28319
    g4: ArcOfCircle CenterX=-10 CenterY=-4.3 CenterZ=0 NormalX=0 NormalY=0 NormalZ=1 AngleXU=0 Radius=1.5 StartAngle=2e-16 EndAngle=3.14159
    g5: ArcOfCircle CenterX=-16.1 CenterY=-1.8 CenterZ=0 NormalX=0 NormalY=0 NormalZ=1 AngleXU=0 Radius=1.5 StartAngle=5e-16 EndAngle=3.14159
    g6: ArcOfCircle CenterX=-22.1 CenterY=-1.8 CenterZ=0 NormalX=0 NormalY=0 NormalZ=1 AngleXU=0 Radius=1.5 StartAngle=5e-16 EndAngle=3.14159
    g7: ArcOfCircle CenterX=-28.2 CenterY=-4.3 CenterZ=0 NormalX=0 NormalY=0 NormalZ=1 AngleXU=0 Radius=1.5 StartAngle=2e-16 EndAngle=3.14159
    g8: ArcOfCircle CenterX=-10 CenterY=-33.9 CenterZ=0 NormalX=0 NormalY=0 NormalZ=1 AngleXU=0 Radius=1.5 StartAngle=3.14159 EndAngle=6.28319
    g9: ArcOfCircle CenterX=-16.1 CenterY=-36.4 CenterZ=0 NormalX=0 NormalY=0 NormalZ=1 AngleXU=0 Radius=1.5 StartAngle=3.14159 EndAngle=6.28319
    g10: ArcOfCircle CenterX=-22.1 CenterY=-36.4 CenterZ=0 NormalX=0 NormalY=0 NormalZ=1 AngleXU=0 Radius=1.5 StartAngle=3.14159 EndAngle=6.28319
    g11: ArcOfCircle CenterX=-28.2 CenterY=-33.9 CenterZ=0 NormalX=0 NormalY=0 NormalZ=1 AngleXU=0 Radius=1.5 StartAngle=3.14159 EndAngle=6.28319
    g12: LineSegment StartX=-35.7 StartY=-10.5 StartZ=0 EndX=-35.7 EndY=-27.7 EndZ=0
    g13: LineSegment StartX=-32.7 StartY=-10.5 StartZ=0 EndX=-32.7 EndY=-27.7 EndZ=0
    g14: LineSegment StartX=-29.7 StartY=-33.9 StartZ=0 EndX=-29.7 EndY=-4.3 EndZ=0
    g15: LineSegment StartX=-26.7 StartY=-33.9 StartZ=0 EndX=-26.7 EndY=-4.3 EndZ=0
    g16: LineSegment StartX=-2.5 StartY=-10.5 StartZ=0 EndX=-2.5 EndY=-27.7 EndZ=0
    g17: LineSegment StartX=-8.5 StartY=-4.3 StartZ=0 EndX=-8.5 EndY=-33.9 EndZ=0
    g18: LineSegment StartX=-5.5 StartY=-10.5 StartZ=0 EndX=-5.5 EndY=-27.7 EndZ=0
    g19: LineSegment StartX=-11.5 StartY=-4.3 StartZ=0 EndX=-11.5 EndY=-33.9 EndZ=0
    g20: LineSegment StartX=-14.6 StartY=-1.8 StartZ=0 EndX=-14.6 EndY=-36.4 EndZ=0
    g21: LineSegment StartX=-17.6 StartY=-1.8 StartZ=0 EndX=-17.6 EndY=-36.4 EndZ=0
    g22: LineSegment StartX=-20.6 StartY=-36.4 StartZ=0 EndX=-20.6 EndY=-1.8 EndZ=0
    g23: LineSegment StartX=-23.6 StartY=-1.8 StartZ=0 EndX=-23.6 EndY=-36.4 EndZ=0
  constraints (48):
    c: Block(g0)
    c: Block(g1)
    c: Block(g2)
    c: Block(g3)
    c: Block(g4)
    c: Block(g5)
    c: Block(g6)
    c: Block(g7)
    c: Block(g8)
    c: Block(g9)
    c: Block(g10)
    c: Block(g11)
    c: Coincident(g12,g1)
    c: Coincident(g12,g2)
    c: Vertical(g12)
    c: Coincident(g13,g1)
    c: Coincident(g13,g2)
    c: Vertical(g13)
    c: Coincident(g14,g11)
    c: Coincident(g14,g7)
    c: Vertical(g14)
    c: Coincident(g15,g11)
    c: Coincident(g15,g7)
    c: Vertical(g15)
    c: Coincident(g16,g0)
    c: Coincident(g16,g3)
    c: Vertical(g16)
    c: Coincident(g17,g4)
    c: Coincident(g17,g8)
    c: Vertical(g17)
    c: Coincident(g18,g0)
    c: Coincident(g18,g3)
    c: Vertical(g18)
    c: Coincident(g19,g4)
    c: Coincident(g19,g8)
    c: Vertical(g19)
    c: Coincident(g20,g5)
    c: Coincident(g20,g9)
    c: Vertical(g20)
    c: Coincident(g21,g5)
    c: Coincident(g21,g9)
    c: Vertical(g21)
    c: Coincident(g22,g10)
    c: Coincident(g22,g6)
    c: Vertical(g22)
    c: Coincident(g23,g6)
    c: Coincident(g23,g10)
    c: Vertical(g23)
FEATURE [Part::Extrusion] Extrude038  label="removeToCreateFanGrillHoles001"
  Base = -> Sketch047
  Dir = (0,-1,6e-16)
  DirMode = 2
  FaceMakerClass = Part::FaceMakerBullseye
  LengthFwd = 10
  LengthRev = 0
  Placement = pos=(65.4,44,54.82) rot=(0,0,1;0rad)
  Solid = true
  Symmetric = false
FEATURE [Part::Feature] Wire004
  shape: bbox 11 x 5.2 x 2e-07 mm, 0 faces, 0 solids (baked)
FEATURE [Part::Revolution] Revolve095
  Angle = 360
  Axis = (0,1,0)
  Base = (0,0,0)
  FaceMakerClass = Part::FaceMakerBullseye
  Placement = pos=(30.3,38,19.7) rot=(0,0,1;0rad)
  Solid = true
  Source = -> Wire004
  Symmetric = false
FEATURE [Part::Feature] Wire005
  shape: bbox 11 x 5.2 x 2e-07 mm, 0 faces, 0 solids (baked)
FEATURE [Part::Revolution] Revolve096
  Angle = 360
  Axis = (0,1,0)
  Base = (0,0,0)
  FaceMakerClass = Part::FaceMakerBullseye
  Placement = pos=(30.3,38,51.7) rot=(0,0,1;0rad)
  Solid = true
  Source = -> Wire005
  Symmetric = false
FEATURE [Part::Feature] Wire006
  shape: bbox 11 x 5.2 x 2e-07 mm, 0 faces, 0 solids (baked)
FEATURE [Part::Revolution] Revolve097
  Angle = 360
  Axis = (0,1,0)
  Base = (0,0,0)
  FaceMakerClass = Part::FaceMakerBullseye
  Placement = pos=(62.3,38,51.7) rot=(0,0,1;0rad)
  Solid = true
  Source = -> Wire006
  Symmetric = false
FEATURE [Part::Feature] Wire007
  shape: bbox 11 x 5.2 x 2e-07 mm, 0 faces, 0 solids (baked)
FEATURE [Part::Revolution] Revolve098
  Angle = 360
  Axis = (0,1,0)
  Base = (0,0,0)
  FaceMakerClass = Part::FaceMakerBullseye
  Placement = pos=(62.3,38,19.7) rot=(0,0,1;0rad)
  Solid = true
  Source = -> Wire007
  Symmetric = false
FEATURE [Part::MultiFuse] Fusion067  label="fanScrewHousing002"
  Shapes = -> [Revolve098,Revolve097,Revolve096,Revolve095]
FEATURE [Part::Feature] Face091 .. Face094  x4 (patterned run collapsed; names and placements below)
  shape: bbox 3.5 x 17.8 x 2e-07 mm, 1 faces, 0 solids (baked)
FEATURE [Part::Revolution] Revolve099  label="removeToCreateScrewAndThreadedInsertHole026"
  Angle = 360
  Axis = (0,1,0)
  Base = (0,0,0)
  FaceMakerClass = Part::FaceMakerBullseye
  Placement = pos=(62.3,30.3,19.7) rot=(0,0,1;0rad)
  Solid = false
  Source = -> Face091
  Symmetric = false
FEATURE [Part::Revolution] Revolve100  label="removeToCreateScrewAndThreadedInsertHole027"
  Angle = 360
  Axis = (0,1,0)
  Base = (0,0,0)
  FaceMakerClass = Part::FaceMakerBullseye
  Placement = pos=(62.3,30.3,51.7) rot=(0,0,1;0rad)
  Solid = false
  Source = -> Face092
  Symmetric = false
FEATURE [Part::Revolution] Revolve101  label="removeToCreateScrewAndThreadedInsertHole028"
  Angle = 360
  Axis = (0,1,0)
  Base = (0,0,0)
  FaceMakerClass = Part::FaceMakerBullseye
  Placement = pos=(30.3,30.3,19.7) rot=(0,0,1;0rad)
  Solid = false
  Source = -> Face093
  Symmetric = false
FEATURE [Part::Revolution] Revolve102  label="removeToCreateScrewAndThreadedInsertHole029"
  Angle = 360
  Axis = (0,1,0)
  Base = (0,0,0)
  FaceMakerClass = Part::FaceMakerBullseye
  Placement = pos=(30.3,30.3,51.7) rot=(0,0,1;0rad)
  Solid = false
  Source = -> Face094
  Symmetric = false
FEATURE [Part::MultiFuse] Fusion068  label="createThreadedInsertHolesForFan002"
  Shapes = -> [Revolve099,Revolve100,Revolve101,Revolve102]
FEATURE [Part::Cut] Cut026  label="fanScrewHousing003"
  Base = -> Fusion067
  Tool = -> Fusion068
FEATURE [Sketcher::SketchObject] Sketch048
  FullyConstrained = false
  Placement = pos=(0,0,0) rot=(1,0,0;1.5708rad)
  sketch-geometry (24):
    g0: ArcOfCircle CenterX=-4 CenterY=-10.5 CenterZ=0 NormalX=0 NormalY=0 NormalZ=1 AngleXU=0 Radius=1.5 StartAngle=6e-16 EndAngle=3.14159
    g1: ArcOfCircle CenterX=-34.2 CenterY=-10.5 CenterZ=0 NormalX=0 NormalY=0 NormalZ=1 AngleXU=0 Radius=1.5 StartAngle=0 EndAngle=3.14159
    g2: ArcOfCircle CenterX=-34.2 CenterY=-27.7 CenterZ=0 NormalX=0 NormalY=0 NormalZ=1 AngleXU=0 Radius=1.5 StartAngle=3.14159 EndAngle=6.28319
    g3: ArcOfCircle CenterX=-4 CenterY=-27.7 CenterZ=0 NormalX=0 NormalY=0 NormalZ=1 AngleXU=0 Radius=1.5 StartAngle=3.1416 EndAngle=6.28319
    g4: ArcOfCircle CenterX=-10 CenterY=-4.3 CenterZ=0 NormalX=0 NormalY=0 NormalZ=1 AngleXU=0 Radius=1.5 StartAngle=2e-16 EndAngle=3.14159
    g5: ArcOfCircle CenterX=-16.1 CenterY=-1.8 CenterZ=0 NormalX=0 NormalY=0 NormalZ=1 AngleXU=0 Radius=1.5 StartAngle=5e-16 EndAngle=3.14159
    g6: ArcOfCircle CenterX=-22.1 CenterY=-1.8 CenterZ=0 NormalX=0 NormalY=0 NormalZ=1 AngleXU=0 Radius=1.5 StartAngle=5e-16 EndAngle=3.14159
    g7: ArcOfCircle CenterX=-28.2 CenterY=-4.3 CenterZ=0 NormalX=0 NormalY=0 NormalZ=1 AngleXU=0 Radius=1.5 StartAngle=2e-16 EndAngle=3.14159
    g8: ArcOfCircle CenterX=-10 CenterY=-33.9 CenterZ=0 NormalX=0 NormalY=0 NormalZ=1 AngleXU=0 Radius=1.5 StartAngle=3.14159 EndAngle=6.28319
    g9: ArcOfCircle CenterX=-16.1 CenterY=-36.4 CenterZ=0 NormalX=0 NormalY=0 NormalZ=1 AngleXU=0 Radius=1.5 StartAngle=3.14159 EndAngle=6.28319
    g10: ArcOfCircle CenterX=-22.1 CenterY=-36.4 CenterZ=0 NormalX=0 NormalY=0 NormalZ=1 AngleXU=0 Radius=1.5 StartAngle=3.14159 EndAngle=6.28319
    g11: ArcOfCircle CenterX=-28.2 CenterY=-33.9 CenterZ=0 NormalX=0 NormalY=0 NormalZ=1 AngleXU=0 Radius=1.5 StartAngle=3.14159 EndAngle=6.28319
    g12: LineSegment StartX=-35.7 StartY=-10.5 StartZ=0 EndX=-35.7 EndY=-27.7 EndZ=0
    g13: LineSegment StartX=-32.7 StartY=-10.5 StartZ=0 EndX=-32.7 EndY=-27.7 EndZ=0
    g14: LineSegment StartX=-29.7 StartY=-33.9 StartZ=0 EndX=-29.7 EndY=-4.3 EndZ=0
    g15: LineSegment StartX=-26.7 StartY=-33.9 StartZ=0 EndX=-26.7 EndY=-4.3 EndZ=0
    g16: LineSegment StartX=-2.5 StartY=-10.5 StartZ=0 EndX=-2.5 EndY=-27.7 EndZ=0
    g17: LineSegment StartX=-8.5 StartY=-4.3 StartZ=0 EndX=-8.5 EndY=-33.9 EndZ=0
    g18: LineSegment StartX=-5.5 StartY=-10.5 StartZ=0 EndX=-5.5 EndY=-27.7 EndZ=0
    g19: LineSegment StartX=-11.5 StartY=-4.3 StartZ=0 EndX=-11.5 EndY=-33.9 EndZ=0
    g20: LineSegment StartX=-14.6 StartY=-1.8 StartZ=0 EndX=-14.6 EndY=-36.4 EndZ=0
    g21: LineSegment StartX=-17.6 StartY=-1.8 StartZ=0 EndX=-17.6 EndY=-36.4 EndZ=0
    g22: LineSegment StartX=-20.6 StartY=-36.4 StartZ=0 EndX=-20.6 EndY=-1.8 EndZ=0
    g23: LineSegment StartX=-23.6 StartY=-1.8 StartZ=0 EndX=-23.6 EndY=-36.4 EndZ=0
  constraints (48):
    c: Block(g0)
    c: Block(g1)
    c: Block(g2)
    c: Block(g3)
    c: Block(g4)
    c: Block(g5)
    c: Block(g6)
    c: Block(g7)
    c: Block(g8)
    c: Block(g9)
    c: Block(g10)
    c: Block(g11)
    c: Coincident(g12,g1)
    c: Coincident(g12,g2)
    c: Vertical(g12)
    c: Coincident(g13,g1)
    c: Coincident(g13,g2)
    c: Vertical(g13)
    c: Coincident(g14,g11)
    c: Coincident(g14,g7)
    c: Vertical(g14)
    c: Coincident(g15,g11)
    c: Coincident(g15,g7)
    c: Vertical(g15)
    c: Coincident(g16,g0)
    c: Coincident(g16,g3)
    c: Vertical(g16)
    c: Coincident(g17,g4)
    c: Coincident(g17,g8)
    c: Vertical(g17)
    c: Coincident(g18,g0)
    c: Coincident(g18,g3)
    c: Vertical(g18)
    c: Coincident(g19,g4)
    c: Coincident(g19,g8)
    c: Vertical(g19)
    c: Coincident(g20,g5)
    c: Coincident(g20,g9)
    c: Vertical(g20)
    c: Coincident(g21,g5)
    c: Coincident(g21,g9)
    c: Vertical(g21)
    c: Coincident(g22,g10)
    c: Coincident(g22,g6)
    c: Vertical(g22)
    c: Coincident(g23,g6)
    c: Coincident(g23,g10)
    c: Vertical(g23)
FEATURE [Part::Extrusion] Extrude039  label="removeToCreateFanGrillHoles002"
  Base = -> Sketch048
  Dir = (0,-1,6e-16)
  DirMode = 2
  FaceMakerClass = Part::FaceMakerBullseye
  LengthFwd = 10
  LengthRev = 0
  Placement = pos=(65.4,44,54.82) rot=(0,0,1;0rad)
  Solid = true
  Symmetric = false
FEATURE [Part::Cut] Cut027  label="fanScrewHousing004"
  Base = -> Cut026
  Tool = -> Extrude038
FEATURE [Part::Cut] Cut028  label="top014"
  Base = -> Fillet026
  Tool = -> Extrude039
FEATURE [Part::Feature] Face095 .. Face098  x4 (patterned run collapsed; names and placements below)
  shape: bbox 3.5 x 17.8 x 2e-07 mm, 1 faces, 0 solids (baked)
FEATURE [Part::Revolution] Revolve103  label="removeToCreateScrewAndThreadedInsertHole030"
  Angle = 360
  Axis = (0,1,0)
  Base = (0,0,0)
  FaceMakerClass = Part::FaceMakerBullseye
  Placement = pos=(62.3,30.3,19.7) rot=(0,0,1;0rad)
  Solid = false
  Source = -> Face095
  Symmetric = false
FEATURE [Part::Revolution] Revolve104  label="removeToCreateScrewAndThreadedInsertHole031"
  Angle = 360
  Axis = (0,1,0)
  Base = (0,0,0)
  FaceMakerClass = Part::FaceMakerBullseye
  Placement = pos=(62.3,30.3,51.7) rot=(0,0,1;0rad)
  Solid = false
  Source = -> Face096
  Symmetric = false
FEATURE [Part::Revolution] Revolve105  label="removeToCreateScrewAndThreadedInsertHole032"
  Angle = 360
  Axis = (0,1,0)
  Base = (0,0,0)
  FaceMakerClass = Part::FaceMakerBullseye
  Placement = pos=(30.3,30.3,19.7) rot=(0,0,1;0rad)
  Solid = false
  Source = -> Face097
  Symmetric = false
FEATURE [Part::Revolution] Revolve106  label="removeToCreateScrewAndThreadedInsertHole033"
  Angle = 360
  Axis = (0,1,0)
  Base = (0,0,0)
  FaceMakerClass = Part::FaceMakerBullseye
  Placement = pos=(30.3,30.3,51.7) rot=(0,0,1;0rad)
  Solid = false
  Source = -> Face098
  Symmetric = false
FEATURE [Part::MultiFuse] Fusion069  label="createThreadedInsertHolesForFan003"
  Shapes = -> [Revolve103,Revolve104,Revolve105,Revolve106]
FEATURE [Part::Cut] Cut029  label="top015"
  Base = -> Cut028
  Tool = -> Fusion054
FEATURE [Part::Cut] Cut030  label="fanScrewHousing005"
  Base = -> Cut027
  Tool = -> Fusion069
FEATURE [Part::Cylinder] Cylinder026  label="removeToCreteHoleForPlugHousing010"
  Angle = 360
  AttacherType = Attacher::AttachEngine3D
  Height = 20
  Placement = pos=(-2,19,36) rot=(0,1,0;1.5708rad)
  Radius = 14.3
FEATURE [Part::Box] Box018  label="removeToCreteHoleForPlugHousing011"
  AttacherType = Attacher::AttachEngine3D
  Height = 28.6
  Length = 10
  Placement = pos=(-2,0,21.7) rot=(0,0,1;0rad)
  Width = 19
FEATURE [Part::Box] Box019  label="wireHolderBottomCaseBit"
  AttacherType = Attacher::AttachEngine3D
  Height = 28
  Length = 3
  Placement = pos=(0,0,22) rot=(0,0,1;0rad)
  Width = 21
FEATURE [Part::Cylinder] Cylinder027  label="removeToCreteHoleForPlugHousing012"
  Angle = 360
  AttacherType = Attacher::AttachEngine3D
  Height = 20
  Placement = pos=(-2,19,36) rot=(0,1,0;1.5708rad)
  Radius = 14.3
FEATURE [Part::Cut] Cut031  label="wireHolderBottomCaseBit001"
  Base = -> Box019
  Tool = -> Cylinder027
FEATURE [Part::MultiFuse] Fusion070  label="removeToCreteHoleForPlugHousing013"
  Shapes = -> [Box018,Cylinder026]
FEATURE [Part::Cut] Cut032  label="top016"
  Base = -> Cut029
  Tool = -> Fusion070
FEATURE [Part::Cylinder] Cylinder028
  Angle = 360
  AttacherType = Attacher::AttachEngine3D
  Height = 20
  Placement = pos=(0,0,36.15) rot=(0,0,1;0rad)
  Radius = 14.3
FEATURE [Part::Cylinder] Cylinder029
  Angle = 360
  AttacherType = Attacher::AttachEngine3D
  Height = 10
  Placement = pos=(0,0,36.15) rot=(0,0,1;0rad)
  Radius = 4
FEATURE [Part::MultiFuse] Fusion071  label="removeToCreteHoleForPlugHousing014"
  Placement = pos=(70,19,36) rot=(0,1,0;1.5708rad)
  Shapes = -> [Cylinder028,Cylinder029]
FEATURE [Sketcher::SketchObject] Sketch049  label="topSketch011"
  FullyConstrained = false
  sketch-geometry (4):
    g0: ArcOfCircle CenterX=105 CenterY=19 CenterZ=0 NormalX=0 NormalY=0 NormalZ=1 AngleXU=0 Radius=16 StartAngle=5.54125 EndAngle=6.28319
    g1: ArcOfCircle CenterX=105 CenterY=19 CenterZ=0 NormalX=0 NormalY=0 NormalZ=1 AngleXU=0 Radius=19 StartAngle=5.54125 EndAngle=6.28319
    g2: LineSegment StartX=116.795 StartY=8.18859 StartZ=0 EndX=119.006 EndY=6.16145 EndZ=0
    g3: LineSegment StartX=121 StartY=19 StartZ=0 EndX=124 EndY=19 EndZ=0
  constraints (9):
    c: Block(g0)
    c: Block(g2)
    c: Block(g1)
    c: Coincident(g2,g1)
    c: Coincident(g2,g0)
    c: Coincident(g3,g0)
    c: Coincident(g3,g1)
    c: Horizontal(g3)
    c: Block(g3)
FEATURE [Part::Box] Box020  label="removeToCreteHoleForPlugHousing015"
  AttacherType = Attacher::AttachEngine3D
  Height = 28.6
  Length = 20
  Placement = pos=(106.15,0,21.7) rot=(0,0,1;0rad)
  Width = 19
FEATURE [Part::MultiFuse] Fusion072  label="removeToCreteHoleForPlugHousing016"
  Shapes = -> [Box020,Fusion071]
FEATURE [Part::Cut] Cut033  label="removeToCreteHoleForPlugHousing017"
  Base = -> Cut032
  Tool = -> Fusion072
FEATURE [Part::Cylinder] Cylinder030
  Angle = 360
  AttacherType = Attacher::AttachEngine3D
  Height = 20
  Placement = pos=(0,0,36.15) rot=(0,0,1;0rad)
  Radius = 14.3
FEATURE [Part::Cylinder] Cylinder031
  Angle = 360
  AttacherType = Attacher::AttachEngine3D
  Height = 10
  Placement = pos=(0,0,36.15) rot=(0,0,1;0rad)
  Radius = 4
FEATURE [Part::Box] Box021  label="removeToCreteHoleForPlugHousing019"
  AttacherType = Attacher::AttachEngine3D
  Height = 28.6
  Length = 20
  Placement = pos=(106.15,0,21.7) rot=(0,0,1;0rad)
  Width = 19
FEATURE [Part::MultiFuse] Fusion074  label="removeToCreteHoleForPlugHousing020"
  Placement = pos=(70,19,36) rot=(0,1,0;1.5708rad)
  Shapes = -> [Cylinder030,Cylinder031]
FEATURE [Part::MultiFuse] Fusion073  label="removeToCreteHoleForPlugHousing018"
  Placement = pos=(0,0,28.3) rot=(0,0,1;0rad)
  Shapes = -> [Box021,Fusion074]
FEATURE [Part::Cylinder] Cylinder032
  Angle = 360
  AttacherType = Attacher::AttachEngine3D
  Height = 20
  Placement = pos=(0,0,36.15) rot=(0,0,1;0rad)
  Radius = 14.3
FEATURE [Part::Cylinder] Cylinder033
  Angle = 360
  AttacherType = Attacher::AttachEngine3D
  Height = 10
  Placement = pos=(0,0,36.15) rot=(0,0,1;0rad)
  Radius = 4
FEATURE [Part::Box] Box022  label="removeToCreteHoleForPlugHousing021"
  AttacherType = Attacher::AttachEngine3D
  Height = 28.6
  Length = 20
  Placement = pos=(106.15,0,21.7) rot=(0,0,1;0rad)
  Width = 19
FEATURE [Part::MultiFuse] Fusion076  label="removeToCreteHoleForPlugHousing023"
  Placement = pos=(70,19,36) rot=(0,1,0;1.5708rad)
  Shapes = -> [Cylinder032,Cylinder033]
FEATURE [Part::MultiFuse] Fusion075  label="removeToCreteHoleForPlugHousing022"
  Placement = pos=(0,0,-28.3) rot=(0,0,1;0rad)
  Shapes = -> [Box022,Fusion076]
FEATURE [Part::MultiFuse] Fusion077  label="removeToCreatePlugHousingBottomBit"
  Shapes = -> [Fusion075,Fusion073]
FEATURE [Part::Cylinder] Cylinder034
  Angle = 360
  AttacherType = Attacher::AttachEngine3D
  Height = 20
  Placement = pos=(0,0,36.15) rot=(0,0,1;0rad)
  Radius = 14.3
FEATURE [Part::Cylinder] Cylinder035
  Angle = 360
  AttacherType = Attacher::AttachEngine3D
  Height = 10
  Placement = pos=(0,0,36.15) rot=(0,0,1;0rad)
  Radius = 4
FEATURE [Part::MultiFuse] Fusion078  label="removeToCreteHoleForPlugHousing024"
  Placement = pos=(70,19,36) rot=(0,1,0;1.5708rad)
  Shapes = -> [Cylinder034,Cylinder035]
FEATURE [Part::MultiFuse] Fusion079  label="removeToCreatePlugHousingBottomBit001"
  Shapes = -> [Fusion078,Fusion077]
FEATURE [Part::Extrusion] Extrude040  label="bottomPlugHousingBit"
  Base = -> Sketch049
  Dir = (0,0,1)
  DirMode = 2
  FaceMakerClass = Part::FaceMakerBullseye
  LengthFwd = 72
  LengthRev = 0
  Solid = true
  Symmetric = false
FEATURE [Part::Cut] Cut034  label="bottomPlugHousingBit001"
  Base = -> Extrude040
  Tool = -> Fusion079
FEATURE [Part::Box] Box023  label="Cube014"
  AttacherType = Attacher::AttachEngine3D
  Height = 16
  Length = 8
  Placement = pos=(12.7,31.52,28) rot=(0,0,1;0rad)
  Width = 4
FEATURE [Part::Cylinder] Cylinder036
  Angle = 360
  AttacherType = Attacher::AttachEngine3D
  Height = 10
  Placement = pos=(0,0,36.15) rot=(0,0,1;0rad)
  Radius = 4
FEATURE [Part::Cylinder] Cylinder037
  Angle = 360
  AttacherType = Attacher::AttachEngine3D
  Height = 20
  Placement = pos=(0,0,36.15) rot=(0,0,1;0rad)
  Radius = 8.2
FEATURE [Part::MultiFuse] Fusion080  label="removeToCreteHoleForPlugHousing025"
  Placement = pos=(-42,19,36) rot=(0,1,0;1.5708rad)
  Shapes = -> [Cylinder037,Cylinder036]
FEATURE [Sketcher::SketchObject] Sketch050  label="topSketch012"
  FullyConstrained = true
  sketch-geometry (4):
    g0: LineSegment StartX=16.8446 StartY=31.512 StartZ=0 EndX=16.3251 EndY=34.4666 EndZ=0
    g1: ArcOfCircle CenterX=19 CenterY=19.2524 CenterZ=0 NormalX=0 NormalY=0 NormalZ=1 AngleXU=0 Radius=15.4476 StartAngle=1.74483 EndAngle=2.72717
    g2: ArcOfCircle CenterX=19 CenterY=19.2524 CenterZ=0 NormalX=0 NormalY=0 NormalZ=1 AngleXU=0 Radius=12.4476 StartAngle=1.74483 EndAngle=2.73189
    g3: LineSegment StartX=4.86004 StartY=25.4725 StartZ=0 EndX=7.58253 EndY=24.2107 EndZ=0
  constraints (7):
    c: Block(g0)
    c: Coincident(g1,g0)
    c: Coincident(g2,g0)
    c: Coincident(g3,g1)
    c: Coincident(g3,g2)
    c: Block(g1)
    c: Block(g2)
FEATURE [Part::Extrusion] Extrude041
  Base = -> Sketch050
  Dir = (0,0,1)
  DirMode = 2
  FaceMakerClass = Part::FaceMakerBullseye
  LengthFwd = 10.6
  LengthRev = 0
  Placement = pos=(0,0,31) rot=(0,0,1;0rad)
  Solid = true
  Symmetric = false
FEATURE [Part::Cut] Cut035
  Base = -> Extrude041
  Placement = pos=(0,0,-0.3) rot=(0,0,1;0rad)
  Tool = -> Fusion080
FEATURE [Part::Cut] Cut036
  Base = -> Box023
  Tool = -> Cut035
FEATURE [Part::Fillet] Fillet027
  Base = -> Cut036
  Edges = 1 edges r=0.7: [Edge13]
FEATURE [Part::Fillet] Fillet028
  Base = -> Fillet027
  Edges = 1 edges r=0.7: [Edge13]
FEATURE [Part::Fillet] Fillet029
  Base = -> Fillet028
  Edges = 1 edges r=0.7: [Edge16]
FEATURE [Part::Fillet] Fillet030
  Base = -> Fillet029
  Edges = 1 edges r=0.7: [Edge11]
FEATURE [Part::Fillet] Fillet031
  Base = -> Fillet030
  Edges = 1 edges r=0.7: [Edge10]
FEATURE [Part::Fillet] Fillet032
  Base = -> Fillet031
  Edges = 1 edges r=1.2: [Edge5]
FEATURE [Part::Fillet] Fillet033
  Base = -> Fillet032
  Edges = 1 edges r=1.2: [Edge12]
FEATURE [Part::Fillet] Fillet034  label="wireHousingRetainer"
  Base = -> Fillet033
  Edges = 1 edges r=2: [Edge1]
  Placement = pos=(0.3,0,0) rot=(0,0,1;0rad)
FEATURE [Part::Feature] Face099
  shape: bbox 3.5 x 17.8 x 2e-07 mm, 1 faces, 0 solids (baked)
FEATURE [Part::Revolution] Revolve107  label="removeToCreateScrewAndThreadedInsertHole034"
  Angle = 360
  Axis = (0,1,0)
  Base = (0,0,0)
  FaceMakerClass = Part::FaceMakerBullseye
  Placement = pos=(12.5,0,10) rot=(0,0,1;0rad)
  Solid = false
  Source = -> Face099
  Symmetric = false
FEATURE [Part::Feature] Face100
  shape: bbox 3.5 x 17.8 x 2e-07 mm, 1 faces, 0 solids (baked)
FEATURE [Part::Revolution] Revolve108  label="removeToCreateScrewAndThreadedInsertHole035"
  Angle = 360
  Axis = (0,1,0)
  Base = (0,0,0)
  FaceMakerClass = Part::FaceMakerBullseye
  Placement = pos=(12.5,0,62) rot=(0,0,1;0rad)
  Solid = false
  Source = -> Face100
  Symmetric = false
FEATURE [Part::Feature] Face101
  shape: bbox 3.5 x 17.8 x 2e-07 mm, 1 faces, 0 solids (baked)
FEATURE [Part::Revolution] Revolve109  label="removeToCreateScrewAndThreadedInsertHole036"
  Angle = 360
  Axis = (0,1,0)
  Base = (0,0,0)
  FaceMakerClass = Part::FaceMakerBullseye
  Placement = pos=(89.5,0,68.5) rot=(0,0,1;0rad)
  Solid = false
  Source = -> Face101
  Symmetric = false
FEATURE [Part::Feature] Face102
  shape: bbox 3.5 x 17.8 x 2e-07 mm, 1 faces, 0 solids (baked)
FEATURE [Part::Revolution] Revolve110  label="removeToCreateScrewAndThreadedInsertHole037"
  Angle = 360
  Axis = (0,1,0)
  Base = (0,0,0)
  FaceMakerClass = Part::FaceMakerBullseye
  Placement = pos=(89.5,0,3.5) rot=(0,0,1;0rad)
  Solid = false
  Source = -> Face102
  Symmetric = false
FEATURE [Part::Feature] Face103
  shape: bbox 3.5 x 17.8 x 2e-07 mm, 1 faces, 0 solids (baked)
FEATURE [Part::Revolution] Revolve111  label="removeToCreateScrewAndThreadedInsertHole038"
  Angle = 360
  Axis = (0,1,0)
  Base = (0,0,0)
  FaceMakerClass = Part::FaceMakerBullseye
  Placement = pos=(109.5,4.7,3.5) rot=(0,0,1;0rad)
  Solid = false
  Source = -> Face103
  Symmetric = false
FEATURE [Part::Feature] Face104
  shape: bbox 3.5 x 17.8 x 2e-07 mm, 1 faces, 0 solids (baked)
FEATURE [Part::Revolution] Revolve112  label="removeToCreateScrewAndThreadedInsertHole039"
  Angle = 360
  Axis = (0,1,0)
  Base = (0,0,0)
  FaceMakerClass = Part::FaceMakerBullseye
  Placement = pos=(109.5,4.7,68.5) rot=(0,0,1;0rad)
  Solid = false
  Source = -> Face104
  Symmetric = false
FEATURE [Part::MultiFuse] Fusion081  label="removeToCreateScrewAndThreadedInsertHole040"
  Shapes = -> [Revolve107,Revolve108,Revolve109,Revolve110,Revolve111,Revolve112]
FEATURE [Part::MultiFuse] Fusion082  label="casePillars002"
  Shapes = -> [Revolve094,Revolve092,Revolve090,Revolve089,Revolve091,Revolve093]
FEATURE [Part::Cut] Cut037  label="casePillars003"
  Base = -> Fusion082
  Tool = -> Fusion081
FEATURE [Sketcher::SketchObject] Sketch051
  FullyConstrained = true
  Placement = pos=(117,19,0) rot=(0.57735,0.57735,0.57735;2.0944rad)
  sketch-geometry (48):
    g0: LineSegment StartX=-49.19 StartY=69.25 StartZ=0 EndX=-49.19 EndY=66.25 EndZ=0
    g1: LineSegment StartX=-49.19 StartY=63.5 StartZ=0 EndX=-49.19 EndY=60.5 EndZ=0
    g2: LineSegment StartX=-49.19 StartY=57.75 StartZ=0 EndX=-49.19 EndY=54.75 EndZ=0
    g3: LineSegment StartX=-49.19 StartY=52 StartZ=0 EndX=-49.19 EndY=49 EndZ=0
    g4: LineSegment StartX=-49.19 StartY=46.25 StartZ=0 EndX=-49.19 EndY=43.25 EndZ=0
    g5: LineSegment StartX=-49.19 StartY=40.5 StartZ=0 EndX=-49.19 EndY=37.5 EndZ=0
    g6: LineSegment StartX=-49.19 StartY=34.5 StartZ=0 EndX=-49.19 EndY=31.5 EndZ=0
    g7: LineSegment StartX=-49.19 StartY=28.75 StartZ=0 EndX=-49.19 EndY=25.75 EndZ=0
    g8: LineSegment StartX=-49.19 StartY=23 StartZ=0 EndX=-49.19 EndY=20 EndZ=0
    g9: LineSegment StartX=-49.19 StartY=17.25 StartZ=0 EndX=-49.19 EndY=14.25 EndZ=0
    g10: LineSegment StartX=-49.19 StartY=11.5 StartZ=0 EndX=-49.19 EndY=8.5 EndZ=0
    g11: LineSegment StartX=-49.19 StartY=5.75 StartZ=0 EndX=-49.19 EndY=2.75 EndZ=0
    g12: ArcOfCircle CenterX=-1.5 CenterY=67.75 CenterZ=0 NormalX=0 NormalY=0 NormalZ=1 AngleXU=0 Radius=1.5 StartAngle=4.71239 EndAngle=7.85398
    g13: ArcOfCircle CenterX=-1.5 CenterY=62 CenterZ=0 NormalX=0 NormalY=0 NormalZ=1 AngleXU=0 Radius=1.5 StartAngle=4.71239 EndAngle=7.85398
    g14: ArcOfCircle CenterX=-1.5 CenterY=56.25 CenterZ=0 NormalX=0 NormalY=0 NormalZ=1 AngleXU=0 Radius=1.5 StartAngle=4.71239 EndAngle=7.85398
    g15: ArcOfCircle CenterX=-11.49 CenterY=50.5 CenterZ=0 NormalX=0 NormalY=0 NormalZ=1 AngleXU=0 Radius=1.5 StartAngle=4.71239 EndAngle=7.85398
    g16: ArcOfCircle CenterX=-16.28 CenterY=44.75 CenterZ=0 NormalX=0 NormalY=0 NormalZ=1 AngleXU=0 Radius=1.5 StartAngle=4.71239 EndAngle=7.85398
    g17: ArcOfCircle CenterX=-18.2337 CenterY=39 CenterZ=0 NormalX=0 NormalY=0 NormalZ=1 AngleXU=0 Radius=1.5 StartAngle=4.71485 EndAngle=7.85398
    g18: ArcOfCircle CenterX=-16.2837 CenterY=27.25 CenterZ=0 NormalX=0 NormalY=0 NormalZ=1 AngleXU=0 Radius=1.5 StartAngle=4.71485 EndAngle=7.85398
    g19: ArcOfCircle CenterX=-18.2337 CenterY=33 CenterZ=0 NormalX=0 NormalY=0 NormalZ=1 AngleXU=0 Radius=1.5 StartAngle=4.71485 EndAngle=7.85398
    g20: ArcOfCircle CenterX=-11.49 CenterY=21.5 CenterZ=0 NormalX=0 NormalY=0 NormalZ=1 AngleXU=0 Radius=1.5 StartAngle=4.71239 EndAngle=7.85398
    g21: ArcOfCircle CenterX=-1.5 CenterY=4.25 CenterZ=0 NormalX=0 NormalY=0 NormalZ=1 AngleXU=0 Radius=1.5 StartAngle=4.71239 EndAngle=7.85398
    g22: ArcOfCircle CenterX=-1.5 CenterY=10 CenterZ=0 NormalX=0 NormalY=0 NormalZ=1 AngleXU=0 Radius=1.5 StartAngle=4.71239 EndAngle=7.85398
    g23: ArcOfCircle CenterX=-1.5 CenterY=15.75 CenterZ=0 NormalX=0 NormalY=0 NormalZ=1 AngleXU=0 Radius=1.5 StartAngle=4.71239 EndAngle=7.85398
    g24: LineSegment StartX=-49.19 StartY=69.25 StartZ=0 EndX=-1.5 EndY=69.25 EndZ=0
    g25: LineSegment StartX=-49.19 StartY=66.25 StartZ=0 EndX=-1.5 EndY=66.25 EndZ=0
    g26: LineSegment StartX=-49.19 StartY=63.5 StartZ=0 EndX=-1.5 EndY=63.5 EndZ=0
    g27: LineSegment StartX=-49.19 StartY=60.5 StartZ=0 EndX=-1.5 EndY=60.5 EndZ=0
    g28: LineSegment StartX=-49.19 StartY=57.75 StartZ=0 EndX=-1.5 EndY=57.75 EndZ=0
    g29: LineSegment StartX=-49.19 StartY=54.75 StartZ=0 EndX=-1.5 EndY=54.75 EndZ=0
    g30: LineSegment StartX=-49.19 StartY=52 StartZ=0 EndX=-11.49 EndY=52 EndZ=0
    g31: LineSegment StartX=-49.19 StartY=49 StartZ=0 EndX=-11.49 EndY=49 EndZ=0
    g32: LineSegment StartX=-49.19 StartY=46.25 StartZ=0 EndX=-16.28 EndY=46.25 EndZ=0
    g33: LineSegment StartX=-49.19 StartY=43.25 StartZ=0 EndX=-16.28 EndY=43.25 EndZ=0
    g34: LineSegment StartX=-49.19 StartY=40.5 StartZ=0 EndX=-18.2337 EndY=40.5 EndZ=0
    g35: LineSegment StartX=-49.19 StartY=37.5 StartZ=0 EndX=-18.23 EndY=37.5 EndZ=0
    g36: LineSegment StartX=-49.19 StartY=34.5 StartZ=0 EndX=-18.2337 EndY=34.5 EndZ=0
    g37: LineSegment StartX=-49.19 StartY=31.5 StartZ=0 EndX=-18.23 EndY=31.5 EndZ=0
    g38: LineSegment StartX=-49.19 StartY=28.75 StartZ=0 EndX=-16.2837 EndY=28.75 EndZ=0
    g39: LineSegment StartX=-49.19 StartY=25.75 StartZ=0 EndX=-16.28 EndY=25.75 EndZ=0
    g40: LineSegment StartX=-49.19 StartY=23 StartZ=0 EndX=-11.49 EndY=23 EndZ=0
    g41: LineSegment StartX=-49.19 StartY=20 StartZ=0 EndX=-11.49 EndY=20 EndZ=0
    g42: LineSegment StartX=-49.19 StartY=17.25 StartZ=0 EndX=-1.5 EndY=17.25 EndZ=0
    g43: LineSegment StartX=-49.19 StartY=14.25 StartZ=0 EndX=-1.5 EndY=14.25 EndZ=0
    g44: LineSegment StartX=-49.19 StartY=11.5 StartZ=0 EndX=-1.5 EndY=11.5 EndZ=0
    g45: LineSegment StartX=-49.19 StartY=8.5 StartZ=0 EndX=-1.5 EndY=8.5 EndZ=0
    g46: LineSegment StartX=-49.19 StartY=5.75 StartZ=0 EndX=-1.5 EndY=5.75 EndZ=0
    g47: LineSegment StartX=-49.19 StartY=2.75 StartZ=0 EndX=-1.5 EndY=2.75 EndZ=0
  constraints (120):
    c: Vertical(g0)
    c: Distance(g0) = 3
    c: Block(g0)
    c: Vertical(g1)
    c: Distance(g1) = 3
    c: Vertical(g2)
    c: Equal(g0,g2) = 3
    c: Block(g2)
    c: Vertical(g3)
    c: Equal(g1,g3) = 3
    c: Vertical(g4)
    c: Equal(g0,g4) = 3
    c: Block(g4)
    c: Vertical(g5)
    c: Equal(g1,g5) = 3
    c: Vertical(g6)
    c: Equal(g0,g6) = 3
    c: Block(g6)
    c: Vertical(g7)
    c: Equal(g1,g7) = 3
    c: Vertical(g8)
    c: Equal(g0,g8) = 3
    c: Block(g8)
    c: Vertical(g9)
    c: Equal(g1,g9) = 3
    c: Vertical(g10)
    c: Equal(g0,g10) = 3
    c: Block(g10)
    c: Vertical(g11)
    c: Equal(g1,g11) = 3
    c: Block(g12)
    c: Block(g13)
    c: Block(g14)
    c: Block(g15)
    c: Block(g16)
    c: Block(g17)
    c: Block(g18)
    c: Block(g19)
    c: Block(g20)
    c: Block(g21)
    c: Block(g22)
    c: Block(g23)
    c: Block(g11)
    c: Block(g9)
    c: Block(g7)
    c: Block(g5)
    c: Block(g3)
    c: Block(g1)
    c: Coincident(g24,g0)
    c: Coincident(g24,g12)
    c: Horizontal(g24)
    c: Coincident(g25,g0)
    c: Coincident(g25,g12)
    c: Horizontal(g25)
    c: Coincident(g26,g1)
    c: Coincident(g26,g13)
    c: Horizontal(g26)
    c: Coincident(g27,g1)
    c: Coincident(g27,g13)
    c: Horizontal(g27)
    c: Coincident(g28,g2)
    c: Coincident(g28,g14)
    c: Horizontal(g28)
    c: Coincident(g29,g2)
    c: Coincident(g29,g14)
    c: Horizontal(g29)
    c: Coincident(g30,g3)
    c: Coincident(g30,g15)
    c: Horizontal(g30)
    c: Coincident(g31,g3)
    c: Coincident(g31,g15)
    c: Horizontal(g31)
    c: Coincident(g32,g4)
    c: Coincident(g32,g16)
    c: Horizontal(g32)
    c: Coincident(g33,g4)
    c: Coincident(g33,g16)
    c: Horizontal(g33)
    c: Coincident(g34,g5)
    c: Coincident(g34,g17)
    c: Horizontal(g34)
    c: Coincident(g35,g5)
    c: Coincident(g35,g17)
    c: Horizontal(g35)
    c: Coincident(g36,g6)
    c: Coincident(g36,g19)
    c: Horizontal(g36)
    c: Coincident(g37,g6)
    c: Coincident(g37,g19)
    c: Horizontal(g37)
    c: Coincident(g38,g7)
    c: Coincident(g38,g18)
    c: Horizontal(g38)
    c: Coincident(g39,g7)
    c: Coincident(g39,g18)
    c: Horizontal(g39)
    c: Coincident(g40,g8)
    c: Coincident(g40,g20)
    c: Horizontal(g40)
    c: Coincident(g41,g8)
    c: Coincident(g41,g20)
    c: Horizontal(g41)
    c: Coincident(g42,g9)
    c: Coincident(g42,g23)
    c: Horizontal(g42)
    c: Coincident(g43,g9)
    c: Coincident(g43,g23)
    c: Horizontal(g43)
    c: Coincident(g44,g10)
    c: Coincident(g44,g22)
    c: Horizontal(g44)
    c: Coincident(g45,g10)
    c: Coincident(g45,g22)
    c: Horizontal(g45)
    c: Coincident(g46,g11)
    c: Coincident(g46,g21)
    c: Horizontal(g46)
    c: Coincident(g47,g11)
    c: Coincident(g47,g21)
    c: Horizontal(g47)
FEATURE [Part::Extrusion] Extrude042
  Base = -> Sketch051
  Dir = (1,-2e-16,2e-16)
  DirMode = 2
  FaceMakerClass = Part::FaceMakerBullseye
  LengthFwd = 19
  LengthRev = 0
  Placement = pos=(-19,0,0) rot=(0,0,1;0rad)
  Solid = true
  Symmetric = false
FEATURE [Part::Fillet] Fillet035  label="removeToCreateVentalationHoles"
  Base = -> Extrude042
  Edges = <same value as first occurrence — deduplicated (x3 in doc)>
  Placement = pos=(7,0,0) rot=(0,0,1;0rad)
FEATURE [Part::Cut] Cut038  label="top017"
  Base = -> Cut033
  Tool = -> Fillet035
FEATURE [Sketcher::SketchObject] Sketch052  label="bottomSketch001"
  FullyConstrained = true
  sketch-geometry (36):
    g0: LineSegment StartX=6.3 StartY=8 StartZ=0 EndX=3.3 EndY=8 EndZ=0
    g1: LineSegment StartX=3.3 StartY=8 StartZ=0 EndX=3.3 EndY=-6.03275e-07 EndZ=0
    g2: ArcOfCircle CenterX=8.3 CenterY=5 CenterZ=0 NormalX=0 NormalY=0 NormalZ=1 AngleXU=0 Radius=2 StartAngle=3.14159 EndAngle=4.71239
    g3: LineSegment StartX=6.3 StartY=8 StartZ=0 EndX=6.3 EndY=5 EndZ=0
    g4: LineSegment StartX=3.3 StartY=-6.03275e-07 StartZ=0 EndX=105 EndY=-6.03275e-07 EndZ=0
    g5: ArcOfCircle CenterX=136.71 CenterY=19.8336 CenterZ=0 NormalX=0 NormalY=0 NormalZ=1 AngleXU=0 Radius=19 StartAngle=4.71239 EndAngle=5.71103
    g6: ArcOfCircle CenterX=136.71 CenterY=19.8336 CenterZ=0 NormalX=0 NormalY=0 NormalZ=1 AngleXU=0 Radius=12.7 StartAngle=4.71239 EndAngle=6.28319
    g7-g11: Circle x5 (B-spline internal-alignment scaffolding for g12; pole/knot coordinates omitted)
    g12: BSplineCurve PolesCount=5 KnotsCount=3 Degree=3 IsPeriodic=0
    g13: GeomPoint X=136.71 Y=7.13355 Z=0
    g14: GeomPoint X=135.104 Y=5.55301 Z=0
    g15: GeomPoint X=133.41 Y=3.83355 Z=0
    g16-g22: Circle x7 (B-spline internal-alignment scaffolding for g23; pole/knot coordinates omitted)
    g23: BSplineCurve PolesCount=7 KnotsCount=5 Degree=3 IsPeriodic=0
    g24-g28: GeomPoint x5 (B-spline internal-alignment scaffolding for g23; pole/knot coordinates omitted)
    g29: ArcOfCircle CenterX=136.71 CenterY=19.8336 CenterZ=0 NormalX=0 NormalY=0 NormalZ=1 AngleXU=0 Radius=15.7 StartAngle=5.81226 EndAngle=6.28319
    g30: LineSegment StartX=149.41 StartY=19.8336 StartZ=0 EndX=152.41 EndY=19.8336 EndZ=0
    g31: LineSegment StartX=136.71 StartY=7.13355 StartZ=0 EndX=136.71 EndY=3.83355 EndZ=0
    g32: LineSegment StartX=133.41 StartY=3.83355 StartZ=0 EndX=136.71 EndY=3.83355 EndZ=0
    g33: LineSegment StartX=8.3 StartY=3 StartZ=0 EndX=101.7 EndY=3 EndZ=0
    g34: LineSegment StartX=101.7 StartY=3 StartZ=0 EndX=105 EndY=3 EndZ=0
    g35: LineSegment StartX=105 StartY=3 StartZ=0 EndX=105 EndY=6.3 EndZ=0
  constraints (48):
    c: Horizontal(g0)
    c: Distance(g0) = 3
    c: Coincident(g1,g0)
    c: Vertical(g1)
    c: Block(g2)
    c: Block(g0)
    c: Coincident(g3,g0)
    c: Coincident(g3,g2)
    c: Vertical(g3)
    c: Block(g1)
    c: Horizontal(g4)
    c: Distance(g4) = 101.7
    c: Block(g5)
    c: Coincident(g6,g5)
    c: Block(g6)
    c: Coincident(g12,g6)
    c: Equal(g7, g8-g11) x4
    c: InternalAlignment(g7-g11 -> g12) x5
    c: InternalAlignment(g13,g12)
    c: InternalAlignment(g14,g12)
    c: InternalAlignment(g15,g12)
    c: Block(g12)
    c: Equal(g16, g17-g22) x6
    c: Coincident(g23,g5)
    c: InternalAlignment(g16-g22 -> g23) x7
    c: InternalAlignment(g24-g28 -> g23) x5
    c: Block(g23)
    c: Coincident(g29,g23)
    c: Coincident(g30,g6)
    c: Coincident(g30,g29)
    c: Horizontal(g30)
    c: Block(g30)
    c: Block(g29)
    c: Coincident(g1,g4)
    c: Coincident(g31,g6)
    c: Vertical(g31)
    c: Coincident(g32,g12)
    c: Horizontal(g32)
    c: Coincident(g32,g31)
    c: Horizontal(g33)
    c: Distance(g33) = 93.4
    c: Coincident(g33,g2)
    c: Horizontal(g34)
    c: Coincident(g34,g33)
    c: Block(g34)
    c: Coincident(g35,g34)
    c: Vertical(g35)
    c: Distance(g35) = 3.3
FEATURE [Part::Extrusion] Extrude043  label="bottom010"
  Base = -> Sketch052
  Dir = (0,0,1)
  DirMode = 2
  FaceMakerClass = Part::FaceMakerBullseye
  LengthFwd = 71.4
  LengthRev = 0
  Placement = pos=(0,0,0.3) rot=(0,0,1;0rad)
  Solid = true
  Symmetric = false
